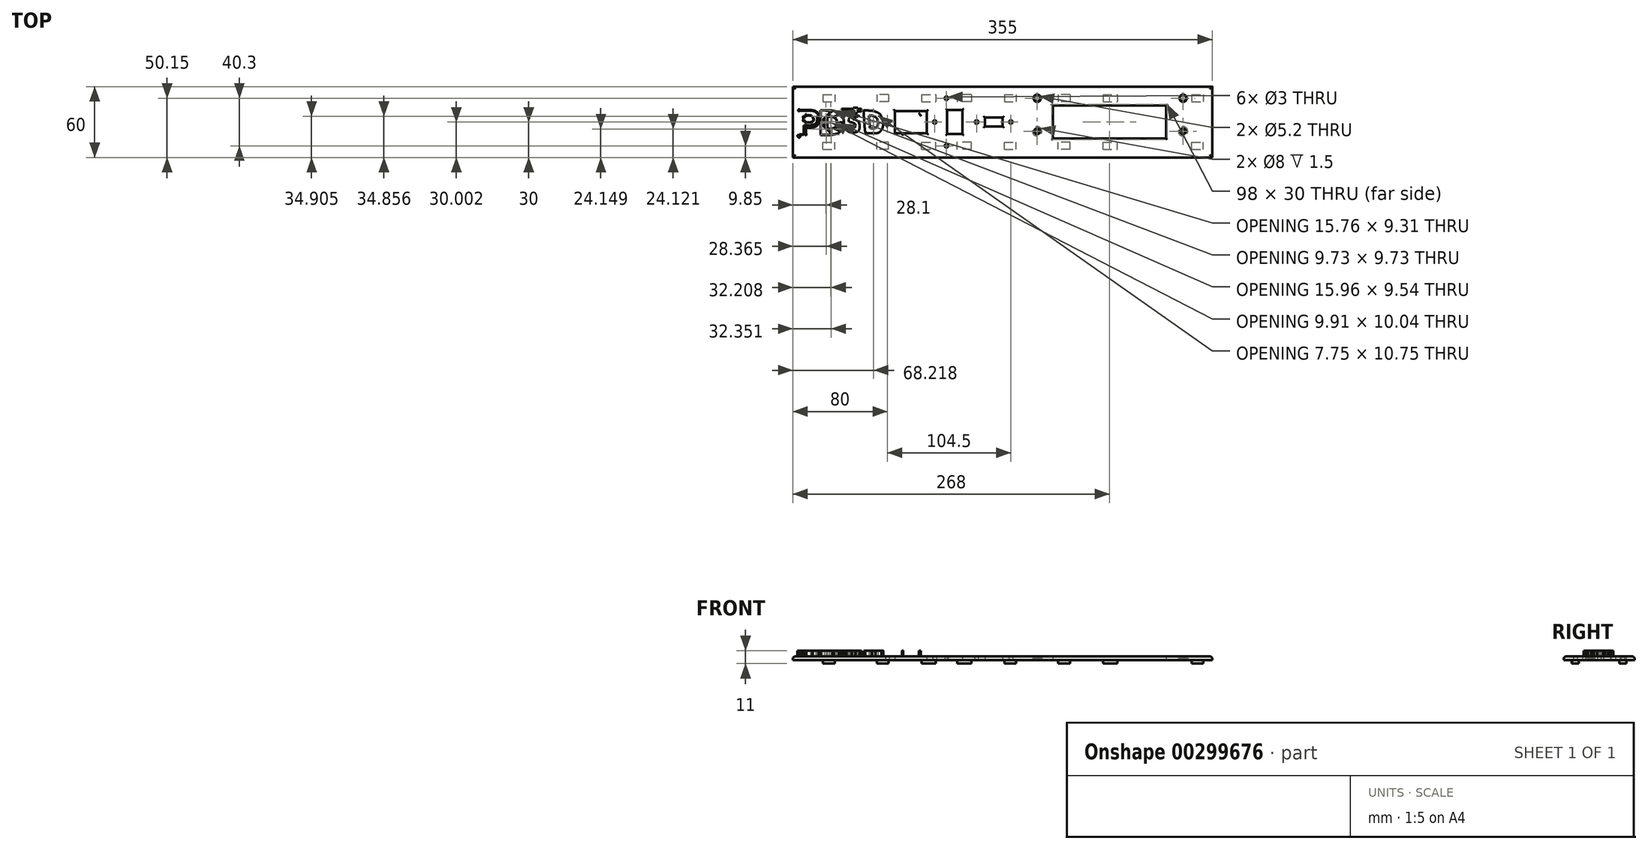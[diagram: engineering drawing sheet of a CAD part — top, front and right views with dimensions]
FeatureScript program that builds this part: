
annotation { "Feature Type Name" : "Feature", "Feature Type Description" : "" }
export const myFeature = defineFeature(function(context is Context, id is Id, definition is map)
    precondition{}
    {
        {
            var Q0;
            Q0=qCreatedBy(makeId("Top.planeOp"),FACE);
            var sketch = newSketch(context, id + "F0", { "sketchPlane" : qUnion([Q0])});
            skLineSegment(sketch, "E0.bottom", {"start": v(60, 30) * mm, "end": v(-60, 30) * mm});
            skLineSegment(sketch, "E0.top", {"start": v(60, -30) * mm, "end": v(-60, -30) * mm});
            skPoint(sketch, "E0.middle", {"position": v(0, 0) * mm});
            skLineSegment(sketch, "E1", {"start": v(0, 0) * mm, "end": v(0, 20.15) * mm, "construction": true});
            skLineSegment(sketch, "E2", {"start": v(-60, 20.15) * mm, "end": v(60, 20.15) * mm, "construction": true});
            skLineSegment(sketch, "E3", {"start": v(-60, 20.15) * mm, "end": v(-53.98, 20.15) * mm, "construction": true});
            skLineSegment(sketch, "E4.bottom", {"start": v(-48.98, 23.1) * mm, "end": v(-58.98, 23.1) * mm});
            skLineSegment(sketch, "E4.top", {"start": v(-48.98, 17.2) * mm, "end": v(-58.98, 17.2) * mm});
            skLineSegment(sketch, "E4.left", {"start": v(-48.98, 23.1) * mm, "end": v(-48.98, 17.2) * mm});
            skLineSegment(sketch, "E4.right", {"start": v(-58.98, 23.1) * mm, "end": v(-58.98, 17.2) * mm});
            skPoint(sketch, "E4.middle", {"position": v(-53.98, 20.15) * mm});
            skLineSegment(sketch, "E5", {"start": v(0, 20.15) * mm, "end": v(-15, 20.15) * mm, "construction": true});
            skLineSegment(sketch, "E6.bottom", {"start": v(-21.02, 23.15) * mm, "end": v(-8.98, 23.15) * mm});
            skLineSegment(sketch, "E6.top", {"start": v(-21.02, 17.15) * mm, "end": v(-8.98, 17.15) * mm});
            skLineSegment(sketch, "E6.left", {"start": v(-21.02, 23.15) * mm, "end": v(-21.02, 17.15) * mm});
            skLineSegment(sketch, "E6.right", {"start": v(-8.98, 23.15) * mm, "end": v(-8.98, 17.15) * mm});
            skPoint(sketch, "E6.middle", {"position": v(-15, 20.15) * mm});
            skLineSegment(sketch, "E7.MirrorCS", {"start": v(48.98, 23.1) * mm, "end": v(58.98, 23.1) * mm});
            skLineSegment(sketch, "E8.MirrorCS", {"start": v(48.98, 17.2) * mm, "end": v(58.98, 17.2) * mm});
            skLineSegment(sketch, "E9.MirrorCS", {"start": v(58.98, 23.1) * mm, "end": v(58.98, 17.2) * mm});
            skLineSegment(sketch, "E10.MirrorCS", {"start": v(48.98, 23.1) * mm, "end": v(48.98, 17.2) * mm});
            skLineSegment(sketch, "E11.MirrorCS", {"start": v(21.02, 17.15) * mm, "end": v(8.98, 17.15) * mm});
            skLineSegment(sketch, "E12.MirrorCS", {"start": v(21.02, 23.15) * mm, "end": v(8.98, 23.15) * mm});
            skLineSegment(sketch, "E13.MirrorCS", {"start": v(21.02, 23.15) * mm, "end": v(21.02, 17.15) * mm});
            skLineSegment(sketch, "E14.MirrorCS", {"start": v(8.98, 23.15) * mm, "end": v(8.98, 17.15) * mm});
            skLineSegment(sketch, "E15.MirrorCS", {"start": v(-58.98, -23.1) * mm, "end": v(-58.98, -17.2) * mm});
            skLineSegment(sketch, "E16.MirrorCS", {"start": v(-48.98, -23.1) * mm, "end": v(-48.98, -17.2) * mm});
            skLineSegment(sketch, "E17.MirrorCS", {"start": v(-21.02, -23.15) * mm, "end": v(-21.02, -17.15) * mm});
            skLineSegment(sketch, "E18.MirrorCS", {"start": v(-8.98, -23.15) * mm, "end": v(-8.98, -17.15) * mm});
            skLineSegment(sketch, "E19.MirrorCS", {"start": v(8.98, -23.15) * mm, "end": v(8.98, -17.15) * mm});
            skLineSegment(sketch, "E20.MirrorCS", {"start": v(21.02, -23.15) * mm, "end": v(21.02, -17.15) * mm});
            skLineSegment(sketch, "E21.MirrorCS", {"start": v(48.98, -23.1) * mm, "end": v(48.98, -17.2) * mm});
            skLineSegment(sketch, "E22.MirrorCS", {"start": v(58.98, -23.1) * mm, "end": v(58.98, -17.2) * mm});
            skLineSegment(sketch, "E23.MirrorCS", {"start": v(48.98, -23.1) * mm, "end": v(58.98, -23.1) * mm});
            skLineSegment(sketch, "E24.MirrorCS", {"start": v(21.02, -23.15) * mm, "end": v(8.98, -23.15) * mm});
            skLineSegment(sketch, "E25.MirrorCS", {"start": v(-21.02, -23.15) * mm, "end": v(-8.98, -23.15) * mm});
            skLineSegment(sketch, "E26.MirrorCS", {"start": v(-48.98, -23.1) * mm, "end": v(-58.98, -23.1) * mm});
            skLineSegment(sketch, "E27.MirrorCS", {"start": v(-48.98, -17.2) * mm, "end": v(-58.98, -17.2) * mm});
            skLineSegment(sketch, "E28.MirrorCS", {"start": v(-21.02, -17.15) * mm, "end": v(-8.98, -17.15) * mm});
            skLineSegment(sketch, "E29.MirrorCS", {"start": v(21.02, -17.15) * mm, "end": v(8.98, -17.15) * mm});
            skLineSegment(sketch, "E30.MirrorCS", {"start": v(48.98, -17.2) * mm, "end": v(58.98, -17.2) * mm});
            skLineSegment(sketch, "E31", {"start": v(0, 0) * mm, "end": v(-30, 0) * mm, "construction": true});
            skLineSegment(sketch, "E32.bottom", {"start": v(-43.5, -9.4) * mm, "end": v(-16.5, -9.4) * mm});
            skLineSegment(sketch, "E32.top", {"start": v(-43.5, 9.4) * mm, "end": v(-16.5, 9.4) * mm});
            skLineSegment(sketch, "E32.left", {"start": v(-43.5, -9.4) * mm, "end": v(-43.5, 9.4) * mm});
            skLineSegment(sketch, "E32.right", {"start": v(-16.5, -9.4) * mm, "end": v(-16.5, 9.4) * mm});
            skPoint(sketch, "E32.middle", {"position": v(-30, 0) * mm});
            skLineSegment(sketch, "E33", {"start": v(60, 0) * mm, "end": v(40, 0) * mm, "construction": true});
            skPoint(sketch, "E33.endSnap0", {"position": v(60, 0) * mm});
            skLineSegment(sketch, "E34.bottom", {"start": v(47.5, 3.75) * mm, "end": v(32.5, 3.75) * mm});
            skLineSegment(sketch, "E34.top", {"start": v(47.5, -3.75) * mm, "end": v(32.5, -3.75) * mm});
            skLineSegment(sketch, "E34.left", {"start": v(47.5, 3.75) * mm, "end": v(47.5, -3.75) * mm});
            skLineSegment(sketch, "E34.right", {"start": v(32.5, 3.75) * mm, "end": v(32.5, -3.75) * mm});
            skPoint(sketch, "E34.middle", {"position": v(40, 0) * mm});
            skLineSegment(sketch, "E35", {"start": v(-30, 0) * mm, "end": v(-50, 0) * mm, "construction": true});
            skLineSegment(sketch, "E36", {"start": v(-30, 0) * mm, "end": v(-10, 0) * mm, "construction": true});
            skCircle(sketch, "E37", {"center": v(-10, 0) * mm, "radius": 1.5 * mm});
            skLineSegment(sketch, "E38", {"start": v(-30, 0) * mm, "end": v(-30, 7) * mm, "construction": true});
            skCircle(sketch, "E39.MirrorC", {"center": v(-50, 0) * mm, "radius": 1.5 * mm});
            skLineSegment(sketch, "E40", {"start": v(40, 0) * mm, "end": v(25.5, 0) * mm, "construction": true});
            skLineSegment(sketch, "E41", {"start": v(40, 0) * mm, "end": v(40, 7) * mm, "construction": true});
            skPoint(sketch, "E41.endSnap0", {"position": v(40, 3.75) * mm});
            skCircle(sketch, "E42", {"center": v(25.5, 0) * mm, "radius": 1.5 * mm});
            skCircle(sketch, "E43.MirrorC", {"center": v(54.5, 0) * mm, "radius": 1.5 * mm});
            skCircle(sketch, "E44", {"center": v(0, 20.15) * mm, "radius": 1.5 * mm});
            skCircle(sketch, "E45.MirrorC", {"center": v(0, -20.15) * mm, "radius": 1.5 * mm});
            skLineSegment(sketch, "E46", {"start": v(0, 0) * mm, "end": v(7, 0) * mm, "construction": true});
            skLineSegment(sketch, "E47.bottom", {"start": v(13.47, 10.2) * mm, "end": v(0.52, 10.2) * mm});
            skLineSegment(sketch, "E47.top", {"start": v(13.48, -10.2) * mm, "end": v(0.53, -10.2) * mm});
            skLineSegment(sketch, "E47.left", {"start": v(13.47, 10.2) * mm, "end": v(13.48, -10.2) * mm});
            skLineSegment(sketch, "E47.right", {"start": v(0.52, 10.2) * mm, "end": v(0.53, -10.2) * mm});
            skPoint(sketch, "E47.middle", {"position": v(7, 0) * mm});
            skLineSegment(sketch, "E48", {"start": v(-60, 30) * mm, "end": v(-130, 30) * mm});
            skLineSegment(sketch, "E49", {"start": v(-130, 30) * mm, "end": v(-130, -30) * mm});
            skLineSegment(sketch, "E50", {"start": v(-130, -30) * mm, "end": v(-60, -30) * mm});
            skLineSegment(sketch, "E51", {"start": v(60, 30) * mm, "end": v(225, 30) * mm});
            skLineSegment(sketch, "E52", {"start": v(225, 30) * mm, "end": v(225, -30) * mm});
            skLineSegment(sketch, "E53", {"start": v(225, -30) * mm, "end": v(60, -30) * mm});
            skLineSegment(sketch, "E54", {"start": v(60, 30) * mm, "end": v(215, 30) * mm, "construction": true});
            skLineSegment(sketch, "E55", {"start": v(215, 30) * mm, "end": v(215, -13.9) * mm, "construction": true});
            skLineSegment(sketch, "E56", {"start": v(215, -13.9) * mm, "end": v(60, -13.9) * mm, "construction": true});
            skLineSegment(sketch, "E57", {"start": v(60, -13.9) * mm, "end": v(60, 30) * mm, "construction": true});
            skLineSegment(sketch, "E58", {"start": v(60, 20.15) * mm, "end": v(76.75, 20.15) * mm, "construction": true});
            skCircle(sketch, "E59", {"center": v(76.75, 20.15) * mm, "radius": 2.6 * mm});
            skLineSegment(sketch, "E60", {"start": v(76.75, 20.15) * mm, "end": v(76.75, -7.85) * mm, "construction": true});
            skCircle(sketch, "E61", {"center": v(76.75, -7.85) * mm, "radius": 1.98 * mm});
            skLineSegment(sketch, "E62", {"start": v(76.75, -7.85) * mm, "end": v(200.25, -7.85) * mm, "construction": true});
            skCircle(sketch, "E63", {"center": v(200.25, -7.85) * mm, "radius": 1.98 * mm});
            skLineSegment(sketch, "E64", {"start": v(200.25, -7.85) * mm, "end": v(200.25, 20.15) * mm, "construction": true});
            skCircle(sketch, "E65", {"center": v(200.25, 20.15) * mm, "radius": 2.6 * mm});
            skLineSegment(sketch, "E66", {"start": v(60, 30) * mm, "end": v(90, 30) * mm, "construction": true});
            skLineSegment(sketch, "E67", {"start": v(90, 30) * mm, "end": v(90, 14) * mm, "construction": true});
            skLineSegment(sketch, "E68.bottom", {"start": v(90, 14) * mm, "end": v(186, 14) * mm});
            skLineSegment(sketch, "E68.top", {"start": v(90, -14) * mm, "end": v(186, -14) * mm});
            skLineSegment(sketch, "E68.left", {"start": v(90, 14) * mm, "end": v(90, -14) * mm});
            skLineSegment(sketch, "E68.right", {"start": v(186, 14) * mm, "end": v(186, -14) * mm});
            skLineSegment(sketch, "E69.MirrorCS", {"start": v(104.52, 23.1) * mm, "end": v(94.52, 23.1) * mm});
            skLineSegment(sketch, "E70.MirrorCS", {"start": v(104.52, 23.1) * mm, "end": v(104.52, 17.2) * mm});
            skLineSegment(sketch, "E71.MirrorCS", {"start": v(94.52, 23.1) * mm, "end": v(94.52, 17.2) * mm});
            skLineSegment(sketch, "E72.MirrorCS", {"start": v(104.52, 17.2) * mm, "end": v(94.52, 17.2) * mm});
            skLineSegment(sketch, "E73.MirrorCS", {"start": v(132.48, 17.15) * mm, "end": v(144.52, 17.15) * mm});
            skLineSegment(sketch, "E74.MirrorCS", {"start": v(132.48, 23.15) * mm, "end": v(144.52, 23.15) * mm});
            skLineSegment(sketch, "E75.MirrorCS", {"start": v(144.52, 23.15) * mm, "end": v(144.52, 17.15) * mm});
            skLineSegment(sketch, "E76.MirrorCS", {"start": v(132.48, 23.15) * mm, "end": v(132.48, 17.15) * mm});
            skLineSegment(sketch, "E77.bottom", {"start": v(207.48, 23.1) * mm, "end": v(217.48, 23.1) * mm});
            skLineSegment(sketch, "E77.top", {"start": v(207.48, 17.2) * mm, "end": v(217.48, 17.2) * mm});
            skLineSegment(sketch, "E77.left", {"start": v(207.48, 23.1) * mm, "end": v(207.48, 17.2) * mm});
            skLineSegment(sketch, "E77.right", {"start": v(217.48, 23.1) * mm, "end": v(217.48, 17.2) * mm});
            skLineSegment(sketch, "E78.MirrorCS", {"start": v(-104.52, 23.1) * mm, "end": v(-104.52, 17.2) * mm});
            skLineSegment(sketch, "E79.MirrorCS", {"start": v(-94.52, 23.1) * mm, "end": v(-94.52, 17.2) * mm});
            skLineSegment(sketch, "E80.MirrorCS", {"start": v(-104.52, 23.1) * mm, "end": v(-94.52, 23.1) * mm});
            skLineSegment(sketch, "E81.MirrorCS", {"start": v(-104.52, 17.2) * mm, "end": v(-94.52, 17.2) * mm});
            skLineSegment(sketch, "E82.MirrorCS", {"start": v(-104.52, -23.1) * mm, "end": v(-94.52, -23.1) * mm});
            skLineSegment(sketch, "E83.MirrorCS", {"start": v(-104.52, -17.2) * mm, "end": v(-94.52, -17.2) * mm});
            skLineSegment(sketch, "E84.MirrorCS", {"start": v(-104.52, -23.1) * mm, "end": v(-104.52, -17.2) * mm});
            skLineSegment(sketch, "E85.MirrorCS", {"start": v(-94.52, -23.1) * mm, "end": v(-94.52, -17.2) * mm});
            skLineSegment(sketch, "E86.MirrorCS", {"start": v(104.52, -23.1) * mm, "end": v(94.52, -23.1) * mm});
            skLineSegment(sketch, "E87.MirrorCS", {"start": v(104.52, -17.2) * mm, "end": v(94.52, -17.2) * mm});
            skLineSegment(sketch, "E88.MirrorCS", {"start": v(94.52, -23.1) * mm, "end": v(94.52, -17.2) * mm});
            skLineSegment(sketch, "E89.MirrorCS", {"start": v(104.52, -23.1) * mm, "end": v(104.52, -17.2) * mm});
            skLineSegment(sketch, "E90.MirrorCS", {"start": v(132.48, -23.15) * mm, "end": v(144.52, -23.15) * mm});
            skLineSegment(sketch, "E91.MirrorCS", {"start": v(132.48, -17.15) * mm, "end": v(144.52, -17.15) * mm});
            skLineSegment(sketch, "E92.MirrorCS", {"start": v(132.48, -23.15) * mm, "end": v(132.48, -17.15) * mm});
            skLineSegment(sketch, "E93.MirrorCS", {"start": v(144.52, -23.15) * mm, "end": v(144.52, -17.15) * mm});
            skLineSegment(sketch, "E94.MirrorCS", {"start": v(207.48, -23.1) * mm, "end": v(207.48, -17.2) * mm});
            skLineSegment(sketch, "E95.MirrorCS", {"start": v(217.48, -23.1) * mm, "end": v(217.48, -17.2) * mm});
            skLineSegment(sketch, "E96.MirrorCS", {"start": v(207.48, -23.1) * mm, "end": v(217.48, -23.1) * mm});
            skLineSegment(sketch, "E97.MirrorCS", {"start": v(207.48, -17.2) * mm, "end": v(217.48, -17.2) * mm});
            skCircle(sketch, "E98", {"center": v(76.75, -7.85) * mm, "radius": 4 * mm});
            skCircle(sketch, "E99", {"center": v(200.25, -7.85) * mm, "radius": 4 * mm});
            skSolve(sketch);
        }
        {
            var Q0;
            Q0=qSketchRegion(id+"F0",true);
            var Q1;
            Q1=makeQuery(id+"F0.imprint","IMPRINT",FACE,{"disambiguationData":[TD([[makeQuery(id+"F0.imprint","IMPRINT",EDGE,{"derivedFrom":sQuery(id+"F0.wireOp",EDGE,"E6.bottom")}),-1.0]])]});
            var Q2;
            Q2=makeQuery(id+"F0.imprint","IMPRINT",FACE,{"disambiguationData":[TD([[makeQuery(id+"F0.imprint","IMPRINT",EDGE,{"derivedFrom":sQuery(id+"F0.wireOp",EDGE,"E11.MirrorCS")}),-1.0]])]});
            var Q3;
            Q3=makeQuery(id+"F0.imprint","IMPRINT",FACE,{"disambiguationData":[TD([[makeQuery(id+"F0.imprint","IMPRINT",EDGE,{"derivedFrom":sQuery(id+"F0.wireOp",EDGE,"E19.MirrorCS")}),-1.0]])]});
            var Q4;
            Q4=makeQuery(id+"F0.imprint","IMPRINT",FACE,{"disambiguationData":[TD([[makeQuery(id+"F0.imprint","IMPRINT",EDGE,{"derivedFrom":sQuery(id+"F0.wireOp",EDGE,"E17.MirrorCS")}),-1.0]])]});
            var Q5;
            Q5=makeQuery(id+"F0.imprint","IMPRINT",FACE,{"disambiguationData":[TD([[makeQuery(id+"F0.imprint","IMPRINT",EDGE,{"derivedFrom":sQuery(id+"F0.wireOp",EDGE,"E4.bottom")}),1.0]])]});
            var Q6;
            Q6=makeQuery(id+"F0.imprint","IMPRINT",FACE,{"disambiguationData":[TD([[makeQuery(id+"F0.imprint","IMPRINT",EDGE,{"derivedFrom":sQuery(id+"F0.wireOp",EDGE,"E15.MirrorCS")}),-1.0]])]});
            var Q7;
            Q7=makeQuery(id+"F0.imprint","IMPRINT",FACE,{"disambiguationData":[TD([[makeQuery(id+"F0.imprint","IMPRINT",EDGE,{"derivedFrom":sQuery(id+"F0.wireOp",EDGE,"E21.MirrorCS")}),-1.0]])]});
            var Q8;
            Q8=makeQuery(id+"F0.imprint","IMPRINT",FACE,{"disambiguationData":[TD([[makeQuery(id+"F0.imprint","IMPRINT",EDGE,{"derivedFrom":sQuery(id+"F0.wireOp",EDGE,"E7.MirrorCS")}),-1.0]])]});
            var Q9;
            Q9=makeQuery(id+"F0.imprint","IMPRINT",FACE,{"disambiguationData":[TD([[makeQuery(id+"F0.imprint","IMPRINT",EDGE,{"derivedFrom":sQuery(id+"F0.wireOp",EDGE,"E78.MirrorCS")}),1.0]])]});
            var Q10;
            Q10=makeQuery(id+"F0.imprint","IMPRINT",FACE,{"disambiguationData":[TD([[makeQuery(id+"F0.imprint","IMPRINT",EDGE,{"derivedFrom":sQuery(id+"F0.wireOp",EDGE,"E82.MirrorCS")}),1.0]])]});
            var Q11;
            Q11=makeQuery(id+"F0.imprint","IMPRINT",FACE,{"disambiguationData":[TD([[makeQuery(id+"F0.imprint","IMPRINT",EDGE,{"derivedFrom":sQuery(id+"F0.wireOp",EDGE,"E86.MirrorCS")}),-1.0]])]});
            var Q12;
            Q12=makeQuery(id+"F0.imprint","IMPRINT",FACE,{"disambiguationData":[TD([[makeQuery(id+"F0.imprint","IMPRINT",EDGE,{"derivedFrom":sQuery(id+"F0.wireOp",EDGE,"E69.MirrorCS")}),1.0]])]});
            var Q13;
            Q13=makeQuery(id+"F0.imprint","IMPRINT",FACE,{"disambiguationData":[TD([[makeQuery(id+"F0.imprint","IMPRINT",EDGE,{"derivedFrom":sQuery(id+"F0.wireOp",EDGE,"E73.MirrorCS")}),1.0]])]});
            var Q14;
            Q14=makeQuery(id+"F0.imprint","IMPRINT",FACE,{"disambiguationData":[TD([[makeQuery(id+"F0.imprint","IMPRINT",EDGE,{"derivedFrom":sQuery(id+"F0.wireOp",EDGE,"E90.MirrorCS")}),1.0]])]});
            var Q15;
            Q15=makeQuery(id+"F0.imprint","IMPRINT",FACE,{"disambiguationData":[TD([[makeQuery(id+"F0.imprint","IMPRINT",EDGE,{"derivedFrom":sQuery(id+"F0.wireOp",EDGE,"E94.MirrorCS")}),-1.0]])]});
            var Q16;
            Q16=makeQuery(id+"F0.imprint","IMPRINT",FACE,{"disambiguationData":[TD([[makeQuery(id+"F0.imprint","IMPRINT",EDGE,{"derivedFrom":sQuery(id+"F0.wireOp",EDGE,"E77.bottom")}),-1.0]])]});
            var Q17;
            Q17=makeQuery(id+"F0.imprint","IMPRINT",FACE,{"disambiguationData":[TD([[makeQuery(id+"F0.imprint","IMPRINT",EDGE,{"derivedFrom":sQuery(id+"F0.wireOp",EDGE,"E61")}),-1.0]])]});
            var Q18;
            Q18=makeQuery(id+"F0.imprint","IMPRINT",FACE,{"disambiguationData":[TD([[makeQuery(id+"F0.imprint","IMPRINT",EDGE,{"derivedFrom":sQuery(id+"F0.wireOp",EDGE,"E63")}),-1.0]])]});
            extrude(context, id + "F1", {"entities" : qUnion([Q0, Q1, Q2, Q3, Q4, Q5, Q6, Q7, Q8, Q9, Q10, Q11, Q12, Q13, Q14, Q15, Q16, Q17, Q18]), "depth" : 3 * mm});
        }
        {
            var Q0;
            Q0=makeQuery(id+"F1.opExtrude","CAP_EDGE",EDGE,{"disambiguationData":[OSD([sQuery(id+"F0.wireOp",EDGE,"E0.top")])],"isStart":false});
            var Q1;
            Q1=makeQuery(id+"F1.opExtrude","CAP_EDGE",EDGE,{"disambiguationData":[OSD([sQuery(id+"F0.wireOp",EDGE,"E0.bottom")])],"isStart":false});
            var Q2;
            Q2=makeQuery(id+"F1.opExtrude","CAP_EDGE",EDGE,{"disambiguationData":[OSD([sQuery(id+"F0.wireOp",EDGE,"E0.right")])],"isStart":false});
            var Q3;
            Q3=makeQuery(id+"F1.opExtrude","CAP_EDGE",EDGE,{"disambiguationData":[OSD([sQuery(id+"F0.wireOp",EDGE,"E0.left")])],"isStart":false});
            var Q4;
            Q4=makeQuery(id+"F1.opExtrude","CAP_EDGE",EDGE,{"disambiguationData":[OSD([sQuery(id+"F0.wireOp",EDGE,"E49")])],"isStart":false});
            var Q5;
            Q5=makeQuery(id+"F1.opExtrude","CAP_EDGE",EDGE,{"disambiguationData":[OSD([sQuery(id+"F0.wireOp",EDGE,"E52")])],"isStart":false});
            fillet(context, id + "F2", {"entities" : qUnion([Q0, Q1, Q2, Q3, Q4, Q5]), "radius" : 2 * mm, "tangentPropagation" : true, "allowEdgeOverflow" : false});
        }
        {
            var Q0;
            Q0=makeQuery(id+"F1.opExtrude","CAP_EDGE",EDGE,{"disambiguationData":[OSD([sQuery(id+"F0.wireOp",EDGE,"E34.left")])],"isStart":false});
            var Q1;
            Q1=makeQuery(id+"F1.opExtrude","CAP_EDGE",EDGE,{"disambiguationData":[OSD([sQuery(id+"F0.wireOp",EDGE,"E34.right")])],"isStart":false});
            var Q2;
            Q2=makeQuery(id+"F1.opExtrude","CAP_EDGE",EDGE,{"disambiguationData":[OSD([sQuery(id+"F0.wireOp",EDGE,"E34.bottom")])],"isStart":false});
            var Q3;
            Q3=makeQuery(id+"F1.opExtrude","CAP_EDGE",EDGE,{"disambiguationData":[OSD([sQuery(id+"F0.wireOp",EDGE,"E34.top")])],"isStart":false});
            var Q4;
            Q4=makeQuery(id+"F1.opExtrude","CAP_EDGE",EDGE,{"disambiguationData":[OSD([sQuery(id+"F0.wireOp",EDGE,"E32.top")])],"isStart":false});
            var Q5;
            Q5=makeQuery(id+"F1.opExtrude","CAP_EDGE",EDGE,{"disambiguationData":[OSD([sQuery(id+"F0.wireOp",EDGE,"E32.bottom")])],"isStart":false});
            var Q6;
            Q6=makeQuery(id+"F1.opExtrude","CAP_EDGE",EDGE,{"disambiguationData":[OSD([sQuery(id+"F0.wireOp",EDGE,"E32.left")])],"isStart":false});
            var Q7;
            Q7=makeQuery(id+"F1.opExtrude","CAP_EDGE",EDGE,{"disambiguationData":[OSD([sQuery(id+"F0.wireOp",EDGE,"E32.right")])],"isStart":false});
            var Q8;
            Q8=makeQuery(id+"F1.opExtrude","CAP_EDGE",EDGE,{"disambiguationData":[OSD([sQuery(id+"F0.wireOp",EDGE,"E47.left")])],"isStart":false});
            var Q9;
            Q9=makeQuery(id+"F1.opExtrude","CAP_EDGE",EDGE,{"disambiguationData":[OSD([sQuery(id+"F0.wireOp",EDGE,"E47.right")])],"isStart":false});
            var Q10;
            Q10=makeQuery(id+"F1.opExtrude","CAP_EDGE",EDGE,{"disambiguationData":[OSD([sQuery(id+"F0.wireOp",EDGE,"E47.bottom")])],"isStart":false});
            var Q11;
            Q11=makeQuery(id+"F1.opExtrude","CAP_EDGE",EDGE,{"disambiguationData":[OSD([sQuery(id+"F0.wireOp",EDGE,"E47.top")])],"isStart":false});
            var Q12;
            Q12=makeQuery(id+"F1.opExtrude","CAP_EDGE",EDGE,{"disambiguationData":[OSD([sQuery(id+"F0.wireOp",EDGE,"E68.bottom")])],"isStart":false});
            var Q13;
            Q13=makeQuery(id+"F1.opExtrude","CAP_EDGE",EDGE,{"disambiguationData":[OSD([sQuery(id+"F0.wireOp",EDGE,"E68.top")])],"isStart":false});
            var Q14;
            Q14=makeQuery(id+"F1.opExtrude","CAP_EDGE",EDGE,{"disambiguationData":[OSD([sQuery(id+"F0.wireOp",EDGE,"E68.left")])],"isStart":false});
            var Q15;
            Q15=makeQuery(id+"F1.opExtrude","CAP_EDGE",EDGE,{"disambiguationData":[OSD([sQuery(id+"F0.wireOp",EDGE,"E68.right")])],"isStart":false});
            var Q16;
            Q16=makeQuery(id+"F1.opExtrude","CAP_EDGE",EDGE,{"disambiguationData":[OSD([sQuery(id+"F0.wireOp",EDGE,"E68.top")])],"isStart":true});
            var Q17;
            Q17=makeQuery(id+"F1.opExtrude","CAP_EDGE",EDGE,{"disambiguationData":[OSD([sQuery(id+"F0.wireOp",EDGE,"E68.bottom")])],"isStart":true});
            var Q18;
            Q18=makeQuery(id+"F1.opExtrude","CAP_EDGE",EDGE,{"disambiguationData":[OSD([sQuery(id+"F0.wireOp",EDGE,"E68.right")])],"isStart":true});
            var Q19;
            Q19=makeQuery(id+"F1.opExtrude","CAP_EDGE",EDGE,{"disambiguationData":[OSD([sQuery(id+"F0.wireOp",EDGE,"E68.left")])],"isStart":true});
            fillet(context, id + "F3", {"entities" : qUnion([Q0, Q1, Q2, Q3, Q4, Q5, Q6, Q7, Q8, Q9, Q10, Q11, Q12, Q13, Q14, Q15, Q16, Q17, Q18, Q19]), "radius" : 1 * mm, "tangentPropagation" : true, "allowEdgeOverflow" : false});
        }
        {
            var Q0;
            Q0=makeQuery(id+"F1.opExtrude","CAP_EDGE",EDGE,{"disambiguationData":[OSD([sQuery(id+"F0.wireOp",EDGE,"E39.MirrorC")])],"isStart":false});
            var Q1;
            Q1=makeQuery(id+"F1.opExtrude","CAP_EDGE",EDGE,{"disambiguationData":[OSD([sQuery(id+"F0.wireOp",EDGE,"E37")])],"isStart":false});
            var Q2;
            Q2=makeQuery(id+"F1.opExtrude","CAP_EDGE",EDGE,{"disambiguationData":[OSD([sQuery(id+"F0.wireOp",EDGE,"E42")])],"isStart":false});
            var Q3;
            Q3=makeQuery(id+"F1.opExtrude","CAP_EDGE",EDGE,{"disambiguationData":[OSD([sQuery(id+"F0.wireOp",EDGE,"E43.MirrorC")])],"isStart":false});
            var Q4;
            Q4=makeQuery(id+"F1.opExtrude","CAP_EDGE",EDGE,{"disambiguationData":[OSD([sQuery(id+"F0.wireOp",EDGE,"E45.MirrorC")])],"isStart":false});
            var Q5;
            Q5=makeQuery(id+"F1.opExtrude","CAP_EDGE",EDGE,{"disambiguationData":[OSD([sQuery(id+"F0.wireOp",EDGE,"E44")])],"isStart":false});
            fillet(context, id + "F4", {"entities" : qUnion([Q0, Q1, Q2, Q3, Q4, Q5]), "radius" : 0.5 * mm, "tangentPropagation" : true, "allowEdgeOverflow" : false});
        }
        {
            var Q0;
            Q0=makeQuery(id+"F0.imprint","IMPRINT",FACE,{"disambiguationData":[TD([[makeQuery(id+"F0.imprint","IMPRINT",EDGE,{"derivedFrom":sQuery(id+"F0.wireOp",EDGE,"E7.MirrorCS")}),-1.0]])]});
            var Q1;
            Q1=makeQuery(id+"F0.imprint","IMPRINT",FACE,{"disambiguationData":[TD([[makeQuery(id+"F0.imprint","IMPRINT",EDGE,{"derivedFrom":sQuery(id+"F0.wireOp",EDGE,"E11.MirrorCS")}),-1.0]])]});
            var Q2;
            Q2=makeQuery(id+"F0.imprint","IMPRINT",FACE,{"disambiguationData":[TD([[makeQuery(id+"F0.imprint","IMPRINT",EDGE,{"derivedFrom":sQuery(id+"F0.wireOp",EDGE,"E6.bottom")}),-1.0]])]});
            var Q3;
            Q3=makeQuery(id+"F0.imprint","IMPRINT",FACE,{"disambiguationData":[TD([[makeQuery(id+"F0.imprint","IMPRINT",EDGE,{"derivedFrom":sQuery(id+"F0.wireOp",EDGE,"E4.bottom")}),1.0]])]});
            var Q4;
            Q4=makeQuery(id+"F0.imprint","IMPRINT",FACE,{"disambiguationData":[TD([[makeQuery(id+"F0.imprint","IMPRINT",EDGE,{"derivedFrom":sQuery(id+"F0.wireOp",EDGE,"E15.MirrorCS")}),-1.0]])]});
            var Q5;
            Q5=makeQuery(id+"F0.imprint","IMPRINT",FACE,{"disambiguationData":[TD([[makeQuery(id+"F0.imprint","IMPRINT",EDGE,{"derivedFrom":sQuery(id+"F0.wireOp",EDGE,"E17.MirrorCS")}),-1.0]])]});
            var Q6;
            Q6=makeQuery(id+"F0.imprint","IMPRINT",FACE,{"disambiguationData":[TD([[makeQuery(id+"F0.imprint","IMPRINT",EDGE,{"derivedFrom":sQuery(id+"F0.wireOp",EDGE,"E19.MirrorCS")}),-1.0]])]});
            var Q7;
            Q7=makeQuery(id+"F0.imprint","IMPRINT",FACE,{"disambiguationData":[TD([[makeQuery(id+"F0.imprint","IMPRINT",EDGE,{"derivedFrom":sQuery(id+"F0.wireOp",EDGE,"E21.MirrorCS")}),-1.0]])]});
            var Q8;
            Q8=makeQuery(id+"F0.imprint","IMPRINT",FACE,{"disambiguationData":[TD([[makeQuery(id+"F0.imprint","IMPRINT",EDGE,{"derivedFrom":sQuery(id+"F0.wireOp",EDGE,"E78.MirrorCS")}),1.0]])]});
            var Q9;
            Q9=makeQuery(id+"F0.imprint","IMPRINT",FACE,{"disambiguationData":[TD([[makeQuery(id+"F0.imprint","IMPRINT",EDGE,{"derivedFrom":sQuery(id+"F0.wireOp",EDGE,"E82.MirrorCS")}),1.0]])]});
            var Q10;
            Q10=makeQuery(id+"F0.imprint","IMPRINT",FACE,{"disambiguationData":[TD([[makeQuery(id+"F0.imprint","IMPRINT",EDGE,{"derivedFrom":sQuery(id+"F0.wireOp",EDGE,"E69.MirrorCS")}),1.0]])]});
            var Q11;
            Q11=makeQuery(id+"F0.imprint","IMPRINT",FACE,{"disambiguationData":[TD([[makeQuery(id+"F0.imprint","IMPRINT",EDGE,{"derivedFrom":sQuery(id+"F0.wireOp",EDGE,"E86.MirrorCS")}),-1.0]])]});
            var Q12;
            Q12=makeQuery(id+"F0.imprint","IMPRINT",FACE,{"disambiguationData":[TD([[makeQuery(id+"F0.imprint","IMPRINT",EDGE,{"derivedFrom":sQuery(id+"F0.wireOp",EDGE,"E73.MirrorCS")}),1.0]])]});
            var Q13;
            Q13=makeQuery(id+"F0.imprint","IMPRINT",FACE,{"disambiguationData":[TD([[makeQuery(id+"F0.imprint","IMPRINT",EDGE,{"derivedFrom":sQuery(id+"F0.wireOp",EDGE,"E90.MirrorCS")}),1.0]])]});
            var Q14;
            Q14=makeQuery(id+"F0.imprint","IMPRINT",FACE,{"disambiguationData":[TD([[makeQuery(id+"F0.imprint","IMPRINT",EDGE,{"derivedFrom":sQuery(id+"F0.wireOp",EDGE,"E77.bottom")}),-1.0]])]});
            var Q15;
            Q15=makeQuery(id+"F0.imprint","IMPRINT",FACE,{"disambiguationData":[TD([[makeQuery(id+"F0.imprint","IMPRINT",EDGE,{"derivedFrom":sQuery(id+"F0.wireOp",EDGE,"E94.MirrorCS")}),-1.0]])]});
            extrude(context, id + "F5", {"entities" : qUnion([Q0, Q1, Q2, Q3, Q4, Q5, Q6, Q7, Q8, Q9, Q10, Q11, Q12, Q13, Q14, Q15]), "operationType" : NewBodyOperationType.ADD, "oppositeDirection" : true, "depth" : 3 * mm});
        }
        {
            var Q0;
            Q0=makeQuery(id+"F1.opExtrude","CAP_EDGE",EDGE,{"disambiguationData":[OSD([sQuery(id+"F0.wireOp",EDGE,"E59")])],"isStart":false});
            var Q1;
            Q1=makeQuery(id+"F1.opExtrude","CAP_EDGE",EDGE,{"disambiguationData":[OSD([sQuery(id+"F0.wireOp",EDGE,"E65")])],"isStart":false});
            var Q2;
            Q2=makeQuery(id+"F1.opExtrude","CAP_FACE",FACE,{"disambiguationData":[OSD([sQuery(id+"F0.wireOp",EDGE,"E0.bottom"),sQuery(id+"F0.wireOp",EDGE,"E0.top"),sQuery(id+"F0.wireOp",EDGE,"E32.bottom"),sQuery(id+"F0.wireOp",EDGE,"E32.top"),sQuery(id+"F0.wireOp",EDGE,"E32.left"),sQuery(id+"F0.wireOp",EDGE,"E32.right"),sQuery(id+"F0.wireOp",EDGE,"E34.bottom"),sQuery(id+"F0.wireOp",EDGE,"E34.top"),sQuery(id+"F0.wireOp",EDGE,"E34.left"),sQuery(id+"F0.wireOp",EDGE,"E34.right"),sQuery(id+"F0.wireOp",EDGE,"E37"),sQuery(id+"F0.wireOp",EDGE,"E39.MirrorC"),sQuery(id+"F0.wireOp",EDGE,"E42"),sQuery(id+"F0.wireOp",EDGE,"E43.MirrorC"),sQuery(id+"F0.wireOp",EDGE,"E44"),sQuery(id+"F0.wireOp",EDGE,"E45.MirrorC"),sQuery(id+"F0.wireOp",EDGE,"E47.bottom"),sQuery(id+"F0.wireOp",EDGE,"E47.top"),sQuery(id+"F0.wireOp",EDGE,"E47.left"),sQuery(id+"F0.wireOp",EDGE,"E47.right"),sQuery(id+"F0.wireOp",EDGE,"E48"),sQuery(id+"F0.wireOp",EDGE,"E49"),sQuery(id+"F0.wireOp",EDGE,"E50"),sQuery(id+"F0.wireOp",EDGE,"E51"),sQuery(id+"F0.wireOp",EDGE,"E52"),sQuery(id+"F0.wireOp",EDGE,"E53"),sQuery(id+"F0.wireOp",EDGE,"E59"),sQuery(id+"F0.wireOp",EDGE,"E61"),sQuery(id+"F0.wireOp",EDGE,"E63"),sQuery(id+"F0.wireOp",EDGE,"E65"),sQuery(id+"F0.wireOp",EDGE,"E68.bottom"),sQuery(id+"F0.wireOp",EDGE,"E68.top"),sQuery(id+"F0.wireOp",EDGE,"E68.left"),sQuery(id+"F0.wireOp",EDGE,"E68.right")])],"isStart":false});
            chamfer(context, id + "F6", {"entities" : qUnion([Q0, Q1, Q2]), "width" : .5 * mm, "tangentPropagation" : true});
        }
        {
            var Q0;
            Q0=makeQuery(id+"F0.imprint","IMPRINT",FACE,{"disambiguationData":[TD([[makeQuery(id+"F0.imprint","IMPRINT",EDGE,{"derivedFrom":sQuery(id+"F0.wireOp",EDGE,"E61")}),-1.0]])]});
            var Q1;
            Q1=makeQuery(id+"F0.imprint","IMPRINT",FACE,{"disambiguationData":[TD([[makeQuery(id+"F0.imprint","IMPRINT",EDGE,{"derivedFrom":sQuery(id+"F0.wireOp",EDGE,"E63")}),-1.0]])]});
            extrude(context, id + "F7", {"entities" : qUnion([Q0, Q1]), "operationType" : NewBodyOperationType.REMOVE, "depth" : 1.5 * mm});
        }
        {
            var Q0;
            Q0=makeQuery(id+"F1.opExtrude","CAP_FACE",FACE,{"disambiguationData":[OSD([sQuery(id+"F0.wireOp",EDGE,"E0.bottom"),sQuery(id+"F0.wireOp",EDGE,"E0.top"),sQuery(id+"F0.wireOp",EDGE,"E32.bottom"),sQuery(id+"F0.wireOp",EDGE,"E32.top"),sQuery(id+"F0.wireOp",EDGE,"E32.left"),sQuery(id+"F0.wireOp",EDGE,"E32.right"),sQuery(id+"F0.wireOp",EDGE,"E34.bottom"),sQuery(id+"F0.wireOp",EDGE,"E34.top"),sQuery(id+"F0.wireOp",EDGE,"E34.left"),sQuery(id+"F0.wireOp",EDGE,"E34.right"),sQuery(id+"F0.wireOp",EDGE,"E37"),sQuery(id+"F0.wireOp",EDGE,"E39.MirrorC"),sQuery(id+"F0.wireOp",EDGE,"E42"),sQuery(id+"F0.wireOp",EDGE,"E43.MirrorC"),sQuery(id+"F0.wireOp",EDGE,"E44"),sQuery(id+"F0.wireOp",EDGE,"E45.MirrorC"),sQuery(id+"F0.wireOp",EDGE,"E47.bottom"),sQuery(id+"F0.wireOp",EDGE,"E47.top"),sQuery(id+"F0.wireOp",EDGE,"E47.left"),sQuery(id+"F0.wireOp",EDGE,"E47.right"),sQuery(id+"F0.wireOp",EDGE,"E48"),sQuery(id+"F0.wireOp",EDGE,"E49"),sQuery(id+"F0.wireOp",EDGE,"E50"),sQuery(id+"F0.wireOp",EDGE,"E51"),sQuery(id+"F0.wireOp",EDGE,"E52"),sQuery(id+"F0.wireOp",EDGE,"E53"),sQuery(id+"F0.wireOp",EDGE,"E59"),sQuery(id+"F0.wireOp",EDGE,"E61"),sQuery(id+"F0.wireOp",EDGE,"E63"),sQuery(id+"F0.wireOp",EDGE,"E65"),sQuery(id+"F0.wireOp",EDGE,"E68.bottom"),sQuery(id+"F0.wireOp",EDGE,"E68.top"),sQuery(id+"F0.wireOp",EDGE,"E68.left"),sQuery(id+"F0.wireOp",EDGE,"E68.right")])],"isStart":false});
            var sketch = newSketch(context, id + "F8", { "sketchPlane" : qUnion([Q0])});
            skFitSpline(sketch, "E100", {"points": [v(-37.7, -11.02) * mm, v(-37.14, -11.02) * mm, v(-36.95, -10.98) * mm, v(-37.17, -10.9) * mm]});
            skFitSpline(sketch, "E101", {"points": [v(-37.17, -10.9) * mm, v(-37.3, -10.85) * mm, v(-37.46, -10.53) * mm, v(-37.46, -10.31) * mm]});
            skFitSpline(sketch, "E102", {"points": [v(-37.46, -10.31) * mm, v(-37.46, -9.87) * mm, v(-37.22, -9.63) * mm, v(-36.75, -9.63) * mm]});
            skFitSpline(sketch, "E103", {"points": [v(-36.75, -9.63) * mm, v(-36.49, -9.63) * mm, v(-36.42, -9.65) * mm, v(-36.26, -9.8) * mm]});
            skLineSegment(sketch, "E104", {"start": v(-37.09, -12.95) * mm, "end": v(-37.09, -12.74) * mm});
            skLineSegment(sketch, "E105", {"start": v(-37.09, -12.74) * mm, "end": v(-37.4, -12.74) * mm});
            skLineSegment(sketch, "E106", {"start": v(-37.4, -12.74) * mm, "end": v(-37.73, -12.74) * mm});
            skLineSegment(sketch, "E107", {"start": v(-37.73, -12.74) * mm, "end": v(-37.73, -12.42) * mm});
            skLineSegment(sketch, "E108", {"start": v(-37.73, -12.42) * mm, "end": v(-37.73, -12.1) * mm});
            skLineSegment(sketch, "E109", {"start": v(-37.73, -12.1) * mm, "end": v(-37.4, -12.1) * mm});
            skLineSegment(sketch, "E110", {"start": v(-37.4, -12.1) * mm, "end": v(-37.09, -12.1) * mm});
            skLineSegment(sketch, "E111", {"start": v(-37.09, -12.1) * mm, "end": v(-37.09, -11.88) * mm});
            skLineSegment(sketch, "E112", {"start": v(-37.09, -11.88) * mm, "end": v(-37.09, -11.67) * mm});
            skLineSegment(sketch, "E113", {"start": v(-37.09, -11.67) * mm, "end": v(-37.7, -11.67) * mm});
            skLineSegment(sketch, "E114", {"start": v(-37.7, -11.67) * mm, "end": v(-38.32, -11.67) * mm});
            skLineSegment(sketch, "E115", {"start": v(-38.32, -11.67) * mm, "end": v(-38.32, -11.35) * mm});
            skLineSegment(sketch, "E116", {"start": v(-38.32, -11.35) * mm, "end": v(-38.32, -11.02) * mm});
            skLineSegment(sketch, "E117", {"start": v(-38.32, -11.02) * mm, "end": v(-37.7, -11.02) * mm});
            skFitSpline(sketch, "E118", {"points": [v(-30.69, -2.23) * mm, v(-29.26, -2.23) * mm, v(-27.84, -2.2) * mm, v(-27.54, -2.18) * mm]});
            skFitSpline(sketch, "E119", {"points": [v(-27.54, -2.18) * mm, v(-25.4, -1.96) * mm, v(-23.68, -1.14) * mm, v(-22.8, 0.1) * mm]});
            skFitSpline(sketch, "E120", {"points": [v(-22.8, 0.1) * mm, v(-22.5, 0.54) * mm, v(-22.32, 0.89) * mm, v(-22.15, 1.45) * mm]});
            skFitSpline(sketch, "E121", {"points": [v(-22.15, 1.45) * mm, v(-22.03, 1.85) * mm, v(-22.01, 2.02) * mm, v(-22, 2.67) * mm]});
            skFitSpline(sketch, "E122", {"points": [v(-22, 2.67) * mm, v(-22, 3.8) * mm, v(-22.2, 4.5) * mm, v(-22.75, 5.35) * mm]});
            skFitSpline(sketch, "E123", {"points": [v(-22.75, 5.35) * mm, v(-23.4, 6.32) * mm, v(-24.37, 7) * mm, v(-25.77, 7.47) * mm]});
            skFitSpline(sketch, "E124", {"points": [v(-25.77, 7.47) * mm, v(-26.99, 7.87) * mm, v(-26.87, 7.86) * mm, v(-31.93, 7.88) * mm]});
            skLineSegment(sketch, "E125", {"start": v(-36.26, -9.8) * mm, "end": v(-36.08, -9.95) * mm});
            skLineSegment(sketch, "E126", {"start": v(-36.08, -9.95) * mm, "end": v(-34.68, -9.95) * mm});
            skLineSegment(sketch, "E127", {"start": v(-34.68, -9.95) * mm, "end": v(-33.28, -9.95) * mm});
            skLineSegment(sketch, "E128", {"start": v(-33.28, -9.95) * mm, "end": v(-33.28, -6.1) * mm});
            skLineSegment(sketch, "E129", {"start": v(-33.28, -6.1) * mm, "end": v(-33.28, -2.23) * mm});
            skLineSegment(sketch, "E130", {"start": v(-33.28, -2.23) * mm, "end": v(-30.69, -2.23) * mm});
            skFitSpline(sketch, "E131", {"points": [v(-36.44, 0.72) * mm, v(-36.44, -6.4) * mm, v(-36.44, -6.47) * mm, v(-36.34, -6.52) * mm]});
            skFitSpline(sketch, "E132", {"points": [v(-36.34, -6.52) * mm, v(-36.09, -6.66) * mm, v(-35.99, -7.17) * mm, v(-36.15, -7.49) * mm]});
            skFitSpline(sketch, "E133", {"points": [v(-36.15, -7.49) * mm, v(-36.38, -7.93) * mm, v(-37.2, -7.91) * mm, v(-37.39, -7.46) * mm]});
            skFitSpline(sketch, "E134", {"points": [v(-37.39, -7.46) * mm, v(-37.53, -7.12) * mm, v(-37.44, -6.71) * mm, v(-37.2, -6.54) * mm]});
            skFitSpline(sketch, "E135", {"points": [v(-37.2, -6.54) * mm, v(-37.09, -6.46) * mm, v(-37.09, -6.36) * mm, v(-37.09, 1.04) * mm]});
            skLineSegment(sketch, "E136", {"start": v(-31.93, 7.88) * mm, "end": v(-36.44, 7.9) * mm});
            skLineSegment(sketch, "E137", {"start": v(-36.44, 7.9) * mm, "end": v(-36.44, 0.72) * mm});
            skFitSpline(sketch, "E138", {"points": [v(-32.42, 8.54) * mm, v(-29.52, 8.54) * mm, v(-27.56, 8.52) * mm, v(-27.24, 8.48) * mm]});
            skFitSpline(sketch, "E139", {"points": [v(-27.24, 8.48) * mm, v(-25.12, 8.25) * mm, v(-23.23, 7.28) * mm, v(-22.26, 5.93) * mm]});
            skFitSpline(sketch, "E140", {"points": [v(-22.26, 5.93) * mm, v(-21.94, 5.48) * mm, v(-21.62, 4.79) * mm, v(-21.48, 4.22) * mm]});
            skFitSpline(sketch, "E141", {"points": [v(-21.48, 4.22) * mm, v(-21.37, 3.8) * mm, v(-21.36, 3.6) * mm, v(-21.36, 2.72) * mm]});
            skFitSpline(sketch, "E142", {"points": [v(-21.36, 2.72) * mm, v(-21.36, 1.85) * mm, v(-21.38, 1.64) * mm, v(-21.48, 1.28) * mm]});
            skFitSpline(sketch, "E143", {"points": [v(-21.48, 1.28) * mm, v(-22, -0.62) * mm, v(-23.55, -1.98) * mm, v(-25.87, -2.58) * mm]});
            skFitSpline(sketch, "E144", {"points": [v(-25.87, -2.58) * mm, v(-26.85, -2.84) * mm, v(-27.4, -2.88) * mm, v(-30.12, -2.88) * mm]});
            skLineSegment(sketch, "E145", {"start": v(-37.09, 1.04) * mm, "end": v(-37.09, 8.54) * mm});
            skLineSegment(sketch, "E146", {"start": v(-37.09, 8.54) * mm, "end": v(-32.42, 8.54) * mm});
            skFitSpline(sketch, "E147", {"points": [v(-36.25, -10.8) * mm, v(-36.32, -10.88) * mm, v(-36.39, -10.97) * mm, v(-36.39, -10.99) * mm]});
            skFitSpline(sketch, "E148", {"points": [v(-36.39, -10.99) * mm, v(-36.39, -11) * mm, v(-36.11, -11.02) * mm, v(-35.77, -11.02) * mm]});
            skLineSegment(sketch, "E149", {"start": v(-30.12, -2.88) * mm, "end": v(-32.64, -2.88) * mm});
            skLineSegment(sketch, "E150", {"start": v(-32.64, -2.88) * mm, "end": v(-32.64, -6.76) * mm});
            skLineSegment(sketch, "E151", {"start": v(-32.64, -6.76) * mm, "end": v(-32.64, -10.65) * mm});
            skLineSegment(sketch, "E152", {"start": v(-32.64, -10.65) * mm, "end": v(-34.37, -10.65) * mm});
            skLineSegment(sketch, "E153", {"start": v(-34.37, -10.65) * mm, "end": v(-36.1, -10.65) * mm});
            skLineSegment(sketch, "E154", {"start": v(-36.1, -10.65) * mm, "end": v(-36.25, -10.8) * mm});
            skLineSegment(sketch, "E155", {"start": v(-35.77, -11.02) * mm, "end": v(-35.16, -11.02) * mm});
            skLineSegment(sketch, "E156", {"start": v(-35.16, -11.02) * mm, "end": v(-35.16, -11.35) * mm});
            skLineSegment(sketch, "E157", {"start": v(-35.16, -11.35) * mm, "end": v(-35.16, -11.67) * mm});
            skLineSegment(sketch, "E158", {"start": v(-35.16, -11.67) * mm, "end": v(-35.77, -11.67) * mm});
            skLineSegment(sketch, "E159", {"start": v(-35.77, -11.67) * mm, "end": v(-36.39, -11.67) * mm});
            skLineSegment(sketch, "E160", {"start": v(-36.39, -11.67) * mm, "end": v(-36.39, -11.88) * mm});
            skLineSegment(sketch, "E161", {"start": v(-36.39, -11.88) * mm, "end": v(-36.39, -12.1) * mm});
            skLineSegment(sketch, "E162", {"start": v(-36.39, -12.1) * mm, "end": v(-36.07, -12.1) * mm});
            skLineSegment(sketch, "E163", {"start": v(-36.07, -12.1) * mm, "end": v(-35.75, -12.1) * mm});
            skLineSegment(sketch, "E164", {"start": v(-35.75, -12.1) * mm, "end": v(-35.75, -12.42) * mm});
            skLineSegment(sketch, "E165", {"start": v(-35.75, -12.42) * mm, "end": v(-35.75, -12.74) * mm});
            skLineSegment(sketch, "E166", {"start": v(-35.75, -12.74) * mm, "end": v(-36.07, -12.74) * mm});
            skLineSegment(sketch, "E167", {"start": v(-36.07, -12.74) * mm, "end": v(-36.39, -12.74) * mm});
            skLineSegment(sketch, "E168", {"start": v(-36.39, -12.74) * mm, "end": v(-36.39, -12.95) * mm});
            skLineSegment(sketch, "E169", {"start": v(-36.39, -12.95) * mm, "end": v(-36.39, -13.17) * mm});
            skLineSegment(sketch, "E170", {"start": v(-36.39, -13.17) * mm, "end": v(-36.74, -13.17) * mm});
            skLineSegment(sketch, "E171", {"start": v(-36.74, -13.17) * mm, "end": v(-37.09, -13.17) * mm});
            skLineSegment(sketch, "E172", {"start": v(-37.09, -13.17) * mm, "end": v(-37.09, -12.95) * mm});
            skFitSpline(sketch, "E173", {"points": [v(-36.5, -10.99) * mm, v(-36.5, -10.9) * mm, v(-36.44, -10.78) * mm, v(-36.35, -10.7) * mm]});
            skLineSegment(sketch, "E174", {"start": v(-36.5, -12.85) * mm, "end": v(-36.5, -12.63) * mm});
            skLineSegment(sketch, "E175", {"start": v(-36.5, -12.63) * mm, "end": v(-36.18, -12.63) * mm});
            skLineSegment(sketch, "E176", {"start": v(-36.18, -12.63) * mm, "end": v(-35.85, -12.63) * mm});
            skLineSegment(sketch, "E177", {"start": v(-35.85, -12.63) * mm, "end": v(-35.85, -12.42) * mm});
            skLineSegment(sketch, "E178", {"start": v(-35.85, -12.42) * mm, "end": v(-35.85, -12.2) * mm});
            skLineSegment(sketch, "E179", {"start": v(-35.85, -12.2) * mm, "end": v(-36.18, -12.2) * mm});
            skLineSegment(sketch, "E180", {"start": v(-36.18, -12.2) * mm, "end": v(-36.5, -12.2) * mm});
            skLineSegment(sketch, "E181", {"start": v(-36.5, -12.2) * mm, "end": v(-36.5, -11.88) * mm});
            skLineSegment(sketch, "E182", {"start": v(-36.5, -11.88) * mm, "end": v(-36.5, -11.56) * mm});
            skLineSegment(sketch, "E183", {"start": v(-36.5, -11.56) * mm, "end": v(-35.88, -11.56) * mm});
            skLineSegment(sketch, "E184", {"start": v(-35.88, -11.56) * mm, "end": v(-35.26, -11.56) * mm});
            skLineSegment(sketch, "E185", {"start": v(-35.26, -11.56) * mm, "end": v(-35.26, -11.35) * mm});
            skLineSegment(sketch, "E186", {"start": v(-35.26, -11.35) * mm, "end": v(-35.26, -11.13) * mm});
            skLineSegment(sketch, "E187", {"start": v(-35.26, -11.13) * mm, "end": v(-35.88, -11.13) * mm});
            skLineSegment(sketch, "E188", {"start": v(-35.88, -11.13) * mm, "end": v(-36.5, -11.13) * mm});
            skLineSegment(sketch, "E189", {"start": v(-36.5, -11.13) * mm, "end": v(-36.5, -10.99) * mm});
            skFitSpline(sketch, "E190", {"points": [v(-30.23, -2.77) * mm, v(-27.5, -2.77) * mm, v(-26.96, -2.73) * mm, v(-25.98, -2.48) * mm]});
            skFitSpline(sketch, "E191", {"points": [v(-25.98, -2.48) * mm, v(-23.65, -1.87) * mm, v(-22.1, -0.51) * mm, v(-21.59, 1.38) * mm]});
            skFitSpline(sketch, "E192", {"points": [v(-21.59, 1.38) * mm, v(-21.42, 2.02) * mm, v(-21.41, 3.43) * mm, v(-21.59, 4.1) * mm]});
            skFitSpline(sketch, "E193", {"points": [v(-21.59, 4.1) * mm, v(-22.1, 6.18) * mm, v(-23.77, 7.61) * mm, v(-26.37, 8.21) * mm]});
            skFitSpline(sketch, "E194", {"points": [v(-26.37, 8.21) * mm, v(-27.23, 8.41) * mm, v(-27.74, 8.43) * mm, v(-32.42, 8.43) * mm]});
            skLineSegment(sketch, "E195", {"start": v(-36.35, -10.7) * mm, "end": v(-36.2, -10.54) * mm});
            skLineSegment(sketch, "E196", {"start": v(-36.2, -10.54) * mm, "end": v(-34.48, -10.54) * mm});
            skLineSegment(sketch, "E197", {"start": v(-34.48, -10.54) * mm, "end": v(-32.75, -10.54) * mm});
            skLineSegment(sketch, "E198", {"start": v(-32.75, -10.54) * mm, "end": v(-32.75, -6.66) * mm});
            skLineSegment(sketch, "E199", {"start": v(-32.75, -6.66) * mm, "end": v(-32.75, -2.77) * mm});
            skLineSegment(sketch, "E200", {"start": v(-32.75, -2.77) * mm, "end": v(-30.23, -2.77) * mm});
            skFitSpline(sketch, "E201", {"points": [v(-37.14, -6.7) * mm, v(-37.34, -6.89) * mm, v(-37.38, -7.1) * mm, v(-37.28, -7.34) * mm]});
            skFitSpline(sketch, "E202", {"points": [v(-37.28, -7.34) * mm, v(-37.2, -7.54) * mm, v(-36.97, -7.7) * mm, v(-36.76, -7.7) * mm]});
            skFitSpline(sketch, "E203", {"points": [v(-36.76, -7.7) * mm, v(-36.48, -7.7) * mm, v(-36.18, -7.4) * mm, v(-36.18, -7.11) * mm]});
            skFitSpline(sketch, "E204", {"points": [v(-36.18, -7.11) * mm, v(-36.18, -6.95) * mm, v(-36.32, -6.7) * mm, v(-36.44, -6.63) * mm]});
            skFitSpline(sketch, "E205", {"points": [v(-36.44, -6.63) * mm, v(-36.55, -6.57) * mm, v(-36.55, -6.5) * mm, v(-36.55, 0.72) * mm]});
            skLineSegment(sketch, "E206", {"start": v(-32.42, 8.43) * mm, "end": v(-36.98, 8.43) * mm});
            skLineSegment(sketch, "E207", {"start": v(-36.98, 8.43) * mm, "end": v(-36.98, 0.94) * mm});
            skLineSegment(sketch, "E208", {"start": v(-36.98, 0.94) * mm, "end": v(-36.98, -6.55) * mm});
            skLineSegment(sketch, "E209", {"start": v(-36.98, -6.55) * mm, "end": v(-37.14, -6.7) * mm});
            skFitSpline(sketch, "E210", {"points": [v(-31.93, 7.99) * mm, v(-26.75, 7.97) * mm, v(-26.89, 7.98) * mm, v(-25.66, 7.57) * mm]});
            skFitSpline(sketch, "E211", {"points": [v(-25.66, 7.57) * mm, v(-24.26, 7.1) * mm, v(-23.29, 6.43) * mm, v(-22.65, 5.46) * mm]});
            skFitSpline(sketch, "E212", {"points": [v(-22.65, 5.46) * mm, v(-22.07, 4.6) * mm, v(-21.9, 3.92) * mm, v(-21.9, 2.67) * mm]});
            skFitSpline(sketch, "E213", {"points": [v(-21.9, 2.67) * mm, v(-21.9, 1.9) * mm, v(-21.92, 1.76) * mm, v(-22.05, 1.34) * mm]});
            skFitSpline(sketch, "E214", {"points": [v(-22.05, 1.34) * mm, v(-22.21, 0.78) * mm, v(-22.38, 0.43) * mm, v(-22.7, -0.01) * mm]});
            skFitSpline(sketch, "E215", {"points": [v(-22.7, -0.01) * mm, v(-23.57, -1.25) * mm, v(-25.29, -2.07) * mm, v(-27.43, -2.29) * mm]});
            skFitSpline(sketch, "E216", {"points": [v(-27.43, -2.29) * mm, v(-27.74, -2.32) * mm, v(-29.15, -2.34) * mm, v(-30.58, -2.34) * mm]});
            skLineSegment(sketch, "E217", {"start": v(-36.55, 0.72) * mm, "end": v(-36.55, 8) * mm});
            skLineSegment(sketch, "E218", {"start": v(-36.55, 8) * mm, "end": v(-31.93, 7.99) * mm});
            skFitSpline(sketch, "E219", {"points": [v(-36.37, -9.9) * mm, v(-36.7, -9.61) * mm, v(-37.14, -9.72) * mm, v(-37.3, -10.1) * mm]});
            skFitSpline(sketch, "E220", {"points": [v(-37.3, -10.1) * mm, v(-37.39, -10.32) * mm, v(-37.33, -10.52) * mm, v(-37.14, -10.71) * mm]});
            skFitSpline(sketch, "E221", {"points": [v(-37.14, -10.71) * mm, v(-37.05, -10.8) * mm, v(-36.98, -10.93) * mm, v(-36.98, -11) * mm]});
            skLineSegment(sketch, "E222", {"start": v(-30.58, -2.34) * mm, "end": v(-33.17, -2.34) * mm});
            skLineSegment(sketch, "E223", {"start": v(-33.17, -2.34) * mm, "end": v(-33.17, -6.2) * mm});
            skLineSegment(sketch, "E224", {"start": v(-33.17, -6.2) * mm, "end": v(-33.17, -10.06) * mm});
            skLineSegment(sketch, "E225", {"start": v(-33.17, -10.06) * mm, "end": v(-34.68, -10.06) * mm});
            skLineSegment(sketch, "E226", {"start": v(-34.68, -10.06) * mm, "end": v(-36.19, -10.06) * mm});
            skLineSegment(sketch, "E227", {"start": v(-36.19, -10.06) * mm, "end": v(-36.37, -9.9) * mm});
            skFitSpline(sketch, "E228", {"points": [v(-31.73, -10.82) * mm, v(-32.02, -10.53) * mm, v(-31.99, -9.96) * mm, v(-31.67, -9.73) * mm]});
            skLineSegment(sketch, "E229", {"start": v(-36.98, -11) * mm, "end": v(-36.98, -11.13) * mm});
            skLineSegment(sketch, "E230", {"start": v(-36.98, -11.13) * mm, "end": v(-37.6, -11.13) * mm});
            skLineSegment(sketch, "E231", {"start": v(-37.6, -11.13) * mm, "end": v(-38.21, -11.13) * mm});
            skLineSegment(sketch, "E232", {"start": v(-38.21, -11.13) * mm, "end": v(-38.21, -11.35) * mm});
            skLineSegment(sketch, "E233", {"start": v(-38.21, -11.35) * mm, "end": v(-38.21, -11.56) * mm});
            skLineSegment(sketch, "E234", {"start": v(-38.21, -11.56) * mm, "end": v(-37.6, -11.56) * mm});
            skLineSegment(sketch, "E235", {"start": v(-37.6, -11.56) * mm, "end": v(-36.98, -11.56) * mm});
            skLineSegment(sketch, "E236", {"start": v(-36.98, -11.56) * mm, "end": v(-36.98, -11.88) * mm});
            skLineSegment(sketch, "E237", {"start": v(-36.98, -11.88) * mm, "end": v(-36.98, -12.2) * mm});
            skLineSegment(sketch, "E238", {"start": v(-36.98, -12.2) * mm, "end": v(-37.3, -12.2) * mm});
            skLineSegment(sketch, "E239", {"start": v(-37.3, -12.2) * mm, "end": v(-37.62, -12.2) * mm});
            skLineSegment(sketch, "E240", {"start": v(-37.62, -12.2) * mm, "end": v(-37.62, -12.42) * mm});
            skLineSegment(sketch, "E241", {"start": v(-37.62, -12.42) * mm, "end": v(-37.62, -12.63) * mm});
            skLineSegment(sketch, "E242", {"start": v(-37.62, -12.63) * mm, "end": v(-37.3, -12.63) * mm});
            skLineSegment(sketch, "E243", {"start": v(-37.3, -12.63) * mm, "end": v(-36.98, -12.63) * mm});
            skLineSegment(sketch, "E244", {"start": v(-36.98, -12.63) * mm, "end": v(-36.98, -12.85) * mm});
            skLineSegment(sketch, "E245", {"start": v(-36.98, -12.85) * mm, "end": v(-36.98, -13.06) * mm});
            skLineSegment(sketch, "E246", {"start": v(-36.98, -13.06) * mm, "end": v(-36.74, -13.06) * mm});
            skLineSegment(sketch, "E247", {"start": v(-36.74, -13.06) * mm, "end": v(-36.5, -13.06) * mm});
            skLineSegment(sketch, "E248", {"start": v(-36.5, -13.06) * mm, "end": v(-36.5, -12.85) * mm});
            skFitSpline(sketch, "E249", {"points": [v(-29.4, -4.27) * mm, v(-27.9, -4.27) * mm, v(-27.14, -4.25) * mm, v(-26.74, -4.2) * mm]});
            skFitSpline(sketch, "E250", {"points": [v(-26.74, -4.2) * mm, v(-23.6, -3.77) * mm, v(-21.26, -2.06) * mm, v(-20.45, 0.4) * mm]});
            skFitSpline(sketch, "E251", {"points": [v(-20.45, 0.4) * mm, v(-20.2, 1.2) * mm, v(-20.13, 1.68) * mm, v(-20.13, 2.72) * mm]});
            skFitSpline(sketch, "E252", {"points": [v(-20.13, 2.72) * mm, v(-20.13, 3.78) * mm, v(-20.23, 4.4) * mm, v(-20.5, 5.17) * mm]});
            skFitSpline(sketch, "E253", {"points": [v(-20.5, 5.17) * mm, v(-21.38, 7.61) * mm, v(-23.6, 9.14) * mm, v(-26.85, 9.53) * mm]});
            skFitSpline(sketch, "E254", {"points": [v(-26.85, 9.53) * mm, v(-27.33, 9.59) * mm, v(-28.42, 9.6) * mm, v(-31.8, 9.6) * mm]});
            skFitSpline(sketch, "E255", {"points": [v(-31.8, 9.6) * mm, v(-36.06, 9.6) * mm, v(-36.12, 9.6) * mm, v(-36.18, 9.5) * mm]});
            skFitSpline(sketch, "E256", {"points": [v(-36.18, 9.5) * mm, v(-36.3, 9.26) * mm, v(-36.83, 9.15) * mm, v(-37.14, 9.31) * mm]});
            skFitSpline(sketch, "E257", {"points": [v(-37.14, 9.31) * mm, v(-37.55, 9.53) * mm, v(-37.56, 10.3) * mm, v(-37.14, 10.54) * mm]});
            skFitSpline(sketch, "E258", {"points": [v(-37.14, 10.54) * mm, v(-36.85, 10.71) * mm, v(-36.31, 10.61) * mm, v(-36.18, 10.36) * mm]});
            skFitSpline(sketch, "E259", {"points": [v(-36.18, 10.36) * mm, v(-36.12, 10.25) * mm, v(-36.06, 10.25) * mm, v(-31.62, 10.25) * mm]});
            skFitSpline(sketch, "E260", {"points": [v(-31.62, 10.25) * mm, v(-26.74, 10.25) * mm, v(-26.47, 10.24) * mm, v(-25.3, 9.95) * mm]});
            skFitSpline(sketch, "E261", {"points": [v(-25.3, 9.95) * mm, v(-22.94, 9.37) * mm, v(-21.1, 8.02) * mm, v(-20.19, 6.2) * mm]});
            skFitSpline(sketch, "E262", {"points": [v(-20.19, 6.2) * mm, v(-19.73, 5.29) * mm, v(-19.5, 4.29) * mm, v(-19.47, 2.96) * mm]});
            skFitSpline(sketch, "E263", {"points": [v(-19.47, 2.96) * mm, v(-19.42, 1.4) * mm, v(-19.62, 0.39) * mm, v(-20.18, -0.76) * mm]});
            skFitSpline(sketch, "E264", {"points": [v(-20.18, -0.76) * mm, v(-21.1, -2.66) * mm, v(-22.85, -3.98) * mm, v(-25.33, -4.62) * mm]});
            skFitSpline(sketch, "E265", {"points": [v(-25.33, -4.62) * mm, v(-26.28, -4.87) * mm, v(-26.87, -4.91) * mm, v(-28.94, -4.91) * mm]});
            skLineSegment(sketch, "E266", {"start": v(-31.67, -9.73) * mm, "end": v(-31.51, -9.61) * mm});
            skLineSegment(sketch, "E267", {"start": v(-31.51, -9.61) * mm, "end": v(-31.51, -6.94) * mm});
            skLineSegment(sketch, "E268", {"start": v(-31.51, -6.94) * mm, "end": v(-31.51, -4.27) * mm});
            skLineSegment(sketch, "E269", {"start": v(-31.51, -4.27) * mm, "end": v(-29.4, -4.27) * mm});
            skFitSpline(sketch, "E270", {"points": [v(-30.87, -7.3) * mm, v(-30.87, -9.4) * mm, v(-30.86, -9.7) * mm, v(-30.79, -9.72) * mm]});
            skFitSpline(sketch, "E271", {"points": [v(-30.79, -9.72) * mm, v(-30.66, -9.77) * mm, v(-30.55, -10.03) * mm, v(-30.55, -10.3) * mm]});
            skFitSpline(sketch, "E272", {"points": [v(-30.55, -10.3) * mm, v(-30.55, -10.78) * mm, v(-30.75, -10.97) * mm, v(-31.27, -10.97) * mm]});
            skFitSpline(sketch, "E273", {"points": [v(-31.27, -10.97) * mm, v(-31.53, -10.97) * mm, v(-31.6, -10.95) * mm, v(-31.73, -10.82) * mm]});
            skLineSegment(sketch, "E274", {"start": v(-28.94, -4.91) * mm, "end": v(-30.87, -4.91) * mm});
            skLineSegment(sketch, "E275", {"start": v(-30.87, -4.91) * mm, "end": v(-30.87, -7.3) * mm});
            skFitSpline(sketch, "E276", {"points": [v(-30.93, -10.79) * mm, v(-30.77, -10.7) * mm, v(-30.66, -10.5) * mm, v(-30.66, -10.3) * mm]});
            skFitSpline(sketch, "E277", {"points": [v(-30.66, -10.3) * mm, v(-30.66, -10.13) * mm, v(-30.79, -9.87) * mm, v(-30.9, -9.83) * mm]});
            skFitSpline(sketch, "E278", {"points": [v(-30.9, -9.83) * mm, v(-30.97, -9.8) * mm, v(-30.98, -9.5) * mm, v(-30.98, -7.3) * mm]});
            skFitSpline(sketch, "E279", {"points": [v(-29.05, -4.8) * mm, v(-26.97, -4.8) * mm, v(-26.38, -4.76) * mm, v(-25.44, -4.51) * mm]});
            skFitSpline(sketch, "E280", {"points": [v(-25.44, -4.51) * mm, v(-23.88, -4.1) * mm, v(-22.64, -3.46) * mm, v(-21.67, -2.54) * mm]});
            skFitSpline(sketch, "E281", {"points": [v(-21.67, -2.54) * mm, v(-21.07, -1.97) * mm, v(-20.64, -1.4) * mm, v(-20.28, -0.66) * mm]});
            skFitSpline(sketch, "E282", {"points": [v(-20.28, -0.66) * mm, v(-19.73, 0.47) * mm, v(-19.53, 1.52) * mm, v(-19.58, 2.96) * mm]});
            skFitSpline(sketch, "E283", {"points": [v(-19.58, 2.96) * mm, v(-19.65, 5) * mm, v(-20.26, 6.5) * mm, v(-21.52, 7.76) * mm]});
            skFitSpline(sketch, "E284", {"points": [v(-21.52, 7.76) * mm, v(-22.75, 9) * mm, v(-24.53, 9.8) * mm, v(-26.6, 10.06) * mm]});
            skFitSpline(sketch, "E285", {"points": [v(-26.6, 10.06) * mm, v(-27.12, 10.13) * mm, v(-28.02, 10.15) * mm, v(-31.7, 10.15) * mm]});
            skLineSegment(sketch, "E286", {"start": v(-30.98, -7.3) * mm, "end": v(-30.98, -4.8) * mm});
            skLineSegment(sketch, "E287", {"start": v(-30.98, -4.8) * mm, "end": v(-29.05, -4.8) * mm});
            skFitSpline(sketch, "E288", {"points": [v(-36.33, 10.3) * mm, v(-36.5, 10.48) * mm, v(-36.7, 10.55) * mm, v(-36.9, 10.5) * mm]});
            skFitSpline(sketch, "E289", {"points": [v(-36.9, 10.5) * mm, v(-37.07, 10.46) * mm, v(-37.29, 10.22) * mm, v(-37.33, 10.04) * mm]});
            skFitSpline(sketch, "E290", {"points": [v(-37.33, 10.04) * mm, v(-37.4, 9.72) * mm, v(-37.09, 9.34) * mm, v(-36.76, 9.34) * mm]});
            skFitSpline(sketch, "E291", {"points": [v(-36.76, 9.34) * mm, v(-36.6, 9.34) * mm, v(-36.35, 9.48) * mm, v(-36.28, 9.61) * mm]});
            skFitSpline(sketch, "E292", {"points": [v(-36.28, 9.61) * mm, v(-36.23, 9.72) * mm, v(-36.16, 9.72) * mm, v(-31.8, 9.72) * mm]});
            skFitSpline(sketch, "E293", {"points": [v(-31.8, 9.72) * mm, v(-27.2, 9.71) * mm, v(-26.75, 9.7) * mm, v(-25.72, 9.48) * mm]});
            skFitSpline(sketch, "E294", {"points": [v(-25.72, 9.48) * mm, v(-24.57, 9.23) * mm, v(-23.3, 8.7) * mm, v(-22.52, 8.12) * mm]});
            skFitSpline(sketch, "E295", {"points": [v(-22.52, 8.12) * mm, v(-21.24, 7.17) * mm, v(-20.5, 5.98) * mm, v(-20.14, 4.34) * mm]});
            skFitSpline(sketch, "E296", {"points": [v(-20.14, 4.34) * mm, v(-19.98, 3.6) * mm, v(-19.97, 1.9) * mm, v(-20.11, 1.19) * mm]});
            skFitSpline(sketch, "E297", {"points": [v(-20.11, 1.19) * mm, v(-20.6, -1.24) * mm, v(-22.16, -2.95) * mm, v(-24.68, -3.84) * mm]});
            skFitSpline(sketch, "E298", {"points": [v(-24.68, -3.84) * mm, v(-25.97, -4.3) * mm, v(-26.66, -4.38) * mm, v(-29.3, -4.38) * mm]});
            skLineSegment(sketch, "E299", {"start": v(-31.7, 10.15) * mm, "end": v(-36.19, 10.15) * mm});
            skLineSegment(sketch, "E300", {"start": v(-36.19, 10.15) * mm, "end": v(-36.33, 10.3) * mm});
            skLineSegment(sketch, "E301", {"start": v(-36.33, 10.3) * mm, "end": v(-31.7, 10.15) * mm});
            skFitSpline(sketch, "E302", {"points": [v(-31.54, -9.82) * mm, v(-31.75, -9.95) * mm, v(-31.85, -10.24) * mm, v(-31.78, -10.46) * mm]});
            skFitSpline(sketch, "E303", {"points": [v(-31.78, -10.46) * mm, v(-31.66, -10.82) * mm, v(-31.28, -10.97) * mm, v(-30.93, -10.79) * mm]});
            skLineSegment(sketch, "E304", {"start": v(-29.3, -4.38) * mm, "end": v(-31.4, -4.38) * mm});
            skLineSegment(sketch, "E305", {"start": v(-31.4, -4.38) * mm, "end": v(-31.4, -7.05) * mm});
            skLineSegment(sketch, "E306", {"start": v(-31.4, -7.05) * mm, "end": v(-31.4, -9.73) * mm});
            skLineSegment(sketch, "E307", {"start": v(-31.4, -9.73) * mm, "end": v(-31.54, -9.82) * mm});
            skFitSpline(sketch, "E308", {"points": [v(-18.5, -10.59) * mm, v(-18.53, -10.37) * mm, v(-18.57, -8.26) * mm, v(-18.6, -5.9) * mm]});
            skFitSpline(sketch, "E309", {"points": [v(-18.6, -5.9) * mm, v(-18.63, -3.55) * mm, v(-18.66, -1.4) * mm, v(-18.68, -1.12) * mm]});
            skFitSpline(sketch, "E310", {"points": [v(-18.68, -1.12) * mm, v(-18.7, -0.73) * mm, v(-18.7, -0.63) * mm, v(-18.64, -0.63) * mm]});
            skFitSpline(sketch, "E311", {"points": [v(-18.64, -0.63) * mm, v(-18.55, -0.63) * mm, v(-8.47, -10.7) * mm, v(-8.47, -10.8) * mm]});
            skFitSpline(sketch, "E312", {"points": [v(-8.47, -10.8) * mm, v(-8.47, -10.83) * mm, v(-8.6, -10.87) * mm, v(-8.78, -10.89) * mm]});
            skFitSpline(sketch, "E313", {"points": [v(-8.78, -10.89) * mm, v(-8.95, -10.9) * mm, v(-11.2, -10.93) * mm, v(-13.78, -10.95) * mm]});
            skLineSegment(sketch, "E314", {"start": v(-13.78, -10.95) * mm, "end": v(-18.48, -10.98) * mm});
            skLineSegment(sketch, "E315", {"start": v(-18.48, -10.98) * mm, "end": v(-18.5, -10.59) * mm});
            skLineSegment(sketch, "E316", {"start": v(-18.5, -10.59) * mm, "end": v(-13.78, -10.95) * mm});
            skFitSpline(sketch, "E317", {"points": [v(-13.64, -5.78) * mm, v(-18.41, -1) * mm, v(-18.59, -0.83) * mm, v(-18.57, -1.03) * mm]});
            skFitSpline(sketch, "E318", {"points": [v(-18.57, -1.03) * mm, v(-18.56, -1.15) * mm, v(-18.52, -3.23) * mm, v(-18.49, -5.66) * mm]});
            skFitSpline(sketch, "E319", {"points": [v(-18.49, -5.66) * mm, v(-18.46, -8.1) * mm, v(-18.42, -10.26) * mm, v(-18.4, -10.48) * mm]});
            skLineSegment(sketch, "E320", {"start": v(-8.94, -10.77) * mm, "end": v(-8.68, -10.73) * mm});
            skLineSegment(sketch, "E321", {"start": v(-8.68, -10.73) * mm, "end": v(-13.64, -5.78) * mm});
            skLineSegment(sketch, "E322", {"start": v(-13.64, -5.78) * mm, "end": v(-8.94, -10.77) * mm});
            skFitSpline(sketch, "E323", {"points": [v(-13.78, -10.84) * mm, v(-11.26, -10.83) * mm, v(-9.08, -10.8) * mm, v(-8.94, -10.77) * mm]});
            skLineSegment(sketch, "E324", {"start": v(-18.4, -10.48) * mm, "end": v(-18.37, -10.87) * mm});
            skLineSegment(sketch, "E325", {"start": v(-18.37, -10.87) * mm, "end": v(-13.78, -10.84) * mm});
            skLineSegment(sketch, "E326", {"start": v(-13.78, -10.84) * mm, "end": v(-18.4, -10.48) * mm});
            skFitSpline(sketch, "E327", {"points": [v(-13.12, -5.87) * mm, v(-15.8, -3.18) * mm, v(-18, -0.94) * mm, v(-18, -0.9) * mm]});
            skFitSpline(sketch, "E328", {"points": [v(-18, -0.9) * mm, v(-18, -0.87) * mm, v(-17.98, -0.84) * mm, v(-17.94, -0.84) * mm]});
            skFitSpline(sketch, "E329", {"points": [v(-17.94, -0.84) * mm, v(-17.9, -0.84) * mm, v(-16.72, -1.32) * mm, v(-15.3, -1.9) * mm]});
            skFitSpline(sketch, "E330", {"points": [v(-12.7, -4.25) * mm, v(-12.68, -4.96) * mm, v(-12.66, -5.58) * mm, v(-12.66, -5.63) * mm]});
            skFitSpline(sketch, "E331", {"points": [v(-12.66, -5.63) * mm, v(-12.65, -5.73) * mm, v(-12.6, -5.73) * mm, v(-11.08, -5.7) * mm]});
            skFitSpline(sketch, "E332", {"points": [v(-11.08, -5.7) * mm, v(-9.35, -5.67) * mm, v(-8.9, -5.62) * mm, v(-8.02, -5.33) * mm]});
            skFitSpline(sketch, "E333", {"points": [v(-8.02, -5.33) * mm, v(-7.56, -5.18) * mm, v(-7.47, -5.17) * mm, v(-7.32, -5.22) * mm]});
            skFitSpline(sketch, "E334", {"points": [v(-7.32, -5.22) * mm, v(-7.23, -5.26) * mm, v(-5.88, -5.81) * mm, v(-4.33, -6.45) * mm]});
            skFitSpline(sketch, "E335", {"points": [v(-4.33, -6.45) * mm, v(-1.88, -7.47) * mm, v(-1.5, -7.63) * mm, v(-1.51, -7.73) * mm]});
            skFitSpline(sketch, "E336", {"points": [v(-1.51, -7.73) * mm, v(-1.53, -7.86) * mm, v(-2.21, -8.45) * mm, v(-2.8, -8.84) * mm]});
            skFitSpline(sketch, "E337", {"points": [v(-2.8, -8.84) * mm, v(-4.06, -9.68) * mm, v(-5.54, -10.27) * mm, v(-7.23, -10.63) * mm]});
            skFitSpline(sketch, "E338", {"points": [v(-7.23, -10.63) * mm, v(-7.57, -10.7) * mm, v(-7.94, -10.76) * mm, v(-8.04, -10.76) * mm]});
            skFitSpline(sketch, "E339", {"points": [v(-8.04, -10.76) * mm, v(-8.22, -10.76) * mm, v(-8.49, -10.5) * mm, v(-13.12, -5.87) * mm]});
            skLineSegment(sketch, "E340", {"start": v(-15.3, -1.9) * mm, "end": v(-12.73, -2.98) * mm});
            skLineSegment(sketch, "E341", {"start": v(-12.73, -2.98) * mm, "end": v(-12.7, -4.25) * mm});
            skFitSpline(sketch, "E342", {"points": [v(-7.34, -10.52) * mm, v(-5.23, -10.08) * mm, v(-3.4, -9.24) * mm, v(-2.06, -8.1) * mm]});
            skFitSpline(sketch, "E343", {"points": [v(-2.06, -8.1) * mm, v(-1.75, -7.83) * mm, v(-1.67, -7.73) * mm, v(-1.73, -7.7) * mm]});
            skFitSpline(sketch, "E344", {"points": [v(-1.73, -7.7) * mm, v(-1.77, -7.67) * mm, v(-3.08, -7.12) * mm, v(-4.65, -6.48) * mm]});
            skFitSpline(sketch, "E345", {"points": [v(-7.94, -5.45) * mm, v(-8.75, -5.72) * mm, v(-9.25, -5.78) * mm, v(-11.08, -5.81) * mm]});
            skFitSpline(sketch, "E346", {"points": [v(-11.08, -5.81) * mm, v(-12.7, -5.84) * mm, v(-12.76, -5.84) * mm, v(-12.76, -5.74) * mm]});
            skFitSpline(sketch, "E347", {"points": [v(-12.76, -5.74) * mm, v(-12.77, -5.68) * mm, v(-12.78, -5.06) * mm, v(-12.8, -4.36) * mm]});
            skLineSegment(sketch, "E348", {"start": v(-4.65, -6.48) * mm, "end": v(-7.49, -5.3) * mm});
            skLineSegment(sketch, "E349", {"start": v(-7.49, -5.3) * mm, "end": v(-7.94, -5.45) * mm});
            skFitSpline(sketch, "E350", {"points": [v(-15.22, -2.1) * mm, v(-16.53, -1.55) * mm, v(-17.61, -1.1) * mm, v(-17.63, -1.1) * mm]});
            skFitSpline(sketch, "E351", {"points": [v(-17.63, -1.1) * mm, v(-17.65, -1.1) * mm, v(-15.51, -3.26) * mm, v(-12.89, -5.88) * mm]});
            skFitSpline(sketch, "E352", {"points": [v(-12.89, -5.88) * mm, v(-10.27, -8.5) * mm, v(-8.08, -10.65) * mm, v(-8.04, -10.65) * mm]});
            skFitSpline(sketch, "E353", {"points": [v(-8.04, -10.65) * mm, v(-8, -10.65) * mm, v(-7.68, -10.59) * mm, v(-7.34, -10.52) * mm]});
            skLineSegment(sketch, "E354", {"start": v(-12.8, -4.36) * mm, "end": v(-12.84, -3.08) * mm});
            skLineSegment(sketch, "E355", {"start": v(-12.84, -3.08) * mm, "end": v(-15.22, -2.1) * mm});
            skFitSpline(sketch, "E356", {"points": [v(25.64, -10.18) * mm, v(25.5, -10.17) * mm, v(23.9, -10.07) * mm, v(22.1, -9.95) * mm]});
            skFitSpline(sketch, "E357", {"points": [v(22.1, -9.95) * mm, v(20.31, -9.83) * mm, v(18.84, -9.73) * mm, v(18.83, -9.72) * mm]});
            skFitSpline(sketch, "E358", {"points": [v(18.83, -9.72) * mm, v(18.82, -9.71) * mm, v(18.74, -8.67) * mm, v(18.64, -7.4) * mm]});
            skFitSpline(sketch, "E359", {"points": [v(18.26, -5.39) * mm, v(17.81, -6.04) * mm, v(17.15, -6.6) * mm, v(16.43, -6.97) * mm]});
            skFitSpline(sketch, "E360", {"points": [v(16.43, -6.97) * mm, v(16.22, -7.07) * mm, v(15.28, -7.47) * mm, v(14.34, -7.86) * mm]});
            skFitSpline(sketch, "E361", {"points": [v(14.34, -7.86) * mm, v(13.4, -8.25) * mm, v(12.37, -8.68) * mm, v(12.07, -8.81) * mm]});
            skFitSpline(sketch, "E362", {"points": [v(12.07, -8.81) * mm, v(11.76, -8.94) * mm, v(11.23, -9.13) * mm, v(10.89, -9.22) * mm]});
            skFitSpline(sketch, "E363", {"points": [v(10.89, -9.22) * mm, v(10.28, -9.38) * mm, v(10.23, -9.38) * mm, v(9.06, -9.39) * mm]});
            skFitSpline(sketch, "E364", {"points": [v(9.06, -9.39) * mm, v(7.99, -9.39) * mm, v(7.79, -9.38) * mm, v(7.26, -9.26) * mm]});
            skFitSpline(sketch, "E365", {"points": [v(7.26, -9.26) * mm, v(5.88, -8.97) * mm, v(4.32, -8.3) * mm, v(3.27, -7.55) * mm]});
            skFitSpline(sketch, "E366", {"points": [v(3.27, -7.55) * mm, v(2.41, -6.94) * mm, v(1.2, -5.7) * mm, v(1.24, -5.48) * mm]});
            skFitSpline(sketch, "E367", {"points": [v(1.24, -5.48) * mm, v(1.25, -5.43) * mm, v(1.87, -4.67) * mm, v(2.61, -3.77) * mm]});
            skLineSegment(sketch, "E368", {"start": v(18.64, -7.4) * mm, "end": v(18.47, -5.08) * mm});
            skLineSegment(sketch, "E369", {"start": v(18.47, -5.08) * mm, "end": v(18.26, -5.39) * mm});
            skFitSpline(sketch, "E370", {"points": [v(6.02, -1.6) * mm, v(7.14, -1.29) * mm, v(8.1, -1.02) * mm, v(8.14, -1) * mm]});
            skLineSegment(sketch, "E371", {"start": v(2.61, -3.77) * mm, "end": v(3.96, -2.15) * mm});
            skLineSegment(sketch, "E372", {"start": v(3.96, -2.15) * mm, "end": v(6.02, -1.6) * mm});
            skFitSpline(sketch, "E373", {"points": [v(5.05, 0.2) * mm, v(4.9, 0.61) * mm, v(4.68, 1.26) * mm, v(4.56, 1.64) * mm]});
            skFitSpline(sketch, "E374", {"points": [v(4.56, 1.64) * mm, v(4.33, 2.31) * mm, v(4.33, 2.33) * mm, v(4.43, 2.44) * mm]});
            skFitSpline(sketch, "E375", {"points": [v(4.43, 2.44) * mm, v(4.48, 2.5) * mm, v(4.96, 3.03) * mm, v(5.5, 3.6) * mm]});
            skFitSpline(sketch, "E376", {"points": [v(8.55, 5.28) * mm, v(11, 6.01) * mm, v(10.54, 5.97) * mm, v(13.48, 5.8) * mm]});
            skFitSpline(sketch, "E377", {"points": [v(13.48, 5.8) * mm, v(14.54, 5.75) * mm, v(15.43, 5.7) * mm, v(15.45, 5.7) * mm]});
            skFitSpline(sketch, "E378", {"points": [v(15.45, 5.7) * mm, v(15.6, 5.7) * mm, v(15.4, 5.44) * mm, v(14.82, 4.83) * mm]});
            skFitSpline(sketch, "E379", {"points": [v(14.82, 4.83) * mm, v(14.45, 4.45) * mm, v(14.15, 4.12) * mm, v(14.15, 4.1) * mm]});
            skFitSpline(sketch, "E380", {"points": [v(14.15, 4.1) * mm, v(14.15, 4.08) * mm, v(14.28, 4.02) * mm, v(14.43, 3.96) * mm]});
            skFitSpline(sketch, "E381", {"points": [v(14.43, 3.96) * mm, v(14.96, 3.78) * mm, v(15.92, 3.3) * mm, v(16.46, 2.94) * mm]});
            skFitSpline(sketch, "E382", {"points": [v(16.46, 2.94) * mm, v(16.75, 2.75) * mm, v(17.2, 2.38) * mm, v(17.47, 2.13) * mm]});
            skFitSpline(sketch, "E383", {"points": [v(17.47, 2.13) * mm, v(17.74, 1.87) * mm, v(17.95, 1.68) * mm, v(17.95, 1.71) * mm]});
            skFitSpline(sketch, "E384", {"points": [v(17.95, 1.71) * mm, v(17.95, 1.74) * mm, v(17.8, 3.66) * mm, v(17.63, 5.98) * mm]});
            skFitSpline(sketch, "E385", {"points": [v(17.63, 5.98) * mm, v(17.46, 8.3) * mm, v(17.31, 10.25) * mm, v(17.31, 10.31) * mm]});
            skFitSpline(sketch, "E386", {"points": [v(17.31, 10.31) * mm, v(17.31, 10.37) * mm, v(17.35, 10.41) * mm, v(17.4, 10.41) * mm]});
            skFitSpline(sketch, "E387", {"points": [v(17.4, 10.41) * mm, v(17.46, 10.41) * mm, v(18.32, 10.72) * mm, v(19.31, 11.08) * mm]});
            skLineSegment(sketch, "E388", {"start": v(5.5, 3.6) * mm, "end": v(6.46, 4.65) * mm});
            skLineSegment(sketch, "E389", {"start": v(6.46, 4.65) * mm, "end": v(8.55, 5.28) * mm});
            skFitSpline(sketch, "E390", {"points": [v(24.08, 11.62) * mm, v(29.25, 11.38) * mm, v(29.19, 11.4) * mm, v(30.34, 11) * mm]});
            skFitSpline(sketch, "E391", {"points": [v(30.34, 11) * mm, v(32.37, 10.33) * mm, v(34.29, 9.1) * mm, v(35.6, 7.63) * mm]});
            skFitSpline(sketch, "E392", {"points": [v(35.6, 7.63) * mm, v(37.43, 5.6) * mm, v(38.33, 3.16) * mm, v(38.33, 0.15) * mm]});
            skFitSpline(sketch, "E393", {"points": [v(38.33, 0.15) * mm, v(38.33, -0.97) * mm, v(38.25, -1.58) * mm, v(37.96, -2.45) * mm]});
            skFitSpline(sketch, "E394", {"points": [v(37.96, -2.45) * mm, v(37.21, -4.74) * mm, v(35.35, -6.71) * mm, v(32.5, -8.21) * mm]});
            skFitSpline(sketch, "E395", {"points": [v(32.5, -8.21) * mm, v(32.18, -8.38) * mm, v(31.72, -8.64) * mm, v(31.49, -8.79) * mm]});
            skFitSpline(sketch, "E396", {"points": [v(31.49, -8.79) * mm, v(29.9, -9.79) * mm, v(27.68, -10.32) * mm, v(25.64, -10.18) * mm]});
            skLineSegment(sketch, "E397", {"start": v(19.31, 11.08) * mm, "end": v(21.12, 11.75) * mm});
            skLineSegment(sketch, "E398", {"start": v(21.12, 11.75) * mm, "end": v(24.08, 11.62) * mm});
            skFitSpline(sketch, "E399", {"points": [v(6.19, -0.5) * mm, v(7.95, -0.65) * mm, v(9.15, -1.04) * mm, v(9.76, -1.65) * mm]});
            skFitSpline(sketch, "E400", {"points": [v(9.76, -1.65) * mm, v(10.13, -2.02) * mm, v(10.38, -2.6) * mm, v(10.16, -2.6) * mm]});
            skFitSpline(sketch, "E401", {"points": [v(10.16, -2.6) * mm, v(10, -2.6) * mm, v(9.28, -2.07) * mm, v(8.65, -1.47) * mm]});
            skLineSegment(sketch, "E402", {"start": v(5.42, -0.44) * mm, "end": v(6.19, -0.5) * mm});
            skLineSegment(sketch, "E403", {"start": v(8.65, -1.47) * mm, "end": v(8.27, -1.11) * mm});
            skFitSpline(sketch, "E404", {"points": [v(24.92, -9.6) * mm, v(21.75, -9.39) * mm, v(19.4, -9.21) * mm, v(19.36, -9.18) * mm]});
            skFitSpline(sketch, "E405", {"points": [v(19.36, -9.18) * mm, v(19.32, -9.14) * mm, v(17.88, 9.77) * mm, v(17.92, 9.8) * mm]});
            skFitSpline(sketch, "E406", {"points": [v(17.92, 9.8) * mm, v(17.97, 9.86) * mm, v(24.45, 9.55) * mm, v(25, 9.48) * mm]});
            skFitSpline(sketch, "E407", {"points": [v(25, 9.48) * mm, v(26.18, 9.31) * mm, v(27.35, 8.98) * mm, v(28.41, 8.51) * mm]});
            skFitSpline(sketch, "E408", {"points": [v(28.41, 8.51) * mm, v(30.72, 7.49) * mm, v(32.53, 5.67) * mm, v(33.46, 3.43) * mm]});
            skFitSpline(sketch, "E409", {"points": [v(33.46, 3.43) * mm, v(34.11, 1.88) * mm, v(34.37, 0.46) * mm, v(34.37, -1.54) * mm]});
            skFitSpline(sketch, "E410", {"points": [v(34.37, -1.54) * mm, v(34.37, -2.9) * mm, v(34.3, -3.5) * mm, v(34, -4.51) * mm]});
            skFitSpline(sketch, "E411", {"points": [v(34, -4.51) * mm, v(33.82, -5.16) * mm, v(33.3, -6.2) * mm, v(32.9, -6.72) * mm]});
            skFitSpline(sketch, "E412", {"points": [v(32.9, -6.72) * mm, v(31.77, -8.23) * mm, v(29.92, -9.23) * mm, v(27.7, -9.55) * mm]});
            skFitSpline(sketch, "E413", {"points": [v(27.7, -9.55) * mm, v(27.19, -9.62) * mm, v(25.74, -9.64) * mm, v(24.92, -9.6) * mm]});
            skFitSpline(sketch, "E414", {"points": [v(24.43, -5.24) * mm, v(23.79, -5.2) * mm, v(23.25, -5.14) * mm, v(23.24, -5.13) * mm]});
            skFitSpline(sketch, "E415", {"points": [v(23.24, -5.13) * mm, v(23.21, -5.1) * mm, v(22.35, 4.86) * mm, v(22.35, 5.15) * mm]});
            skFitSpline(sketch, "E416", {"points": [v(22.9, 5.37) * mm, v(24.15, 5.37) * mm, v(25.26, 5.28) * mm, v(25.72, 5.17) * mm]});
            skFitSpline(sketch, "E417", {"points": [v(25.72, 5.17) * mm, v(26.76, 4.9) * mm, v(27.59, 4.45) * mm, v(28.28, 3.8) * mm]});
            skFitSpline(sketch, "E418", {"points": [v(28.28, 3.8) * mm, v(29.2, 2.94) * mm, v(29.7, 1.97) * mm, v(29.93, 0.63) * mm]});
            skFitSpline(sketch, "E419", {"points": [v(29.93, 0.63) * mm, v(30.06, -0.1) * mm, v(30.06, -1.5) * mm, v(29.94, -2.15) * mm]});
            skFitSpline(sketch, "E420", {"points": [v(29.94, -2.15) * mm, v(29.62, -3.79) * mm, v(28.78, -4.79) * mm, v(27.39, -5.18) * mm]});
            skFitSpline(sketch, "E421", {"points": [v(27.39, -5.18) * mm, v(26.83, -5.34) * mm, v(25.87, -5.36) * mm, v(24.43, -5.24) * mm]});
            skLineSegment(sketch, "E422", {"start": v(22.35, 5.15) * mm, "end": v(22.35, 5.38) * mm});
            skLineSegment(sketch, "E423", {"start": v(22.35, 5.38) * mm, "end": v(22.9, 5.37) * mm});
            skLineSegment(sketch, "E424", {"start": v(24.43, -5.24) * mm, "end": v(24.43, -5.24) * mm});
            skFitSpline(sketch, "E425", {"points": [v(27.42, 0.2) * mm, v(27.28, 2.2) * mm, v(27.17, 3.84) * mm, v(27.19, 3.86) * mm]});
            skFitSpline(sketch, "E426", {"points": [v(27.19, 3.86) * mm, v(27.32, 4) * mm, v(28.37, 3) * mm, v(28.72, 2.4) * mm]});
            skFitSpline(sketch, "E427", {"points": [v(28.72, 2.4) * mm, v(29.02, 1.88) * mm, v(29.28, 1.13) * mm, v(29.4, 0.45) * mm]});
            skFitSpline(sketch, "E428", {"points": [v(29.4, 0.45) * mm, v(29.54, -0.4) * mm, v(29.49, -1.82) * mm, v(29.3, -2.47) * mm]});
            skFitSpline(sketch, "E429", {"points": [v(29.3, -2.47) * mm, v(29.22, -2.73) * mm, v(29.1, -3.06) * mm, v(29.02, -3.2) * mm]});
            skLineSegment(sketch, "E430", {"start": v(27.97, -3.43) * mm, "end": v(27.68, -3.4) * mm});
            skLineSegment(sketch, "E431", {"start": v(27.68, -3.4) * mm, "end": v(27.42, 0.2) * mm});
            skFitSpline(sketch, "E432", {"points": [v(28.58, -3.46) * mm, v(28.4, -3.45) * mm, v(28.14, -3.44) * mm, v(27.97, -3.43) * mm]});
            skLineSegment(sketch, "E433", {"start": v(29.02, -3.2) * mm, "end": v(28.88, -3.47) * mm});
            skLineSegment(sketch, "E434", {"start": v(28.88, -3.47) * mm, "end": v(28.58, -3.46) * mm});
            skFitSpline(sketch, "E435", {"points": [v(7.82, -8.8) * mm, v(6.19, -8.54) * mm, v(4.58, -7.85) * mm, v(3.3, -6.86) * mm]});
            skFitSpline(sketch, "E436", {"points": [v(3.3, -6.86) * mm, v(2.71, -6.4) * mm, v(1.98, -5.66) * mm, v(1.98, -5.52) * mm]});
            skFitSpline(sketch, "E437", {"points": [v(1.98, -5.52) * mm, v(1.98, -5.4) * mm, v(3.94, -3.02) * mm, v(4.06, -3) * mm]});
            skFitSpline(sketch, "E438", {"points": [v(4.06, -3) * mm, v(4.1, -2.98) * mm, v(4.33, -3.17) * mm, v(4.57, -3.4) * mm]});
            skFitSpline(sketch, "E439", {"points": [v(4.57, -3.4) * mm, v(5.9, -4.66) * mm, v(7.68, -5.32) * mm, v(9.09, -5.08) * mm]});
            skFitSpline(sketch, "E440", {"points": [v(9.09, -5.08) * mm, v(10.07, -4.9) * mm, v(10.59, -4.4) * mm, v(10.72, -3.47) * mm]});
            skFitSpline(sketch, "E441", {"points": [v(10.72, -3.47) * mm, v(10.89, -2.29) * mm, v(10.36, -1.36) * mm, v(9.2, -0.78) * mm]});
            skFitSpline(sketch, "E442", {"points": [v(9.2, -0.78) * mm, v(8.44, -0.4) * mm, v(7.76, -0.25) * mm, v(6.06, -0.05) * mm]});
            skFitSpline(sketch, "E443", {"points": [v(6.99, 4.09) * mm, v(7.33, 4.09) * mm, v(10.02, 3.93) * mm, v(10.33, 3.9) * mm]});
            skFitSpline(sketch, "E444", {"points": [v(10.33, 3.9) * mm, v(10.46, 3.88) * mm, v(10.56, 3.84) * mm, v(10.56, 3.8) * mm]});
            skFitSpline(sketch, "E445", {"points": [v(10.56, 3.8) * mm, v(10.56, 3.77) * mm, v(10.25, 3.44) * mm, v(9.88, 3.07) * mm]});
            skLineSegment(sketch, "E446", {"start": v(6.06, -0.05) * mm, "end": v(5.7, -0.01) * mm});
            skLineSegment(sketch, "E447", {"start": v(5.7, -0.01) * mm, "end": v(5.33, 1.1) * mm});
            skLineSegment(sketch, "E448", {"start": v(5.33, 1.1) * mm, "end": v(4.96, 2.2) * mm});
            skLineSegment(sketch, "E449", {"start": v(4.96, 2.2) * mm, "end": v(5.83, 3.14) * mm});
            skLineSegment(sketch, "E450", {"start": v(5.83, 3.14) * mm, "end": v(6.7, 4.09) * mm});
            skLineSegment(sketch, "E451", {"start": v(6.7, 4.09) * mm, "end": v(6.99, 4.09) * mm});
            skFitSpline(sketch, "E452", {"points": [v(9.59, 2.33) * mm, v(10.13, 2.24) * mm, v(10.78, 2.02) * mm, v(11.33, 1.75) * mm]});
            skFitSpline(sketch, "E453", {"points": [v(11.33, 1.75) * mm, v(12.72, 1.07) * mm, v(13.68, 0) * mm, v(14.18, -1.4) * mm]});
            skFitSpline(sketch, "E454", {"points": [v(14.18, -1.4) * mm, v(14.47, -2.22) * mm, v(14.55, -2.72) * mm, v(14.54, -3.82) * mm]});
            skFitSpline(sketch, "E455", {"points": [v(14.54, -3.82) * mm, v(14.54, -4.68) * mm, v(14.53, -4.84) * mm, v(14.4, -5.3) * mm]});
            skFitSpline(sketch, "E456", {"points": [v(14.4, -5.3) * mm, v(13.97, -6.94) * mm, v(12.8, -8.08) * mm, v(11.04, -8.6) * mm]});
            skFitSpline(sketch, "E457", {"points": [v(11.04, -8.6) * mm, v(10.06, -8.88) * mm, v(8.83, -8.96) * mm, v(7.82, -8.8) * mm]});
            skLineSegment(sketch, "E458", {"start": v(9.88, 3.07) * mm, "end": v(9.2, 2.4) * mm});
            skLineSegment(sketch, "E459", {"start": v(9.2, 2.4) * mm, "end": v(9.59, 2.33) * mm});
            skLineSegment(sketch, "E460", {"start": v(7.82, -8.8) * mm, "end": v(7.82, -8.8) * mm});
            skFitSpline(sketch, "E461", {"points": [v(11.21, 4.29) * mm, v(11.13, 4.3) * mm, v(11.1, 4.34) * mm, v(11.1, 4.4) * mm]});
            skFitSpline(sketch, "E462", {"points": [v(11.1, 4.4) * mm, v(11.13, 4.52) * mm, v(11.63, 4.57) * mm, v(11.63, 4.45) * mm]});
            skFitSpline(sketch, "E463", {"points": [v(11.63, 4.45) * mm, v(11.63, 4.28) * mm, v(11.5, 4.23) * mm, v(11.21, 4.29) * mm]});
            skFitSpline(sketch, "E464", {"points": [v(10.5, 4.35) * mm, v(10.5, 4.51) * mm, v(10.58, 4.57) * mm, v(10.78, 4.57) * mm]});
            skFitSpline(sketch, "E465", {"points": [v(10.78, 4.57) * mm, v(11, 4.57) * mm, v(11.05, 4.5) * mm, v(10.92, 4.37) * mm]});
            skFitSpline(sketch, "E466", {"points": [v(10.92, 4.37) * mm, v(10.85, 4.3) * mm, v(10.5, 4.28) * mm, v(10.5, 4.35) * mm]});
            skFitSpline(sketch, "E467", {"points": [v(9.97, 4.42) * mm, v(9.97, 4.54) * mm, v(10.09, 4.63) * mm, v(10.25, 4.63) * mm]});
            skFitSpline(sketch, "E468", {"points": [v(10.25, 4.63) * mm, v(10.38, 4.63) * mm, v(10.4, 4.6) * mm, v(10.39, 4.5) * mm]});
            skFitSpline(sketch, "E469", {"points": [v(10.39, 4.5) * mm, v(10.37, 4.4) * mm, v(10.33, 4.38) * mm, v(10.17, 4.37) * mm]});
            skFitSpline(sketch, "E470", {"points": [v(10.17, 4.37) * mm, v(10.03, 4.36) * mm, v(9.97, 4.37) * mm, v(9.97, 4.42) * mm]});
            skFitSpline(sketch, "E471", {"points": [v(11.8, 4.44) * mm, v(11.8, 4.48) * mm, v(11.84, 4.52) * mm, v(11.9, 4.52) * mm]});
            skFitSpline(sketch, "E472", {"points": [v(11.9, 4.52) * mm, v(11.96, 4.52) * mm, v(12, 4.48) * mm, v(12, 4.44) * mm]});
            skFitSpline(sketch, "E473", {"points": [v(12, 4.44) * mm, v(12, 4.4) * mm, v(11.96, 4.36) * mm, v(11.9, 4.36) * mm]});
            skFitSpline(sketch, "E474", {"points": [v(11.9, 4.36) * mm, v(11.84, 4.36) * mm, v(11.8, 4.4) * mm, v(11.8, 4.44) * mm]});
            skFitSpline(sketch, "E475", {"points": [v(8.9, 4.6) * mm, v(8.9, 4.67) * mm, v(9.1, 4.79) * mm, v(9.22, 4.79) * mm]});
            skFitSpline(sketch, "E476", {"points": [v(9.22, 4.79) * mm, v(9.33, 4.79) * mm, v(9.26, 4.62) * mm, v(9.13, 4.57) * mm]});
            skFitSpline(sketch, "E477", {"points": [v(9.13, 4.57) * mm, v(8.95, 4.5) * mm, v(8.9, 4.5) * mm, v(8.9, 4.6) * mm]});
            skFitSpline(sketch, "E478", {"points": [v(12.1, 4.6) * mm, v(11.99, 4.64) * mm, v(11.98, 4.74) * mm, v(12.07, 4.83) * mm]});
            skFitSpline(sketch, "E479", {"points": [v(12.07, 4.83) * mm, v(12.15, 4.9) * mm, v(12.54, 4.91) * mm, v(12.54, 4.84) * mm]});
            skFitSpline(sketch, "E480", {"points": [v(12.54, 4.84) * mm, v(12.54, 4.62) * mm, v(12.37, 4.54) * mm, v(12.1, 4.6) * mm]});
            skFitSpline(sketch, "E481", {"points": [v(11.36, 4.7) * mm, v(11.36, 4.83) * mm, v(11.55, 4.95) * mm, v(11.75, 4.95) * mm]});
            skFitSpline(sketch, "E482", {"points": [v(11.75, 4.95) * mm, v(11.96, 4.95) * mm, v(12, 4.88) * mm, v(11.88, 4.72) * mm]});
            skFitSpline(sketch, "E483", {"points": [v(11.88, 4.72) * mm, v(11.79, 4.6) * mm, v(11.36, 4.58) * mm, v(11.36, 4.7) * mm]});
            skFitSpline(sketch, "E484", {"points": [v(10.34, 4.73) * mm, v(10.22, 4.81) * mm, v(10.35, 4.97) * mm, v(10.55, 5) * mm]});
            skFitSpline(sketch, "E485", {"points": [v(10.55, 5) * mm, v(10.73, 5) * mm, v(10.76, 4.96) * mm, v(10.66, 4.78) * mm]});
            skFitSpline(sketch, "E486", {"points": [v(10.66, 4.78) * mm, v(10.6, 4.67) * mm, v(10.47, 4.65) * mm, v(10.34, 4.73) * mm]});
            skFitSpline(sketch, "E487", {"points": [v(10.83, 4.78) * mm, v(10.83, 4.93) * mm, v(10.94, 5) * mm, v(11.16, 5) * mm]});
            skFitSpline(sketch, "E488", {"points": [v(11.16, 5) * mm, v(11.39, 5) * mm, v(11.42, 4.91) * mm, v(11.26, 4.77) * mm]});
            skFitSpline(sketch, "E489", {"points": [v(11.26, 4.77) * mm, v(11.13, 4.64) * mm, v(10.83, 4.65) * mm, v(10.83, 4.78) * mm]});
            skFitSpline(sketch, "E490", {"points": [v(12.71, 4.77) * mm, v(12.73, 4.9) * mm, v(13.08, 4.94) * mm, v(13.08, 4.82) * mm]});
            skFitSpline(sketch, "E491", {"points": [v(13.08, 4.82) * mm, v(13.08, 4.78) * mm, v(13.02, 4.73) * mm, v(12.96, 4.71) * mm]});
            skFitSpline(sketch, "E492", {"points": [v(12.96, 4.71) * mm, v(12.76, 4.66) * mm, v(12.7, 4.67) * mm, v(12.71, 4.77) * mm]});
            skFitSpline(sketch, "E493", {"points": [v(13.06, 4.98) * mm, v(13, 5) * mm, v(12.97, 5.05) * mm, v(12.98, 5.13) * mm]});
            skFitSpline(sketch, "E494", {"points": [v(12.98, 5.13) * mm, v(13, 5.22) * mm, v(13.04, 5.24) * mm, v(13.25, 5.26) * mm]});
            skFitSpline(sketch, "E495", {"points": [v(13.25, 5.26) * mm, v(13.52, 5.28) * mm, v(13.57, 5.22) * mm, v(13.43, 5.04) * mm]});
            skFitSpline(sketch, "E496", {"points": [v(13.43, 5.04) * mm, v(13.36, 4.95) * mm, v(13.26, 4.93) * mm, v(13.06, 4.98) * mm]});
            skFitSpline(sketch, "E497", {"points": [v(12.33, 5.07) * mm, v(12.33, 5.21) * mm, v(12.47, 5.32) * mm, v(12.67, 5.32) * mm]});
            skFitSpline(sketch, "E498", {"points": [v(12.67, 5.32) * mm, v(12.82, 5.32) * mm, v(12.86, 5.3) * mm, v(12.86, 5.23) * mm]});
            skFitSpline(sketch, "E499", {"points": [v(12.86, 5.23) * mm, v(12.86, 5.17) * mm, v(12.83, 5.1) * mm, v(12.8, 5.06) * mm]});
            skFitSpline(sketch, "E500", {"points": [v(12.8, 5.06) * mm, v(12.71, 4.98) * mm, v(12.33, 4.98) * mm, v(12.33, 5.07) * mm]});
            skFitSpline(sketch, "E501", {"points": [v(13.62, 5.1) * mm, v(13.65, 5.22) * mm, v(13.99, 5.26) * mm, v(13.99, 5.14) * mm]});
            skFitSpline(sketch, "E502", {"points": [v(13.99, 5.14) * mm, v(13.99, 5.1) * mm, v(13.93, 5.05) * mm, v(13.87, 5.03) * mm]});
            skFitSpline(sketch, "E503", {"points": [v(13.87, 5.03) * mm, v(13.67, 4.98) * mm, v(13.6, 5) * mm, v(13.62, 5.1) * mm]});
            skFitSpline(sketch, "E504", {"points": [v(11.27, 5.1) * mm, v(11.02, 5.14) * mm, v(11.17, 5.38) * mm, v(11.45, 5.38) * mm]});
            skFitSpline(sketch, "E505", {"points": [v(11.45, 5.38) * mm, v(11.59, 5.38) * mm, v(11.63, 5.35) * mm, v(11.63, 5.28) * mm]});
            skFitSpline(sketch, "E506", {"points": [v(11.63, 5.28) * mm, v(11.63, 5.17) * mm, v(11.53, 5.05) * mm, v(11.44, 5.06) * mm]});
            skFitSpline(sketch, "E507", {"points": [v(11.44, 5.06) * mm, v(11.41, 5.07) * mm, v(11.33, 5.08) * mm, v(11.27, 5.1) * mm]});
            skFitSpline(sketch, "E508", {"points": [v(11.74, 5.1) * mm, v(11.74, 5.25) * mm, v(11.85, 5.38) * mm, v(12, 5.37) * mm]});
            skFitSpline(sketch, "E509", {"points": [v(12, 5.37) * mm, v(12.38, 5.37) * mm, v(12.35, 5.1) * mm, v(11.96, 5.06) * mm]});
            skFitSpline(sketch, "E510", {"points": [v(11.96, 5.06) * mm, v(11.82, 5.05) * mm, v(11.74, 5.07) * mm, v(11.74, 5.1) * mm]});
            skFitSpline(sketch, "E511", {"points": [v(10.61, 5.18) * mm, v(10.61, 5.3) * mm, v(10.8, 5.43) * mm, v(10.95, 5.43) * mm]});
            skFitSpline(sketch, "E512", {"points": [v(10.95, 5.43) * mm, v(11.12, 5.43) * mm, v(11.14, 5.33) * mm, v(11, 5.2) * mm]});
            skFitSpline(sketch, "E513", {"points": [v(11, 5.2) * mm, v(10.88, 5.09) * mm, v(10.61, 5.08) * mm, v(10.61, 5.18) * mm]});
            skFitSpline(sketch, "E514", {"points": [v(-4.27, -6.32) * mm, v(-5.87, -5.65) * mm, v(-7.18, -5.08) * mm, v(-7.18, -5.05) * mm]});
            skFitSpline(sketch, "E515", {"points": [v(-7.18, -5.05) * mm, v(-7.18, -5.01) * mm, v(-7.04, -4.9) * mm, v(-6.87, -4.78) * mm]});
            skFitSpline(sketch, "E516", {"points": [v(-6.87, -4.78) * mm, v(-5.74, -4.03) * mm, v(-5.07, -2.72) * mm, v(-4.9, -0.93) * mm]});
            skFitSpline(sketch, "E517", {"points": [v(1.2, -1.23) * mm, v(1.09, -3.38) * mm, v(0.6, -4.98) * mm, v(-0.37, -6.43) * mm]});
            skFitSpline(sketch, "E518", {"points": [v(-0.37, -6.43) * mm, v(-0.78, -7.04) * mm, v(-1.2, -7.54) * mm, v(-1.3, -7.54) * mm]});
            skFitSpline(sketch, "E519", {"points": [v(-1.3, -7.54) * mm, v(-1.34, -7.53) * mm, v(-2.68, -6.99) * mm, v(-4.27, -6.32) * mm]});
            skLineSegment(sketch, "E520", {"start": v(-4.9, -0.93) * mm, "end": v(-4.87, -0.57) * mm});
            skLineSegment(sketch, "E521", {"start": v(-4.87, -0.57) * mm, "end": v(-1.81, -0.57) * mm});
            skLineSegment(sketch, "E522", {"start": v(-1.81, -0.57) * mm, "end": v(1.25, -0.57) * mm});
            skLineSegment(sketch, "E523", {"start": v(1.25, -0.57) * mm, "end": v(1.2, -1.23) * mm});
            skFitSpline(sketch, "E524", {"points": [v(-1.01, -7.04) * mm, v(0.27, -5.51) * mm, v(0.94, -3.66) * mm, v(1.1, -1.2) * mm]});
            skFitSpline(sketch, "E525", {"points": [v(-4.8, -1.04) * mm, v(-4.95, -2.76) * mm, v(-5.54, -3.98) * mm, v(-6.6, -4.76) * mm]});
            skFitSpline(sketch, "E526", {"points": [v(-6.6, -4.76) * mm, v(-6.8, -4.92) * mm, v(-6.96, -5.05) * mm, v(-6.93, -5.06) * mm]});
            skFitSpline(sketch, "E527", {"points": [v(-6.93, -5.06) * mm, v(-6.9, -5.07) * mm, v(-5.64, -5.6) * mm, v(-4.13, -6.23) * mm]});
            skFitSpline(sketch, "E528", {"points": [v(-4.13, -6.23) * mm, v(-2.6, -6.86) * mm, v(-1.35, -7.38) * mm, v(-1.33, -7.38) * mm]});
            skFitSpline(sketch, "E529", {"points": [v(-1.33, -7.38) * mm, v(-1.3, -7.38) * mm, v(-1.16, -7.23) * mm, v(-1.01, -7.04) * mm]});
            skLineSegment(sketch, "E530", {"start": v(1.1, -1.2) * mm, "end": v(1.14, -0.68) * mm});
            skLineSegment(sketch, "E531", {"start": v(1.14, -0.68) * mm, "end": v(-1.81, -0.68) * mm});
            skLineSegment(sketch, "E532", {"start": v(-1.81, -0.68) * mm, "end": v(-4.76, -0.68) * mm});
            skLineSegment(sketch, "E533", {"start": v(-4.76, -0.68) * mm, "end": v(-4.8, -1.04) * mm});
            skFitSpline(sketch, "E534", {"points": [v(-15.34, -1.74) * mm, v(-16.8, -1.13) * mm, v(-17.8, -0.68) * mm, v(-17.8, -0.64) * mm]});
            skFitSpline(sketch, "E535", {"points": [v(-17.8, -0.64) * mm, v(-17.8, -0.59) * mm, v(-17.31, -0.57) * mm, v(-15.27, -0.57) * mm]});
            skFitSpline(sketch, "E536", {"points": [v(-12.76, -1.67) * mm, v(-12.76, -2.52) * mm, v(-12.77, -2.77) * mm, v(-12.82, -2.76) * mm]});
            skFitSpline(sketch, "E537", {"points": [v(-12.82, -2.76) * mm, v(-12.86, -2.76) * mm, v(-14, -2.3) * mm, v(-15.34, -1.74) * mm]});
            skLineSegment(sketch, "E538", {"start": v(-15.27, -0.57) * mm, "end": v(-12.76, -0.57) * mm});
            skLineSegment(sketch, "E539", {"start": v(-12.76, -0.57) * mm, "end": v(-12.76, -1.67) * mm});
            skFitSpline(sketch, "E540", {"points": [v(-12.88, -0.7) * mm, v(-12.9, -0.69) * mm, v(-13.92, -0.69) * mm, v(-15.17, -0.7) * mm]});
            skFitSpline(sketch, "E541", {"points": [v(-12.87, -1.66) * mm, v(-12.87, -1.14) * mm, v(-12.87, -0.7) * mm, v(-12.88, -0.7) * mm]});
            skLineSegment(sketch, "E542", {"start": v(-15.17, -0.7) * mm, "end": v(-17.44, -0.7) * mm});
            skLineSegment(sketch, "E543", {"start": v(-17.44, -0.7) * mm, "end": v(-15.17, -1.65) * mm});
            skLineSegment(sketch, "E544", {"start": v(-15.17, -1.65) * mm, "end": v(-12.89, -2.6) * mm});
            skLineSegment(sketch, "E545", {"start": v(-12.89, -2.6) * mm, "end": v(-12.87, -1.66) * mm});
            skLineSegment(sketch, "E546", {"start": v(-12.88, -0.7) * mm, "end": v(-12.88, -0.7) * mm});
            skFitSpline(sketch, "E547", {"points": [v(-31.68, 1.03) * mm, v(-32.03, 1.03) * mm, v(-32.09, 1.02) * mm, v(-32.22, 0.9) * mm]});
            skFitSpline(sketch, "E548", {"points": [v(-32.22, 0.9) * mm, v(-32.41, 0.7) * mm, v(-32.86, 0.66) * mm, v(-33.12, 0.8) * mm]});
            skFitSpline(sketch, "E549", {"points": [v(-33.12, 0.8) * mm, v(-33.48, 0.98) * mm, v(-33.55, 1.59) * mm, v(-33.23, 1.91) * mm]});
            skLineSegment(sketch, "E550", {"start": v(-31.3, -0.1) * mm, "end": v(-31.3, 1.03) * mm});
            skLineSegment(sketch, "E551", {"start": v(-31.3, 1.03) * mm, "end": v(-31.68, 1.03) * mm});
            skFitSpline(sketch, "E552", {"points": [v(-33.07, 2.71) * mm, v(-33.07, 3.29) * mm, v(-33.08, 3.34) * mm, v(-33.18, 3.4) * mm]});
            skFitSpline(sketch, "E553", {"points": [v(-33.18, 3.4) * mm, v(-33.32, 3.47) * mm, v(-33.44, 3.76) * mm, v(-33.44, 4) * mm]});
            skFitSpline(sketch, "E554", {"points": [v(-33.44, 4) * mm, v(-33.44, 4.6) * mm, v(-32.64, 4.9) * mm, v(-32.22, 4.46) * mm]});
            skFitSpline(sketch, "E555", {"points": [v(-32.22, 4.46) * mm, v(-32.07, 4.32) * mm, v(-32.03, 4.3) * mm, v(-31.68, 4.3) * mm]});
            skLineSegment(sketch, "E556", {"start": v(-33.23, 1.91) * mm, "end": v(-33.07, 2.08) * mm});
            skLineSegment(sketch, "E557", {"start": v(-33.07, 2.08) * mm, "end": v(-33.07, 2.71) * mm});
            skFitSpline(sketch, "E558", {"points": [v(-28.9, 5.7) * mm, v(-26.94, 5.7) * mm, v(-26.82, 5.68) * mm, v(-26.25, 5.32) * mm]});
            skFitSpline(sketch, "E559", {"points": [v(-26.25, 5.32) * mm, v(-25.88, 5.08) * mm, v(-25.35, 4.48) * mm, v(-25.15, 4.08) * mm]});
            skFitSpline(sketch, "E560", {"points": [v(-25.15, 4.08) * mm, v(-24.3, 2.38) * mm, v(-25.16, 0.22) * mm, v(-26.88, -0.22) * mm]});
            skFitSpline(sketch, "E561", {"points": [v(-26.88, -0.22) * mm, v(-27.13, -0.29) * mm, v(-27.54, -0.3) * mm, v(-28.92, -0.3) * mm]});
            skLineSegment(sketch, "E562", {"start": v(-31.68, 4.3) * mm, "end": v(-31.3, 4.3) * mm});
            skLineSegment(sketch, "E563", {"start": v(-31.3, 4.3) * mm, "end": v(-31.3, 5.43) * mm});
            skLineSegment(sketch, "E564", {"start": v(-31.3, 5.43) * mm, "end": v(-31.3, 6.55) * mm});
            skLineSegment(sketch, "E565", {"start": v(-31.3, 6.55) * mm, "end": v(-30.98, 6.55) * mm});
            skLineSegment(sketch, "E566", {"start": v(-30.98, 6.55) * mm, "end": v(-30.66, 6.55) * mm});
            skLineSegment(sketch, "E567", {"start": v(-30.66, 6.55) * mm, "end": v(-30.66, 6.13) * mm});
            skLineSegment(sketch, "E568", {"start": v(-30.66, 6.13) * mm, "end": v(-30.66, 5.7) * mm});
            skLineSegment(sketch, "E569", {"start": v(-30.66, 5.7) * mm, "end": v(-28.9, 5.7) * mm});
            skLineSegment(sketch, "E570", {"start": v(-28.92, -0.3) * mm, "end": v(-30.66, -0.3) * mm});
            skLineSegment(sketch, "E571", {"start": v(-30.66, -0.3) * mm, "end": v(-30.66, -0.76) * mm});
            skLineSegment(sketch, "E572", {"start": v(-30.66, -0.76) * mm, "end": v(-30.66, -1.22) * mm});
            skLineSegment(sketch, "E573", {"start": v(-30.66, -1.22) * mm, "end": v(-30.98, -1.22) * mm});
            skLineSegment(sketch, "E574", {"start": v(-30.98, -1.22) * mm, "end": v(-31.3, -1.22) * mm});
            skLineSegment(sketch, "E575", {"start": v(-31.3, -1.22) * mm, "end": v(-31.3, -0.1) * mm});
            skFitSpline(sketch, "E576", {"points": [v(-29.03, -0.2) * mm, v(-27.65, -0.2) * mm, v(-27.24, -0.18) * mm, v(-26.99, -0.12) * mm]});
            skFitSpline(sketch, "E577", {"points": [v(-26.99, -0.12) * mm, v(-25.58, 0.25) * mm, v(-24.64, 1.89) * mm, v(-25, 3.31) * mm]});
            skFitSpline(sketch, "E578", {"points": [v(-25, 3.31) * mm, v(-25.18, 4.02) * mm, v(-25.75, 4.82) * mm, v(-26.36, 5.2) * mm]});
            skFitSpline(sketch, "E579", {"points": [v(-26.36, 5.2) * mm, v(-26.92, 5.57) * mm, v(-27.05, 5.6) * mm, v(-29, 5.6) * mm]});
            skLineSegment(sketch, "E580", {"start": v(-30.76, -0.65) * mm, "end": v(-30.76, -0.2) * mm});
            skLineSegment(sketch, "E581", {"start": v(-30.76, -0.2) * mm, "end": v(-29.03, -0.2) * mm});
            skFitSpline(sketch, "E582", {"points": [v(-31.68, 4.2) * mm, v(-32.14, 4.2) * mm, v(-32.17, 4.2) * mm, v(-32.32, 4.35) * mm]});
            skFitSpline(sketch, "E583", {"points": [v(-32.32, 4.35) * mm, v(-32.4, 4.44) * mm, v(-32.54, 4.52) * mm, v(-32.61, 4.54) * mm]});
            skFitSpline(sketch, "E584", {"points": [v(-32.61, 4.54) * mm, v(-32.8, 4.59) * mm, v(-33.12, 4.43) * mm, v(-33.25, 4.2) * mm]});
            skFitSpline(sketch, "E585", {"points": [v(-33.25, 4.2) * mm, v(-33.34, 4.05) * mm, v(-33.34, 4) * mm, v(-33.29, 3.82) * mm]});
            skFitSpline(sketch, "E586", {"points": [v(-33.29, 3.82) * mm, v(-33.25, 3.7) * mm, v(-33.16, 3.57) * mm, v(-33.1, 3.52) * mm]});
            skFitSpline(sketch, "E587", {"points": [v(-33.1, 3.52) * mm, v(-32.96, 3.44) * mm, v(-32.96, 3.42) * mm, v(-32.96, 2.7) * mm]});
            skLineSegment(sketch, "E588", {"start": v(-29, 5.6) * mm, "end": v(-30.76, 5.6) * mm});
            skLineSegment(sketch, "E589", {"start": v(-30.76, 5.6) * mm, "end": v(-30.76, 6.02) * mm});
            skLineSegment(sketch, "E590", {"start": v(-30.76, 6.02) * mm, "end": v(-30.76, 6.45) * mm});
            skLineSegment(sketch, "E591", {"start": v(-30.76, 6.45) * mm, "end": v(-30.98, 6.45) * mm});
            skLineSegment(sketch, "E592", {"start": v(-30.98, 6.45) * mm, "end": v(-31.2, 6.45) * mm});
            skLineSegment(sketch, "E593", {"start": v(-31.2, 6.45) * mm, "end": v(-31.2, 5.32) * mm});
            skLineSegment(sketch, "E594", {"start": v(-31.2, 5.32) * mm, "end": v(-31.2, 4.2) * mm});
            skLineSegment(sketch, "E595", {"start": v(-31.2, 4.2) * mm, "end": v(-31.68, 4.2) * mm});
            skFitSpline(sketch, "E596", {"points": [v(-33.12, 1.81) * mm, v(-33.32, 1.62) * mm, v(-33.36, 1.42) * mm, v(-33.26, 1.17) * mm]});
            skFitSpline(sketch, "E597", {"points": [v(-33.26, 1.17) * mm, v(-33.1, 0.8) * mm, v(-32.6, 0.71) * mm, v(-32.32, 1) * mm]});
            skFitSpline(sketch, "E598", {"points": [v(-32.32, 1) * mm, v(-32.2, 1.13) * mm, v(-32.15, 1.14) * mm, v(-31.7, 1.14) * mm]});
            skLineSegment(sketch, "E599", {"start": v(-32.96, 2.7) * mm, "end": v(-32.96, 1.97) * mm});
            skLineSegment(sketch, "E600", {"start": v(-32.96, 1.97) * mm, "end": v(-33.12, 1.81) * mm});
            skLineSegment(sketch, "E601", {"start": v(-31.7, 1.14) * mm, "end": v(-31.2, 1.14) * mm});
            skLineSegment(sketch, "E602", {"start": v(-31.2, 1.14) * mm, "end": v(-31.2, 0.02) * mm});
            skLineSegment(sketch, "E603", {"start": v(-31.2, 0.02) * mm, "end": v(-31.2, -1.1) * mm});
            skLineSegment(sketch, "E604", {"start": v(-31.2, -1.1) * mm, "end": v(-30.98, -1.1) * mm});
            skLineSegment(sketch, "E605", {"start": v(-30.98, -1.1) * mm, "end": v(-30.76, -1.1) * mm});
            skLineSegment(sketch, "E606", {"start": v(-30.76, -1.1) * mm, "end": v(-30.76, -0.65) * mm});
            skFitSpline(sketch, "E607", {"points": [v(-26.83, 4.99) * mm, v(-26.22, 4.7) * mm, v(-25.65, 4) * mm, v(-25.44, 3.29) * mm]});
            skFitSpline(sketch, "E608", {"points": [v(-25.44, 3.29) * mm, v(-25.12, 2.21) * mm, v(-25.7, 0.91) * mm, v(-26.73, 0.43) * mm]});
            skLineSegment(sketch, "E609", {"start": v(-30.76, 0.68) * mm, "end": v(-30.76, 1.14) * mm});
            skLineSegment(sketch, "E610", {"start": v(-30.76, 1.14) * mm, "end": v(-30.12, 1.14) * mm});
            skLineSegment(sketch, "E611", {"start": v(-30.12, 1.14) * mm, "end": v(-29.48, 1.14) * mm});
            skLineSegment(sketch, "E612", {"start": v(-29.48, 1.14) * mm, "end": v(-29.48, 1.38) * mm});
            skLineSegment(sketch, "E613", {"start": v(-29.48, 1.38) * mm, "end": v(-29.48, 1.62) * mm});
            skLineSegment(sketch, "E614", {"start": v(-29.48, 1.62) * mm, "end": v(-30.12, 1.62) * mm});
            skLineSegment(sketch, "E615", {"start": v(-30.12, 1.62) * mm, "end": v(-30.76, 1.62) * mm});
            skLineSegment(sketch, "E616", {"start": v(-30.76, 1.62) * mm, "end": v(-30.76, 2.7) * mm});
            skLineSegment(sketch, "E617", {"start": v(-30.76, 2.7) * mm, "end": v(-30.76, 3.77) * mm});
            skLineSegment(sketch, "E618", {"start": v(-30.76, 3.77) * mm, "end": v(-30.12, 3.77) * mm});
            skLineSegment(sketch, "E619", {"start": v(-30.12, 3.77) * mm, "end": v(-29.48, 3.77) * mm});
            skLineSegment(sketch, "E620", {"start": v(-29.48, 3.77) * mm, "end": v(-29.48, 3.98) * mm});
            skLineSegment(sketch, "E621", {"start": v(-29.48, 3.98) * mm, "end": v(-29.48, 4.2) * mm});
            skLineSegment(sketch, "E622", {"start": v(-29.48, 4.2) * mm, "end": v(-30.12, 4.2) * mm});
            skLineSegment(sketch, "E623", {"start": v(-30.12, 4.2) * mm, "end": v(-30.76, 4.2) * mm});
            skLineSegment(sketch, "E624", {"start": v(-30.76, 4.2) * mm, "end": v(-30.76, 4.68) * mm});
            skLineSegment(sketch, "E625", {"start": v(-30.76, 4.68) * mm, "end": v(-30.76, 5.17) * mm});
            skLineSegment(sketch, "E626", {"start": v(-30.76, 5.17) * mm, "end": v(-28.95, 5.15) * mm});
            skLineSegment(sketch, "E627", {"start": v(-28.95, 5.15) * mm, "end": v(-27.14, 5.13) * mm});
            skLineSegment(sketch, "E628", {"start": v(-27.14, 5.13) * mm, "end": v(-26.83, 4.99) * mm});
            skFitSpline(sketch, "E629", {"points": [v(-26.83, 0.54) * mm, v(-25.92, 0.97) * mm, v(-25.3, 2.13) * mm, v(-25.5, 3.04) * mm]});
            skFitSpline(sketch, "E630", {"points": [v(-25.5, 3.04) * mm, v(-25.67, 3.8) * mm, v(-26.28, 4.57) * mm, v(-26.94, 4.88) * mm]});
            skLineSegment(sketch, "E631", {"start": v(-26.73, 0.43) * mm, "end": v(-27.1, 0.26) * mm});
            skLineSegment(sketch, "E632", {"start": v(-27.1, 0.26) * mm, "end": v(-28.93, 0.24) * mm});
            skLineSegment(sketch, "E633", {"start": v(-28.93, 0.24) * mm, "end": v(-30.76, 0.23) * mm});
            skLineSegment(sketch, "E634", {"start": v(-30.76, 0.23) * mm, "end": v(-30.76, 0.68) * mm});
            skLineSegment(sketch, "E635", {"start": v(-26.94, 4.88) * mm, "end": v(-27.25, 5.03) * mm});
            skLineSegment(sketch, "E636", {"start": v(-27.25, 5.03) * mm, "end": v(-28.95, 5.04) * mm});
            skLineSegment(sketch, "E637", {"start": v(-28.95, 5.04) * mm, "end": v(-30.66, 5.06) * mm});
            skLineSegment(sketch, "E638", {"start": v(-30.66, 5.06) * mm, "end": v(-30.66, 4.68) * mm});
            skLineSegment(sketch, "E639", {"start": v(-30.66, 4.68) * mm, "end": v(-30.66, 4.3) * mm});
            skLineSegment(sketch, "E640", {"start": v(-30.66, 4.3) * mm, "end": v(-30.01, 4.3) * mm});
            skLineSegment(sketch, "E641", {"start": v(-30.01, 4.3) * mm, "end": v(-29.37, 4.3) * mm});
            skLineSegment(sketch, "E642", {"start": v(-29.37, 4.3) * mm, "end": v(-29.37, 3.98) * mm});
            skLineSegment(sketch, "E643", {"start": v(-29.37, 3.98) * mm, "end": v(-29.37, 3.66) * mm});
            skLineSegment(sketch, "E644", {"start": v(-29.37, 3.66) * mm, "end": v(-30.01, 3.66) * mm});
            skLineSegment(sketch, "E645", {"start": v(-30.01, 3.66) * mm, "end": v(-30.66, 3.66) * mm});
            skLineSegment(sketch, "E646", {"start": v(-30.66, 3.66) * mm, "end": v(-30.66, 2.7) * mm});
            skLineSegment(sketch, "E647", {"start": v(-30.66, 2.7) * mm, "end": v(-30.66, 1.73) * mm});
            skLineSegment(sketch, "E648", {"start": v(-30.66, 1.73) * mm, "end": v(-30.01, 1.73) * mm});
            skLineSegment(sketch, "E649", {"start": v(-30.01, 1.73) * mm, "end": v(-29.37, 1.73) * mm});
            skLineSegment(sketch, "E650", {"start": v(-29.37, 1.73) * mm, "end": v(-29.37, 1.38) * mm});
            skLineSegment(sketch, "E651", {"start": v(-29.37, 1.38) * mm, "end": v(-29.37, 1.03) * mm});
            skLineSegment(sketch, "E652", {"start": v(-29.37, 1.03) * mm, "end": v(-30.01, 1.03) * mm});
            skLineSegment(sketch, "E653", {"start": v(-30.01, 1.03) * mm, "end": v(-30.66, 1.03) * mm});
            skLineSegment(sketch, "E654", {"start": v(-30.66, 1.03) * mm, "end": v(-30.66, 0.68) * mm});
            skLineSegment(sketch, "E655", {"start": v(-30.66, 0.68) * mm, "end": v(-30.66, 0.33) * mm});
            skLineSegment(sketch, "E656", {"start": v(-30.66, 0.33) * mm, "end": v(-28.93, 0.35) * mm});
            skLineSegment(sketch, "E657", {"start": v(-28.93, 0.35) * mm, "end": v(-27.2, 0.36) * mm});
            skLineSegment(sketch, "E658", {"start": v(-27.2, 0.36) * mm, "end": v(-26.83, 0.54) * mm});
            skFitSpline(sketch, "E659", {"points": [v(-32.34, 3.57) * mm, v(-32.15, 3.77) * mm, v(-32.14, 3.77) * mm, v(-31.67, 3.77) * mm]});
            skLineSegment(sketch, "E660", {"start": v(-32.36, 1.81) * mm, "end": v(-32.53, 2) * mm});
            skLineSegment(sketch, "E661", {"start": v(-32.53, 2) * mm, "end": v(-32.53, 2.69) * mm});
            skLineSegment(sketch, "E662", {"start": v(-32.53, 2.69) * mm, "end": v(-32.53, 3.38) * mm});
            skLineSegment(sketch, "E663", {"start": v(-32.53, 3.38) * mm, "end": v(-32.34, 3.57) * mm});
            skFitSpline(sketch, "E664", {"points": [v(-31.69, 1.63) * mm, v(-32.18, 1.63) * mm, v(-32.18, 1.63) * mm, v(-32.36, 1.81) * mm]});
            skLineSegment(sketch, "E665", {"start": v(-31.67, 3.77) * mm, "end": v(-31.2, 3.77) * mm});
            skLineSegment(sketch, "E666", {"start": v(-31.2, 3.77) * mm, "end": v(-31.2, 2.7) * mm});
            skLineSegment(sketch, "E667", {"start": v(-31.2, 2.7) * mm, "end": v(-31.2, 1.62) * mm});
            skLineSegment(sketch, "E668", {"start": v(-31.2, 1.62) * mm, "end": v(-31.69, 1.63) * mm});
            skLineSegment(sketch, "E669", {"start": v(-32.36, 1.81) * mm, "end": v(-32.36, 1.81) * mm});
            skFitSpline(sketch, "E670", {"points": [v(-31.67, 3.66) * mm, v(-32.02, 3.66) * mm, v(-32.05, 3.65) * mm, v(-32.23, 3.47) * mm]});
            skLineSegment(sketch, "E671", {"start": v(-31.3, 2.7) * mm, "end": v(-31.3, 3.66) * mm});
            skLineSegment(sketch, "E672", {"start": v(-31.3, 3.66) * mm, "end": v(-31.67, 3.66) * mm});
            skFitSpline(sketch, "E673", {"points": [v(-32.25, 1.92) * mm, v(-32.08, 1.75) * mm, v(-32.06, 1.74) * mm, v(-31.69, 1.73) * mm]});
            skLineSegment(sketch, "E674", {"start": v(-32.23, 3.47) * mm, "end": v(-32.42, 3.27) * mm});
            skLineSegment(sketch, "E675", {"start": v(-32.42, 3.27) * mm, "end": v(-32.42, 2.69) * mm});
            skLineSegment(sketch, "E676", {"start": v(-32.42, 2.69) * mm, "end": v(-32.42, 2.1) * mm});
            skLineSegment(sketch, "E677", {"start": v(-32.42, 2.1) * mm, "end": v(-32.25, 1.92) * mm});
            skFitSpline(sketch, "E678", {"points": [v(-17.74, -0.18) * mm, v(-17.74, -0.11) * mm, v(-12.89, 1.93) * mm, v(-12.84, 1.89) * mm]});
            skFitSpline(sketch, "E679", {"points": [v(-12.84, 1.89) * mm, v(-12.83, 1.87) * mm, v(-12.8, 1.39) * mm, v(-12.8, 0.8) * mm]});
            skLineSegment(sketch, "E680", {"start": v(-31.69, 1.73) * mm, "end": v(-31.3, 1.73) * mm});
            skLineSegment(sketch, "E681", {"start": v(-31.3, 1.73) * mm, "end": v(-31.3, 2.7) * mm});
            skFitSpline(sketch, "E682", {"points": [v(-15.26, -0.25) * mm, v(-17.27, -0.25) * mm, v(-17.74, -0.24) * mm, v(-17.74, -0.18) * mm]});
            skLineSegment(sketch, "E683", {"start": v(-12.8, 0.8) * mm, "end": v(-12.78, -0.25) * mm});
            skLineSegment(sketch, "E684", {"start": v(-12.78, -0.25) * mm, "end": v(-15.26, -0.25) * mm});
            skFitSpline(sketch, "E685", {"points": [v(-13.17, 1.63) * mm, v(-13.87, 1.35) * mm, v(-17.33, -0.1) * mm, v(-17.36, -0.12) * mm]});
            skFitSpline(sketch, "E686", {"points": [v(-17.36, -0.12) * mm, v(-17.37, -0.13) * mm, v(-16.38, -0.14) * mm, v(-15.15, -0.14) * mm]});
            skLineSegment(sketch, "E687", {"start": v(-12.92, 0.8) * mm, "end": v(-12.92, 1.73) * mm});
            skLineSegment(sketch, "E688", {"start": v(-12.92, 1.73) * mm, "end": v(-13.17, 1.63) * mm});
            skFitSpline(sketch, "E689", {"points": [v(-4.9, 0.06) * mm, v(-5.04, 1.31) * mm, v(-5.45, 2.24) * mm, v(-6.23, 3) * mm]});
            skFitSpline(sketch, "E690", {"points": [v(-6.23, 3) * mm, v(-6.55, 3.34) * mm, v(-7.1, 3.74) * mm, v(-7.4, 3.88) * mm]});
            skFitSpline(sketch, "E691", {"points": [v(-7.4, 3.88) * mm, v(-7.5, 3.92) * mm, v(-7.56, 3.98) * mm, v(-7.56, 4.03) * mm]});
            skFitSpline(sketch, "E692", {"points": [v(-7.56, 4.03) * mm, v(-7.55, 4.1) * mm, v(-6.74, 4.45) * mm, v(-4.6, 5.34) * mm]});
            skFitSpline(sketch, "E693", {"points": [v(-4.6, 5.34) * mm, v(-2.97, 6) * mm, v(-1.6, 6.56) * mm, v(-1.55, 6.56) * mm]});
            skFitSpline(sketch, "E694", {"points": [v(-1.55, 6.56) * mm, v(-1.44, 6.55) * mm, v(-0.97, 6.06) * mm, v(-0.58, 5.54) * mm]});
            skFitSpline(sketch, "E695", {"points": [v(-0.58, 5.54) * mm, v(0.47, 4.13) * mm, v(1.05, 2.38) * mm, v(1.2, 0.22) * mm]});
            skLineSegment(sketch, "E696", {"start": v(-15.15, -0.14) * mm, "end": v(-12.92, -0.14) * mm});
            skLineSegment(sketch, "E697", {"start": v(-12.92, -0.14) * mm, "end": v(-12.92, 0.8) * mm});
            skFitSpline(sketch, "E698", {"points": [v(1.09, 0.22) * mm, v(0.98, 1.8) * mm, v(0.55, 3.4) * mm, v(-0.11, 4.55) * mm]});
            skFitSpline(sketch, "E699", {"points": [v(-0.11, 4.55) * mm, v(-0.43, 5.1) * mm, v(-1.02, 5.9) * mm, v(-1.35, 6.21) * mm]});
            skLineSegment(sketch, "E700", {"start": v(1.2, 0.22) * mm, "end": v(1.24, -0.25) * mm});
            skLineSegment(sketch, "E701", {"start": v(1.24, -0.25) * mm, "end": v(-1.82, -0.25) * mm});
            skLineSegment(sketch, "E702", {"start": v(-1.82, -0.25) * mm, "end": v(-4.87, -0.25) * mm});
            skLineSegment(sketch, "E703", {"start": v(-4.87, -0.25) * mm, "end": v(-4.9, 0.06) * mm});
            skFitSpline(sketch, "E704", {"points": [v(-4.34, 5.3) * mm, v(-5.86, 4.66) * mm, v(-7.16, 4.12) * mm, v(-7.23, 4.09) * mm]});
            skFitSpline(sketch, "E705", {"points": [v(-7.23, 4.09) * mm, v(-7.36, 4.03) * mm, v(-7.35, 4.02) * mm, v(-7.02, 3.82) * mm]});
            skFitSpline(sketch, "E706", {"points": [v(-7.02, 3.82) * mm, v(-5.7, 3.03) * mm, v(-4.98, 1.83) * mm, v(-4.8, 0.16) * mm]});
            skLineSegment(sketch, "E707", {"start": v(-1.35, 6.21) * mm, "end": v(-1.58, 6.44) * mm});
            skLineSegment(sketch, "E708", {"start": v(-1.58, 6.44) * mm, "end": v(-4.34, 5.3) * mm});
            skFitSpline(sketch, "E709", {"points": [v(-18.7, 0.46) * mm, v(-18.7, 0.82) * mm, v(-18.74, 3) * mm, v(-18.78, 5.32) * mm]});
            skFitSpline(sketch, "E710", {"points": [v(-18.78, 5.32) * mm, v(-18.83, 7.64) * mm, v(-18.86, 9.6) * mm, v(-18.86, 9.68) * mm]});
            skLineSegment(sketch, "E711", {"start": v(-4.8, 0.16) * mm, "end": v(-4.76, -0.14) * mm});
            skLineSegment(sketch, "E712", {"start": v(-4.76, -0.14) * mm, "end": v(-1.82, -0.14) * mm});
            skLineSegment(sketch, "E713", {"start": v(-1.82, -0.14) * mm, "end": v(1.11, -0.14) * mm});
            skLineSegment(sketch, "E714", {"start": v(1.11, -0.14) * mm, "end": v(1.09, 0.22) * mm});
            skFitSpline(sketch, "E715", {"points": [v(-13.97, 9.8) * mm, v(-11.28, 9.8) * mm, v(-9.02, 9.77) * mm, v(-8.94, 9.75) * mm]});
            skFitSpline(sketch, "E716", {"points": [v(-8.94, 9.75) * mm, v(-8.86, 9.72) * mm, v(-8.79, 9.68) * mm, v(-8.79, 9.64) * mm]});
            skFitSpline(sketch, "E717", {"points": [v(-8.79, 9.64) * mm, v(-8.79, 9.56) * mm, v(-18.55, -0.2) * mm, v(-18.64, -0.2) * mm]});
            skFitSpline(sketch, "E718", {"points": [v(-18.64, -0.2) * mm, v(-18.69, -0.2) * mm, v(-18.7, -0.03) * mm, v(-18.7, 0.46) * mm]});
            skLineSegment(sketch, "E719", {"start": v(-18.86, 9.68) * mm, "end": v(-18.86, 9.83) * mm});
            skLineSegment(sketch, "E720", {"start": v(-18.86, 9.83) * mm, "end": v(-13.97, 9.8) * mm});
            skLineSegment(sketch, "E721", {"start": v(-13.97, 9.8) * mm, "end": v(-18.86, 9.68) * mm});
            skFitSpline(sketch, "E722", {"points": [v(-9.1, 9.63) * mm, v(-9.16, 9.67) * mm, v(-10.83, 9.7) * mm, v(-13.98, 9.7) * mm]});
            skFitSpline(sketch, "E723", {"points": [v(-18.73, 8.37) * mm, v(-18.69, 6.56) * mm, v(-18.6, 1.22) * mm, v(-18.6, 0.53) * mm]});
            skLineSegment(sketch, "E724", {"start": v(-13.98, 9.7) * mm, "end": v(-18.76, 9.72) * mm});
            skLineSegment(sketch, "E725", {"start": v(-18.76, 9.72) * mm, "end": v(-18.73, 8.37) * mm});
            skFitSpline(sketch, "E726", {"points": [v(-13.8, 4.78) * mm, v(-9.72, 8.86) * mm, v(-9.02, 9.59) * mm, v(-9.1, 9.63) * mm]});
            skLineSegment(sketch, "E727", {"start": v(-18.6, 0.53) * mm, "end": v(-18.6, -0.01) * mm});
            skLineSegment(sketch, "E728", {"start": v(-18.6, -0.01) * mm, "end": v(-13.8, 4.78) * mm});
            skFitSpline(sketch, "E729", {"points": [v(-18.06, 0.02) * mm, v(-18.06, 0.06) * mm, v(-15.9, 2.25) * mm, v(-13.28, 4.88) * mm]});
            skFitSpline(sketch, "E730", {"points": [v(-13.28, 4.88) * mm, v(-9.62, 8.53) * mm, v(-8.46, 9.66) * mm, v(-8.37, 9.66) * mm]});
            skFitSpline(sketch, "E731", {"points": [v(-8.37, 9.66) * mm, v(-8.16, 9.66) * mm, v(-6.93, 9.4) * mm, v(-6.3, 9.23) * mm]});
            skFitSpline(sketch, "E732", {"points": [v(-6.3, 9.23) * mm, v(-5.14, 8.9) * mm, v(-3.82, 8.32) * mm, v(-2.93, 7.74) * mm]});
            skFitSpline(sketch, "E733", {"points": [v(-2.93, 7.74) * mm, v(-2.4, 7.39) * mm, v(-1.71, 6.84) * mm, v(-1.72, 6.76) * mm]});
            skFitSpline(sketch, "E734", {"points": [v(-1.72, 6.76) * mm, v(-1.72, 6.72) * mm, v(-3.08, 6.12) * mm, v(-4.8, 5.41) * mm]});
            skFitSpline(sketch, "E735", {"points": [v(-8.36, 4.27) * mm, v(-9.4, 4.58) * mm, v(-9.41, 4.59) * mm, v(-11.2, 4.61) * mm]});
            skLineSegment(sketch, "E736", {"start": v(-4.8, 5.41) * mm, "end": v(-7.9, 4.13) * mm});
            skLineSegment(sketch, "E737", {"start": v(-7.9, 4.13) * mm, "end": v(-8.36, 4.27) * mm});
            skFitSpline(sketch, "E738", {"points": [v(-15.33, 1.05) * mm, v(-16.7, 0.48) * mm, v(-17.87, 0) * mm, v(-17.94, -0.02) * mm]});
            skFitSpline(sketch, "E739", {"points": [v(-17.94, -0.02) * mm, v(-18.02, -0.04) * mm, v(-18.06, -0.03) * mm, v(-18.06, 0.02) * mm]});
            skLineSegment(sketch, "E740", {"start": v(-11.2, 4.61) * mm, "end": v(-12.87, 4.63) * mm});
            skLineSegment(sketch, "E741", {"start": v(-12.87, 4.63) * mm, "end": v(-12.86, 3.36) * mm});
            skLineSegment(sketch, "E742", {"start": v(-12.86, 3.36) * mm, "end": v(-12.84, 2.09) * mm});
            skLineSegment(sketch, "E743", {"start": v(-12.84, 2.09) * mm, "end": v(-15.33, 1.05) * mm});
            skFitSpline(sketch, "E744", {"points": [v(-8.76, 4.52) * mm, v(-8.4, 4.43) * mm, v(-8.06, 4.34) * mm, v(-7.99, 4.32) * mm]});
            skFitSpline(sketch, "E745", {"points": [v(-7.99, 4.32) * mm, v(-7.9, 4.3) * mm, v(-6.92, 4.68) * mm, v(-4.93, 5.5) * mm]});
            skFitSpline(sketch, "E746", {"points": [v(-4.93, 5.5) * mm, v(-3.32, 6.18) * mm, v(-1.99, 6.74) * mm, v(-1.97, 6.77) * mm]});
            skFitSpline(sketch, "E747", {"points": [v(-1.97, 6.77) * mm, v(-1.91, 6.82) * mm, v(-2.85, 7.53) * mm, v(-3.36, 7.83) * mm]});
            skFitSpline(sketch, "E748", {"points": [v(-3.36, 7.83) * mm, v(-4.67, 8.6) * mm, v(-6.02, 9.09) * mm, v(-7.69, 9.42) * mm]});
            skLineSegment(sketch, "E749", {"start": v(-15.12, 1.3) * mm, "end": v(-12.95, 2.19) * mm});
            skLineSegment(sketch, "E750", {"start": v(-12.95, 2.19) * mm, "end": v(-12.96, 3.47) * mm});
            skLineSegment(sketch, "E751", {"start": v(-12.96, 3.47) * mm, "end": v(-12.98, 4.74) * mm});
            skLineSegment(sketch, "E752", {"start": v(-12.98, 4.74) * mm, "end": v(-11.2, 4.72) * mm});
            skLineSegment(sketch, "E753", {"start": v(-11.2, 4.72) * mm, "end": v(-9.4, 4.7) * mm});
            skLineSegment(sketch, "E754", {"start": v(-9.4, 4.7) * mm, "end": v(-8.76, 4.52) * mm});
            skFitSpline(sketch, "E755", {"points": [v(-13.05, 4.9) * mm, v(-16.79, 1.15) * mm, v(-17.67, 0.24) * mm, v(-17.5, 0.3) * mm]});
            skFitSpline(sketch, "E756", {"points": [v(-17.5, 0.3) * mm, v(-17.38, 0.36) * mm, v(-16.3, 0.8) * mm, v(-15.12, 1.3) * mm]});
            skLineSegment(sketch, "E757", {"start": v(-7.69, 9.42) * mm, "end": v(-8.38, 9.56) * mm});
            skLineSegment(sketch, "E758", {"start": v(-8.38, 9.56) * mm, "end": v(-13.05, 4.9) * mm});
            skLineSegment(sketch, "E759", {"start": v(10.88, 6.77) * mm, "end": v(10.88, 7.1) * mm});
            skLineSegment(sketch, "E760", {"start": v(10.88, 7.1) * mm, "end": v(11.17, 7.1) * mm});
            skLineSegment(sketch, "E761", {"start": v(11.17, 7.1) * mm, "end": v(11.47, 7.1) * mm});
            skLineSegment(sketch, "E762", {"start": v(11.47, 7.1) * mm, "end": v(11.47, 6.77) * mm});
            skLineSegment(sketch, "E763", {"start": v(11.47, 6.77) * mm, "end": v(11.47, 6.45) * mm});
            skLineSegment(sketch, "E764", {"start": v(11.47, 6.45) * mm, "end": v(11.17, 6.45) * mm});
            skLineSegment(sketch, "E765", {"start": v(11.17, 6.45) * mm, "end": v(10.88, 6.45) * mm});
            skLineSegment(sketch, "E766", {"start": v(10.88, 6.45) * mm, "end": v(10.88, 6.77) * mm});
            skFitSpline(sketch, "E767", {"points": [v(12.29, 8.04) * mm, v(12.7, 8.45) * mm, v(13.02, 8.82) * mm, v(13.02, 8.87) * mm]});
            skFitSpline(sketch, "E768", {"points": [v(13.02, 8.87) * mm, v(13.02, 8.96) * mm, v(13.13, 8.97) * mm, v(14.63, 8.97) * mm]});
            skFitSpline(sketch, "E769", {"points": [v(4.23, 8.97) * mm, v(8.98, 8.97) * mm, v(9.27, 8.96) * mm, v(9.27, 8.87) * mm]});
            skFitSpline(sketch, "E770", {"points": [v(9.27, 8.87) * mm, v(9.27, 8.82) * mm, v(9.6, 8.45) * mm, v(10, 8.04) * mm]});
            skLineSegment(sketch, "E771", {"start": v(14.63, 8.97) * mm, "end": v(16.24, 8.97) * mm});
            skLineSegment(sketch, "E772", {"start": v(16.24, 8.97) * mm, "end": v(16.24, 9.29) * mm});
            skLineSegment(sketch, "E773", {"start": v(16.24, 9.29) * mm, "end": v(16.24, 9.6) * mm});
            skLineSegment(sketch, "E774", {"start": v(16.24, 9.6) * mm, "end": v(14.63, 9.6) * mm});
            skLineSegment(sketch, "E775", {"start": v(14.63, 9.6) * mm, "end": v(13.02, 9.6) * mm});
            skLineSegment(sketch, "E776", {"start": v(13.02, 9.6) * mm, "end": v(13.02, 10.07) * mm});
            skLineSegment(sketch, "E777", {"start": v(13.02, 10.07) * mm, "end": v(13.02, 10.52) * mm});
            skLineSegment(sketch, "E778", {"start": v(13.02, 10.52) * mm, "end": v(14.63, 10.52) * mm});
            skLineSegment(sketch, "E779", {"start": v(14.63, 10.52) * mm, "end": v(16.24, 10.52) * mm});
            skLineSegment(sketch, "E780", {"start": v(16.24, 10.52) * mm, "end": v(16.24, 10.84) * mm});
            skLineSegment(sketch, "E781", {"start": v(16.24, 10.84) * mm, "end": v(16.24, 11.16) * mm});
            skLineSegment(sketch, "E782", {"start": v(16.24, 11.16) * mm, "end": v(14.63, 11.16) * mm});
            skLineSegment(sketch, "E783", {"start": v(14.63, 11.16) * mm, "end": v(13.02, 11.16) * mm});
            skLineSegment(sketch, "E784", {"start": v(13.02, 11.16) * mm, "end": v(13.02, 11.57) * mm});
            skLineSegment(sketch, "E785", {"start": v(13.02, 11.57) * mm, "end": v(13.02, 11.97) * mm});
            skLineSegment(sketch, "E786", {"start": v(13.02, 11.97) * mm, "end": v(11.15, 11.97) * mm});
            skLineSegment(sketch, "E787", {"start": v(11.15, 11.97) * mm, "end": v(9.27, 11.97) * mm});
            skLineSegment(sketch, "E788", {"start": v(9.27, 11.97) * mm, "end": v(9.27, 11.57) * mm});
            skLineSegment(sketch, "E789", {"start": v(9.27, 11.57) * mm, "end": v(9.27, 11.16) * mm});
            skLineSegment(sketch, "E790", {"start": v(9.27, 11.16) * mm, "end": v(4.23, 11.16) * mm});
            skLineSegment(sketch, "E791", {"start": v(4.23, 11.16) * mm, "end": v(-0.8, 11.16) * mm});
            skLineSegment(sketch, "E792", {"start": v(-0.8, 11.16) * mm, "end": v(-0.8, 10.84) * mm});
            skLineSegment(sketch, "E793", {"start": v(-0.8, 10.84) * mm, "end": v(-0.8, 10.52) * mm});
            skLineSegment(sketch, "E794", {"start": v(-0.8, 10.52) * mm, "end": v(4.23, 10.52) * mm});
            skLineSegment(sketch, "E795", {"start": v(4.23, 10.52) * mm, "end": v(9.27, 10.52) * mm});
            skLineSegment(sketch, "E796", {"start": v(9.27, 10.52) * mm, "end": v(9.27, 10.07) * mm});
            skLineSegment(sketch, "E797", {"start": v(9.27, 10.07) * mm, "end": v(9.27, 9.6) * mm});
            skLineSegment(sketch, "E798", {"start": v(9.27, 9.6) * mm, "end": v(4.23, 9.6) * mm});
            skLineSegment(sketch, "E799", {"start": v(4.23, 9.6) * mm, "end": v(-0.8, 9.6) * mm});
            skLineSegment(sketch, "E800", {"start": v(-0.8, 9.6) * mm, "end": v(-0.8, 9.29) * mm});
            skLineSegment(sketch, "E801", {"start": v(-0.8, 9.29) * mm, "end": v(-0.8, 8.97) * mm});
            skLineSegment(sketch, "E802", {"start": v(-0.8, 8.97) * mm, "end": v(4.23, 8.97) * mm});
            skLineSegment(sketch, "E803", {"start": v(10, 8.04) * mm, "end": v(10.74, 7.3) * mm});
            skLineSegment(sketch, "E804", {"start": v(10.74, 7.3) * mm, "end": v(11.15, 7.3) * mm});
            skLineSegment(sketch, "E805", {"start": v(11.15, 7.3) * mm, "end": v(11.55, 7.3) * mm});
            skLineSegment(sketch, "E806", {"start": v(11.55, 7.3) * mm, "end": v(12.29, 8.04) * mm});
            skLineSegment(sketch, "E807", {"start": v(8.14, -1) * mm, "end": v(8.27, -1.11) * mm});
            skLineSegment(sketch, "E808", {"start": v(5.05, 0.18) * mm, "end": v(5.42, -0.44) * mm});
            skSolve(sketch);
        }
        {
            var Q0;
            Q0 = qSketchRegion(id + "F8", true);
            extrude(context, id + "F9", {"entities" : qUnion([Q0]), "depth" : 5 * mm});
        }
        {
            var Q0;
            Q0=makeQuery(id+"F9.opExtrude","SWEPT_BODY",BODY,{"disambiguationData":[OSD([sQuery(id+"F8.wireOp",EDGE,"E100"),sQuery(id+"F8.wireOp",EDGE,"E101"),sQuery(id+"F8.wireOp",EDGE,"E102"),sQuery(id+"F8.wireOp",EDGE,"E103"),sQuery(id+"F8.wireOp",EDGE,"E104"),sQuery(id+"F8.wireOp",EDGE,"E105"),sQuery(id+"F8.wireOp",EDGE,"E106"),sQuery(id+"F8.wireOp",EDGE,"E107"),sQuery(id+"F8.wireOp",EDGE,"E108"),sQuery(id+"F8.wireOp",EDGE,"E109"),sQuery(id+"F8.wireOp",EDGE,"E110"),sQuery(id+"F8.wireOp",EDGE,"E111"),sQuery(id+"F8.wireOp",EDGE,"E112"),sQuery(id+"F8.wireOp",EDGE,"E113"),sQuery(id+"F8.wireOp",EDGE,"E114"),sQuery(id+"F8.wireOp",EDGE,"E115"),sQuery(id+"F8.wireOp",EDGE,"E116"),sQuery(id+"F8.wireOp",EDGE,"E117"),sQuery(id+"F8.wireOp",EDGE,"E118"),sQuery(id+"F8.wireOp",EDGE,"E119"),sQuery(id+"F8.wireOp",EDGE,"E120"),sQuery(id+"F8.wireOp",EDGE,"E121"),sQuery(id+"F8.wireOp",EDGE,"E122"),sQuery(id+"F8.wireOp",EDGE,"E123"),sQuery(id+"F8.wireOp",EDGE,"E124"),sQuery(id+"F8.wireOp",EDGE,"E125"),sQuery(id+"F8.wireOp",EDGE,"E126"),sQuery(id+"F8.wireOp",EDGE,"E127"),sQuery(id+"F8.wireOp",EDGE,"E128"),sQuery(id+"F8.wireOp",EDGE,"E129"),sQuery(id+"F8.wireOp",EDGE,"E130"),sQuery(id+"F8.wireOp",EDGE,"E131"),sQuery(id+"F8.wireOp",EDGE,"E132"),sQuery(id+"F8.wireOp",EDGE,"E133"),sQuery(id+"F8.wireOp",EDGE,"E134"),sQuery(id+"F8.wireOp",EDGE,"E135"),sQuery(id+"F8.wireOp",EDGE,"E136"),sQuery(id+"F8.wireOp",EDGE,"E137"),sQuery(id+"F8.wireOp",EDGE,"E138"),sQuery(id+"F8.wireOp",EDGE,"E139"),sQuery(id+"F8.wireOp",EDGE,"E140"),sQuery(id+"F8.wireOp",EDGE,"E141"),sQuery(id+"F8.wireOp",EDGE,"E142"),sQuery(id+"F8.wireOp",EDGE,"E143"),sQuery(id+"F8.wireOp",EDGE,"E144"),sQuery(id+"F8.wireOp",EDGE,"E145"),sQuery(id+"F8.wireOp",EDGE,"E146"),sQuery(id+"F8.wireOp",EDGE,"E147"),sQuery(id+"F8.wireOp",EDGE,"E148"),sQuery(id+"F8.wireOp",EDGE,"E149"),sQuery(id+"F8.wireOp",EDGE,"E150"),sQuery(id+"F8.wireOp",EDGE,"E151"),sQuery(id+"F8.wireOp",EDGE,"E152"),sQuery(id+"F8.wireOp",EDGE,"E153"),sQuery(id+"F8.wireOp",EDGE,"E154"),sQuery(id+"F8.wireOp",EDGE,"E155"),sQuery(id+"F8.wireOp",EDGE,"E156"),sQuery(id+"F8.wireOp",EDGE,"E157"),sQuery(id+"F8.wireOp",EDGE,"E158"),sQuery(id+"F8.wireOp",EDGE,"E159"),sQuery(id+"F8.wireOp",EDGE,"E160"),sQuery(id+"F8.wireOp",EDGE,"E161"),sQuery(id+"F8.wireOp",EDGE,"E162"),sQuery(id+"F8.wireOp",EDGE,"E163"),sQuery(id+"F8.wireOp",EDGE,"E164"),sQuery(id+"F8.wireOp",EDGE,"E165"),sQuery(id+"F8.wireOp",EDGE,"E166"),sQuery(id+"F8.wireOp",EDGE,"E167"),sQuery(id+"F8.wireOp",EDGE,"E168"),sQuery(id+"F8.wireOp",EDGE,"E169"),sQuery(id+"F8.wireOp",EDGE,"E170"),sQuery(id+"F8.wireOp",EDGE,"E171"),sQuery(id+"F8.wireOp",EDGE,"E172"),sQuery(id+"F8.wireOp",EDGE,"E173"),sQuery(id+"F8.wireOp",EDGE,"E174"),sQuery(id+"F8.wireOp",EDGE,"E175"),sQuery(id+"F8.wireOp",EDGE,"E176"),sQuery(id+"F8.wireOp",EDGE,"E177"),sQuery(id+"F8.wireOp",EDGE,"E178"),sQuery(id+"F8.wireOp",EDGE,"E179"),sQuery(id+"F8.wireOp",EDGE,"E180"),sQuery(id+"F8.wireOp",EDGE,"E181"),sQuery(id+"F8.wireOp",EDGE,"E182"),sQuery(id+"F8.wireOp",EDGE,"E183"),sQuery(id+"F8.wireOp",EDGE,"E184"),sQuery(id+"F8.wireOp",EDGE,"E185"),sQuery(id+"F8.wireOp",EDGE,"E186"),sQuery(id+"F8.wireOp",EDGE,"E187"),sQuery(id+"F8.wireOp",EDGE,"E188"),sQuery(id+"F8.wireOp",EDGE,"E189"),sQuery(id+"F8.wireOp",EDGE,"E190"),sQuery(id+"F8.wireOp",EDGE,"E191"),sQuery(id+"F8.wireOp",EDGE,"E192"),sQuery(id+"F8.wireOp",EDGE,"E193"),sQuery(id+"F8.wireOp",EDGE,"E194"),sQuery(id+"F8.wireOp",EDGE,"E195"),sQuery(id+"F8.wireOp",EDGE,"E196"),sQuery(id+"F8.wireOp",EDGE,"E197"),sQuery(id+"F8.wireOp",EDGE,"E198"),sQuery(id+"F8.wireOp",EDGE,"E199"),sQuery(id+"F8.wireOp",EDGE,"E200"),sQuery(id+"F8.wireOp",EDGE,"E201"),sQuery(id+"F8.wireOp",EDGE,"E202"),sQuery(id+"F8.wireOp",EDGE,"E203"),sQuery(id+"F8.wireOp",EDGE,"E204"),sQuery(id+"F8.wireOp",EDGE,"E205"),sQuery(id+"F8.wireOp",EDGE,"E206"),sQuery(id+"F8.wireOp",EDGE,"E207"),sQuery(id+"F8.wireOp",EDGE,"E208"),sQuery(id+"F8.wireOp",EDGE,"E209"),sQuery(id+"F8.wireOp",EDGE,"E210"),sQuery(id+"F8.wireOp",EDGE,"E211"),sQuery(id+"F8.wireOp",EDGE,"E212"),sQuery(id+"F8.wireOp",EDGE,"E213"),sQuery(id+"F8.wireOp",EDGE,"E214"),sQuery(id+"F8.wireOp",EDGE,"E215"),sQuery(id+"F8.wireOp",EDGE,"E216"),sQuery(id+"F8.wireOp",EDGE,"E217"),sQuery(id+"F8.wireOp",EDGE,"E218"),sQuery(id+"F8.wireOp",EDGE,"E219"),sQuery(id+"F8.wireOp",EDGE,"E220"),sQuery(id+"F8.wireOp",EDGE,"E221"),sQuery(id+"F8.wireOp",EDGE,"E222"),sQuery(id+"F8.wireOp",EDGE,"E223"),sQuery(id+"F8.wireOp",EDGE,"E224"),sQuery(id+"F8.wireOp",EDGE,"E225"),sQuery(id+"F8.wireOp",EDGE,"E226"),sQuery(id+"F8.wireOp",EDGE,"E227"),sQuery(id+"F8.wireOp",EDGE,"E229"),sQuery(id+"F8.wireOp",EDGE,"E230"),sQuery(id+"F8.wireOp",EDGE,"E231"),sQuery(id+"F8.wireOp",EDGE,"E232"),sQuery(id+"F8.wireOp",EDGE,"E233"),sQuery(id+"F8.wireOp",EDGE,"E234"),sQuery(id+"F8.wireOp",EDGE,"E235"),sQuery(id+"F8.wireOp",EDGE,"E236"),sQuery(id+"F8.wireOp",EDGE,"E237"),sQuery(id+"F8.wireOp",EDGE,"E238"),sQuery(id+"F8.wireOp",EDGE,"E239"),sQuery(id+"F8.wireOp",EDGE,"E240"),sQuery(id+"F8.wireOp",EDGE,"E241"),sQuery(id+"F8.wireOp",EDGE,"E242"),sQuery(id+"F8.wireOp",EDGE,"E243"),sQuery(id+"F8.wireOp",EDGE,"E244"),sQuery(id+"F8.wireOp",EDGE,"E245"),sQuery(id+"F8.wireOp",EDGE,"E246"),sQuery(id+"F8.wireOp",EDGE,"E247"),sQuery(id+"F8.wireOp",EDGE,"E248")])]});
            var Q1;
            Q1=makeQuery(id+"F9.opExtrude","SWEPT_BODY",BODY,{"disambiguationData":[OSD([sQuery(id+"F8.wireOp",EDGE,"E228"),sQuery(id+"F8.wireOp",EDGE,"E249"),sQuery(id+"F8.wireOp",EDGE,"E250"),sQuery(id+"F8.wireOp",EDGE,"E251"),sQuery(id+"F8.wireOp",EDGE,"E252"),sQuery(id+"F8.wireOp",EDGE,"E253"),sQuery(id+"F8.wireOp",EDGE,"E254"),sQuery(id+"F8.wireOp",EDGE,"E255"),sQuery(id+"F8.wireOp",EDGE,"E256"),sQuery(id+"F8.wireOp",EDGE,"E257"),sQuery(id+"F8.wireOp",EDGE,"E258"),sQuery(id+"F8.wireOp",EDGE,"E259"),sQuery(id+"F8.wireOp",EDGE,"E260"),sQuery(id+"F8.wireOp",EDGE,"E261"),sQuery(id+"F8.wireOp",EDGE,"E262"),sQuery(id+"F8.wireOp",EDGE,"E263"),sQuery(id+"F8.wireOp",EDGE,"E264"),sQuery(id+"F8.wireOp",EDGE,"E265"),sQuery(id+"F8.wireOp",EDGE,"E266"),sQuery(id+"F8.wireOp",EDGE,"E267"),sQuery(id+"F8.wireOp",EDGE,"E268"),sQuery(id+"F8.wireOp",EDGE,"E269"),sQuery(id+"F8.wireOp",EDGE,"E270"),sQuery(id+"F8.wireOp",EDGE,"E271"),sQuery(id+"F8.wireOp",EDGE,"E272"),sQuery(id+"F8.wireOp",EDGE,"E273"),sQuery(id+"F8.wireOp",EDGE,"E274"),sQuery(id+"F8.wireOp",EDGE,"E275"),sQuery(id+"F8.wireOp",EDGE,"E276"),sQuery(id+"F8.wireOp",EDGE,"E277"),sQuery(id+"F8.wireOp",EDGE,"E278"),sQuery(id+"F8.wireOp",EDGE,"E279"),sQuery(id+"F8.wireOp",EDGE,"E280"),sQuery(id+"F8.wireOp",EDGE,"E281"),sQuery(id+"F8.wireOp",EDGE,"E282"),sQuery(id+"F8.wireOp",EDGE,"E283"),sQuery(id+"F8.wireOp",EDGE,"E284"),sQuery(id+"F8.wireOp",EDGE,"E285"),sQuery(id+"F8.wireOp",EDGE,"E286"),sQuery(id+"F8.wireOp",EDGE,"E287"),sQuery(id+"F8.wireOp",EDGE,"E288"),sQuery(id+"F8.wireOp",EDGE,"E289"),sQuery(id+"F8.wireOp",EDGE,"E290"),sQuery(id+"F8.wireOp",EDGE,"E291"),sQuery(id+"F8.wireOp",EDGE,"E292"),sQuery(id+"F8.wireOp",EDGE,"E293"),sQuery(id+"F8.wireOp",EDGE,"E294"),sQuery(id+"F8.wireOp",EDGE,"E295"),sQuery(id+"F8.wireOp",EDGE,"E296"),sQuery(id+"F8.wireOp",EDGE,"E297"),sQuery(id+"F8.wireOp",EDGE,"E298"),sQuery(id+"F8.wireOp",EDGE,"E299"),sQuery(id+"F8.wireOp",EDGE,"E300"),sQuery(id+"F8.wireOp",EDGE,"E301"),sQuery(id+"F8.wireOp",EDGE,"E302"),sQuery(id+"F8.wireOp",EDGE,"E303"),sQuery(id+"F8.wireOp",EDGE,"E304"),sQuery(id+"F8.wireOp",EDGE,"E305"),sQuery(id+"F8.wireOp",EDGE,"E306"),sQuery(id+"F8.wireOp",EDGE,"E307")])]});
            var Q2;
            Q2=makeQuery(id+"F9.opExtrude","SWEPT_BODY",BODY,{"disambiguationData":[OSD([sQuery(id+"F8.wireOp",EDGE,"E767"),sQuery(id+"F8.wireOp",EDGE,"E768"),sQuery(id+"F8.wireOp",EDGE,"E769"),sQuery(id+"F8.wireOp",EDGE,"E770"),sQuery(id+"F8.wireOp",EDGE,"E771"),sQuery(id+"F8.wireOp",EDGE,"E772"),sQuery(id+"F8.wireOp",EDGE,"E773"),sQuery(id+"F8.wireOp",EDGE,"E774"),sQuery(id+"F8.wireOp",EDGE,"E775"),sQuery(id+"F8.wireOp",EDGE,"E776"),sQuery(id+"F8.wireOp",EDGE,"E777"),sQuery(id+"F8.wireOp",EDGE,"E778"),sQuery(id+"F8.wireOp",EDGE,"E779"),sQuery(id+"F8.wireOp",EDGE,"E780"),sQuery(id+"F8.wireOp",EDGE,"E781"),sQuery(id+"F8.wireOp",EDGE,"E782"),sQuery(id+"F8.wireOp",EDGE,"E783"),sQuery(id+"F8.wireOp",EDGE,"E784"),sQuery(id+"F8.wireOp",EDGE,"E785"),sQuery(id+"F8.wireOp",EDGE,"E786"),sQuery(id+"F8.wireOp",EDGE,"E787"),sQuery(id+"F8.wireOp",EDGE,"E788"),sQuery(id+"F8.wireOp",EDGE,"E789"),sQuery(id+"F8.wireOp",EDGE,"E790"),sQuery(id+"F8.wireOp",EDGE,"E791"),sQuery(id+"F8.wireOp",EDGE,"E792"),sQuery(id+"F8.wireOp",EDGE,"E793"),sQuery(id+"F8.wireOp",EDGE,"E794"),sQuery(id+"F8.wireOp",EDGE,"E795"),sQuery(id+"F8.wireOp",EDGE,"E796"),sQuery(id+"F8.wireOp",EDGE,"E797"),sQuery(id+"F8.wireOp",EDGE,"E798"),sQuery(id+"F8.wireOp",EDGE,"E799"),sQuery(id+"F8.wireOp",EDGE,"E800"),sQuery(id+"F8.wireOp",EDGE,"E801"),sQuery(id+"F8.wireOp",EDGE,"E802"),sQuery(id+"F8.wireOp",EDGE,"E803"),sQuery(id+"F8.wireOp",EDGE,"E804"),sQuery(id+"F8.wireOp",EDGE,"E805"),sQuery(id+"F8.wireOp",EDGE,"E806")])]});
            var Q3;
            Q3=makeQuery(id+"F9.opExtrude","SWEPT_BODY",BODY,{"disambiguationData":[OSD([sQuery(id+"F8.wireOp",EDGE,"E759"),sQuery(id+"F8.wireOp",EDGE,"E760"),sQuery(id+"F8.wireOp",EDGE,"E761"),sQuery(id+"F8.wireOp",EDGE,"E762"),sQuery(id+"F8.wireOp",EDGE,"E763"),sQuery(id+"F8.wireOp",EDGE,"E764"),sQuery(id+"F8.wireOp",EDGE,"E765"),sQuery(id+"F8.wireOp",EDGE,"E766")])]});
            var Q4;
            Q4=makeQuery(id+"F9.opExtrude","SWEPT_BODY",BODY,{"disambiguationData":[OSD([sQuery(id+"F8.wireOp",EDGE,"E729"),sQuery(id+"F8.wireOp",EDGE,"E730"),sQuery(id+"F8.wireOp",EDGE,"E731"),sQuery(id+"F8.wireOp",EDGE,"E732"),sQuery(id+"F8.wireOp",EDGE,"E733"),sQuery(id+"F8.wireOp",EDGE,"E734"),sQuery(id+"F8.wireOp",EDGE,"E735"),sQuery(id+"F8.wireOp",EDGE,"E736"),sQuery(id+"F8.wireOp",EDGE,"E737"),sQuery(id+"F8.wireOp",EDGE,"E738"),sQuery(id+"F8.wireOp",EDGE,"E739"),sQuery(id+"F8.wireOp",EDGE,"E740"),sQuery(id+"F8.wireOp",EDGE,"E741"),sQuery(id+"F8.wireOp",EDGE,"E742"),sQuery(id+"F8.wireOp",EDGE,"E743"),sQuery(id+"F8.wireOp",EDGE,"E744"),sQuery(id+"F8.wireOp",EDGE,"E745"),sQuery(id+"F8.wireOp",EDGE,"E746"),sQuery(id+"F8.wireOp",EDGE,"E747"),sQuery(id+"F8.wireOp",EDGE,"E748"),sQuery(id+"F8.wireOp",EDGE,"E749"),sQuery(id+"F8.wireOp",EDGE,"E750"),sQuery(id+"F8.wireOp",EDGE,"E751"),sQuery(id+"F8.wireOp",EDGE,"E752"),sQuery(id+"F8.wireOp",EDGE,"E753"),sQuery(id+"F8.wireOp",EDGE,"E754"),sQuery(id+"F8.wireOp",EDGE,"E755"),sQuery(id+"F8.wireOp",EDGE,"E756"),sQuery(id+"F8.wireOp",EDGE,"E757"),sQuery(id+"F8.wireOp",EDGE,"E758")])]});
            var Q5;
            Q5=makeQuery(id+"F9.opExtrude","SWEPT_BODY",BODY,{"disambiguationData":[OSD([sQuery(id+"F8.wireOp",EDGE,"E689"),sQuery(id+"F8.wireOp",EDGE,"E690"),sQuery(id+"F8.wireOp",EDGE,"E691"),sQuery(id+"F8.wireOp",EDGE,"E692"),sQuery(id+"F8.wireOp",EDGE,"E693"),sQuery(id+"F8.wireOp",EDGE,"E694"),sQuery(id+"F8.wireOp",EDGE,"E695"),sQuery(id+"F8.wireOp",EDGE,"E698"),sQuery(id+"F8.wireOp",EDGE,"E699"),sQuery(id+"F8.wireOp",EDGE,"E700"),sQuery(id+"F8.wireOp",EDGE,"E701"),sQuery(id+"F8.wireOp",EDGE,"E702"),sQuery(id+"F8.wireOp",EDGE,"E703"),sQuery(id+"F8.wireOp",EDGE,"E704"),sQuery(id+"F8.wireOp",EDGE,"E705"),sQuery(id+"F8.wireOp",EDGE,"E706"),sQuery(id+"F8.wireOp",EDGE,"E707"),sQuery(id+"F8.wireOp",EDGE,"E708"),sQuery(id+"F8.wireOp",EDGE,"E711"),sQuery(id+"F8.wireOp",EDGE,"E712"),sQuery(id+"F8.wireOp",EDGE,"E713"),sQuery(id+"F8.wireOp",EDGE,"E714")])]});
            var Q6;
            Q6=makeQuery(id+"F9.opExtrude","SWEPT_BODY",BODY,{"disambiguationData":[OSD([sQuery(id+"F8.wireOp",EDGE,"E709"),sQuery(id+"F8.wireOp",EDGE,"E710"),sQuery(id+"F8.wireOp",EDGE,"E715"),sQuery(id+"F8.wireOp",EDGE,"E716"),sQuery(id+"F8.wireOp",EDGE,"E717"),sQuery(id+"F8.wireOp",EDGE,"E718"),sQuery(id+"F8.wireOp",EDGE,"E719"),sQuery(id+"F8.wireOp",EDGE,"E720"),sQuery(id+"F8.wireOp",EDGE,"E722"),sQuery(id+"F8.wireOp",EDGE,"E723"),sQuery(id+"F8.wireOp",EDGE,"E724"),sQuery(id+"F8.wireOp",EDGE,"E725"),sQuery(id+"F8.wireOp",EDGE,"E726"),sQuery(id+"F8.wireOp",EDGE,"E727"),sQuery(id+"F8.wireOp",EDGE,"E728")])]});
            var Q7;
            Q7=makeQuery(id+"F9.opExtrude","SWEPT_BODY",BODY,{"disambiguationData":[OSD([sQuery(id+"F8.wireOp",EDGE,"E678"),sQuery(id+"F8.wireOp",EDGE,"E679"),sQuery(id+"F8.wireOp",EDGE,"E682"),sQuery(id+"F8.wireOp",EDGE,"E683"),sQuery(id+"F8.wireOp",EDGE,"E684"),sQuery(id+"F8.wireOp",EDGE,"E685"),sQuery(id+"F8.wireOp",EDGE,"E686"),sQuery(id+"F8.wireOp",EDGE,"E687"),sQuery(id+"F8.wireOp",EDGE,"E688"),sQuery(id+"F8.wireOp",EDGE,"E696"),sQuery(id+"F8.wireOp",EDGE,"E697")])]});
            var Q8;
            Q8=makeQuery(id+"F9.opExtrude","SWEPT_BODY",BODY,{"disambiguationData":[OSD([sQuery(id+"F8.wireOp",EDGE,"E547"),sQuery(id+"F8.wireOp",EDGE,"E548"),sQuery(id+"F8.wireOp",EDGE,"E549"),sQuery(id+"F8.wireOp",EDGE,"E550"),sQuery(id+"F8.wireOp",EDGE,"E551"),sQuery(id+"F8.wireOp",EDGE,"E552"),sQuery(id+"F8.wireOp",EDGE,"E553"),sQuery(id+"F8.wireOp",EDGE,"E554"),sQuery(id+"F8.wireOp",EDGE,"E555"),sQuery(id+"F8.wireOp",EDGE,"E556"),sQuery(id+"F8.wireOp",EDGE,"E557"),sQuery(id+"F8.wireOp",EDGE,"E558"),sQuery(id+"F8.wireOp",EDGE,"E559"),sQuery(id+"F8.wireOp",EDGE,"E560"),sQuery(id+"F8.wireOp",EDGE,"E561"),sQuery(id+"F8.wireOp",EDGE,"E562"),sQuery(id+"F8.wireOp",EDGE,"E563"),sQuery(id+"F8.wireOp",EDGE,"E564"),sQuery(id+"F8.wireOp",EDGE,"E565"),sQuery(id+"F8.wireOp",EDGE,"E566"),sQuery(id+"F8.wireOp",EDGE,"E567"),sQuery(id+"F8.wireOp",EDGE,"E568"),sQuery(id+"F8.wireOp",EDGE,"E569"),sQuery(id+"F8.wireOp",EDGE,"E570"),sQuery(id+"F8.wireOp",EDGE,"E571"),sQuery(id+"F8.wireOp",EDGE,"E572"),sQuery(id+"F8.wireOp",EDGE,"E573"),sQuery(id+"F8.wireOp",EDGE,"E574"),sQuery(id+"F8.wireOp",EDGE,"E575"),sQuery(id+"F8.wireOp",EDGE,"E576"),sQuery(id+"F8.wireOp",EDGE,"E577"),sQuery(id+"F8.wireOp",EDGE,"E578"),sQuery(id+"F8.wireOp",EDGE,"E579"),sQuery(id+"F8.wireOp",EDGE,"E580"),sQuery(id+"F8.wireOp",EDGE,"E581"),sQuery(id+"F8.wireOp",EDGE,"E582"),sQuery(id+"F8.wireOp",EDGE,"E583"),sQuery(id+"F8.wireOp",EDGE,"E584"),sQuery(id+"F8.wireOp",EDGE,"E585"),sQuery(id+"F8.wireOp",EDGE,"E586"),sQuery(id+"F8.wireOp",EDGE,"E587"),sQuery(id+"F8.wireOp",EDGE,"E588"),sQuery(id+"F8.wireOp",EDGE,"E589"),sQuery(id+"F8.wireOp",EDGE,"E590"),sQuery(id+"F8.wireOp",EDGE,"E591"),sQuery(id+"F8.wireOp",EDGE,"E592"),sQuery(id+"F8.wireOp",EDGE,"E593"),sQuery(id+"F8.wireOp",EDGE,"E594"),sQuery(id+"F8.wireOp",EDGE,"E595"),sQuery(id+"F8.wireOp",EDGE,"E596"),sQuery(id+"F8.wireOp",EDGE,"E597"),sQuery(id+"F8.wireOp",EDGE,"E598"),sQuery(id+"F8.wireOp",EDGE,"E599"),sQuery(id+"F8.wireOp",EDGE,"E600"),sQuery(id+"F8.wireOp",EDGE,"E601"),sQuery(id+"F8.wireOp",EDGE,"E602"),sQuery(id+"F8.wireOp",EDGE,"E603"),sQuery(id+"F8.wireOp",EDGE,"E604"),sQuery(id+"F8.wireOp",EDGE,"E605"),sQuery(id+"F8.wireOp",EDGE,"E606")])]});
            var Q9;
            Q9=makeQuery(id+"F9.opExtrude","SWEPT_BODY",BODY,{"disambiguationData":[OSD([sQuery(id+"F8.wireOp",EDGE,"E534"),sQuery(id+"F8.wireOp",EDGE,"E535"),sQuery(id+"F8.wireOp",EDGE,"E536"),sQuery(id+"F8.wireOp",EDGE,"E537"),sQuery(id+"F8.wireOp",EDGE,"E538"),sQuery(id+"F8.wireOp",EDGE,"E539"),sQuery(id+"F8.wireOp",EDGE,"E540"),sQuery(id+"F8.wireOp",EDGE,"E541"),sQuery(id+"F8.wireOp",EDGE,"E542"),sQuery(id+"F8.wireOp",EDGE,"E543"),sQuery(id+"F8.wireOp",EDGE,"E544"),sQuery(id+"F8.wireOp",EDGE,"E545")])]});
            var Q10;
            Q10=makeQuery(id+"F9.opExtrude","SWEPT_BODY",BODY,{"disambiguationData":[OSD([sQuery(id+"F8.wireOp",EDGE,"E514"),sQuery(id+"F8.wireOp",EDGE,"E515"),sQuery(id+"F8.wireOp",EDGE,"E516"),sQuery(id+"F8.wireOp",EDGE,"E517"),sQuery(id+"F8.wireOp",EDGE,"E518"),sQuery(id+"F8.wireOp",EDGE,"E519"),sQuery(id+"F8.wireOp",EDGE,"E520"),sQuery(id+"F8.wireOp",EDGE,"E521"),sQuery(id+"F8.wireOp",EDGE,"E522"),sQuery(id+"F8.wireOp",EDGE,"E523"),sQuery(id+"F8.wireOp",EDGE,"E524"),sQuery(id+"F8.wireOp",EDGE,"E525"),sQuery(id+"F8.wireOp",EDGE,"E526"),sQuery(id+"F8.wireOp",EDGE,"E527"),sQuery(id+"F8.wireOp",EDGE,"E528"),sQuery(id+"F8.wireOp",EDGE,"E529"),sQuery(id+"F8.wireOp",EDGE,"E530"),sQuery(id+"F8.wireOp",EDGE,"E531"),sQuery(id+"F8.wireOp",EDGE,"E532"),sQuery(id+"F8.wireOp",EDGE,"E533")])]});
            var Q11;
            Q11=makeQuery(id+"F9.opExtrude","SWEPT_BODY",BODY,{"disambiguationData":[OSD([sQuery(id+"F8.wireOp",EDGE,"E508"),sQuery(id+"F8.wireOp",EDGE,"E509"),sQuery(id+"F8.wireOp",EDGE,"E510")])]});
            var Q12;
            Q12=makeQuery(id+"F9.opExtrude","SWEPT_BODY",BODY,{"disambiguationData":[OSD([sQuery(id+"F8.wireOp",EDGE,"E504"),sQuery(id+"F8.wireOp",EDGE,"E505"),sQuery(id+"F8.wireOp",EDGE,"E506"),sQuery(id+"F8.wireOp",EDGE,"E507")])]});
            var Q13;
            Q13=makeQuery(id+"F9.opExtrude","SWEPT_BODY",BODY,{"disambiguationData":[OSD([sQuery(id+"F8.wireOp",EDGE,"E501"),sQuery(id+"F8.wireOp",EDGE,"E502"),sQuery(id+"F8.wireOp",EDGE,"E503")])]});
            var Q14;
            Q14=makeQuery(id+"F9.opExtrude","SWEPT_BODY",BODY,{"disambiguationData":[OSD([sQuery(id+"F8.wireOp",EDGE,"E511"),sQuery(id+"F8.wireOp",EDGE,"E512"),sQuery(id+"F8.wireOp",EDGE,"E513")])]});
            var Q15;
            Q15=makeQuery(id+"F9.opExtrude","SWEPT_BODY",BODY,{"disambiguationData":[OSD([sQuery(id+"F8.wireOp",EDGE,"E493"),sQuery(id+"F8.wireOp",EDGE,"E494"),sQuery(id+"F8.wireOp",EDGE,"E495"),sQuery(id+"F8.wireOp",EDGE,"E496")])]});
            var Q16;
            Q16=makeQuery(id+"F9.opExtrude","SWEPT_BODY",BODY,{"disambiguationData":[OSD([sQuery(id+"F8.wireOp",EDGE,"E490"),sQuery(id+"F8.wireOp",EDGE,"E491"),sQuery(id+"F8.wireOp",EDGE,"E492")])]});
            var Q17;
            Q17=makeQuery(id+"F9.opExtrude","SWEPT_BODY",BODY,{"disambiguationData":[OSD([sQuery(id+"F8.wireOp",EDGE,"E487"),sQuery(id+"F8.wireOp",EDGE,"E488"),sQuery(id+"F8.wireOp",EDGE,"E489")])]});
            var Q18;
            Q18=makeQuery(id+"F9.opExtrude","SWEPT_BODY",BODY,{"disambiguationData":[OSD([sQuery(id+"F8.wireOp",EDGE,"E497"),sQuery(id+"F8.wireOp",EDGE,"E498"),sQuery(id+"F8.wireOp",EDGE,"E499"),sQuery(id+"F8.wireOp",EDGE,"E500")])]});
            var Q19;
            Q19=makeQuery(id+"F9.opExtrude","SWEPT_BODY",BODY,{"disambiguationData":[OSD([sQuery(id+"F8.wireOp",EDGE,"E484"),sQuery(id+"F8.wireOp",EDGE,"E485"),sQuery(id+"F8.wireOp",EDGE,"E486")])]});
            var Q20;
            Q20=makeQuery(id+"F9.opExtrude","SWEPT_BODY",BODY,{"disambiguationData":[OSD([sQuery(id+"F8.wireOp",EDGE,"E481"),sQuery(id+"F8.wireOp",EDGE,"E482"),sQuery(id+"F8.wireOp",EDGE,"E483")])]});
            var Q21;
            Q21=makeQuery(id+"F9.opExtrude","SWEPT_BODY",BODY,{"disambiguationData":[OSD([sQuery(id+"F8.wireOp",EDGE,"E478"),sQuery(id+"F8.wireOp",EDGE,"E479"),sQuery(id+"F8.wireOp",EDGE,"E480")])]});
            var Q22;
            Q22=makeQuery(id+"F9.opExtrude","SWEPT_BODY",BODY,{"disambiguationData":[OSD([sQuery(id+"F8.wireOp",EDGE,"E475"),sQuery(id+"F8.wireOp",EDGE,"E476"),sQuery(id+"F8.wireOp",EDGE,"E477")])]});
            var Q23;
            Q23=makeQuery(id+"F9.opExtrude","SWEPT_BODY",BODY,{"disambiguationData":[OSD([sQuery(id+"F8.wireOp",EDGE,"E471"),sQuery(id+"F8.wireOp",EDGE,"E472"),sQuery(id+"F8.wireOp",EDGE,"E473"),sQuery(id+"F8.wireOp",EDGE,"E474")])]});
            var Q24;
            Q24=makeQuery(id+"F9.opExtrude","SWEPT_BODY",BODY,{"disambiguationData":[OSD([sQuery(id+"F8.wireOp",EDGE,"E467"),sQuery(id+"F8.wireOp",EDGE,"E468"),sQuery(id+"F8.wireOp",EDGE,"E469"),sQuery(id+"F8.wireOp",EDGE,"E470")])]});
            var Q25;
            Q25=makeQuery(id+"F9.opExtrude","SWEPT_BODY",BODY,{"disambiguationData":[OSD([sQuery(id+"F8.wireOp",EDGE,"E464"),sQuery(id+"F8.wireOp",EDGE,"E465"),sQuery(id+"F8.wireOp",EDGE,"E466")])]});
            var Q26;
            Q26=makeQuery(id+"F9.opExtrude","SWEPT_BODY",BODY,{"disambiguationData":[OSD([sQuery(id+"F8.wireOp",EDGE,"E461"),sQuery(id+"F8.wireOp",EDGE,"E462"),sQuery(id+"F8.wireOp",EDGE,"E463")])]});
            var Q27;
            Q27=makeQuery(id+"F9.opExtrude","SWEPT_BODY",BODY,{"disambiguationData":[OSD([sQuery(id+"F8.wireOp",EDGE,"E404"),sQuery(id+"F8.wireOp",EDGE,"E405"),sQuery(id+"F8.wireOp",EDGE,"E406"),sQuery(id+"F8.wireOp",EDGE,"E407"),sQuery(id+"F8.wireOp",EDGE,"E408"),sQuery(id+"F8.wireOp",EDGE,"E409"),sQuery(id+"F8.wireOp",EDGE,"E410"),sQuery(id+"F8.wireOp",EDGE,"E411"),sQuery(id+"F8.wireOp",EDGE,"E412"),sQuery(id+"F8.wireOp",EDGE,"E413"),sQuery(id+"F8.wireOp",EDGE,"E414"),sQuery(id+"F8.wireOp",EDGE,"E415"),sQuery(id+"F8.wireOp",EDGE,"E416"),sQuery(id+"F8.wireOp",EDGE,"E417"),sQuery(id+"F8.wireOp",EDGE,"E418"),sQuery(id+"F8.wireOp",EDGE,"E419"),sQuery(id+"F8.wireOp",EDGE,"E420"),sQuery(id+"F8.wireOp",EDGE,"E421"),sQuery(id+"F8.wireOp",EDGE,"E422"),sQuery(id+"F8.wireOp",EDGE,"E423")])]});
            var Q28;
            Q28=makeQuery(id+"F9.opExtrude","SWEPT_BODY",BODY,{"disambiguationData":[OSD([sQuery(id+"F8.wireOp",EDGE,"E327"),sQuery(id+"F8.wireOp",EDGE,"E328"),sQuery(id+"F8.wireOp",EDGE,"E329"),sQuery(id+"F8.wireOp",EDGE,"E330"),sQuery(id+"F8.wireOp",EDGE,"E331"),sQuery(id+"F8.wireOp",EDGE,"E332"),sQuery(id+"F8.wireOp",EDGE,"E333"),sQuery(id+"F8.wireOp",EDGE,"E334"),sQuery(id+"F8.wireOp",EDGE,"E335"),sQuery(id+"F8.wireOp",EDGE,"E336"),sQuery(id+"F8.wireOp",EDGE,"E337"),sQuery(id+"F8.wireOp",EDGE,"E338"),sQuery(id+"F8.wireOp",EDGE,"E339"),sQuery(id+"F8.wireOp",EDGE,"E340"),sQuery(id+"F8.wireOp",EDGE,"E341"),sQuery(id+"F8.wireOp",EDGE,"E342"),sQuery(id+"F8.wireOp",EDGE,"E343"),sQuery(id+"F8.wireOp",EDGE,"E344"),sQuery(id+"F8.wireOp",EDGE,"E345"),sQuery(id+"F8.wireOp",EDGE,"E346"),sQuery(id+"F8.wireOp",EDGE,"E347"),sQuery(id+"F8.wireOp",EDGE,"E348"),sQuery(id+"F8.wireOp",EDGE,"E349"),sQuery(id+"F8.wireOp",EDGE,"E350"),sQuery(id+"F8.wireOp",EDGE,"E351"),sQuery(id+"F8.wireOp",EDGE,"E352"),sQuery(id+"F8.wireOp",EDGE,"E353"),sQuery(id+"F8.wireOp",EDGE,"E354"),sQuery(id+"F8.wireOp",EDGE,"E355")])]});
            var Q29;
            Q29=makeQuery(id+"F9.opExtrude","SWEPT_BODY",BODY,{"disambiguationData":[OSD([sQuery(id+"F8.wireOp",EDGE,"E308"),sQuery(id+"F8.wireOp",EDGE,"E309"),sQuery(id+"F8.wireOp",EDGE,"E310"),sQuery(id+"F8.wireOp",EDGE,"E311"),sQuery(id+"F8.wireOp",EDGE,"E312"),sQuery(id+"F8.wireOp",EDGE,"E313"),sQuery(id+"F8.wireOp",EDGE,"E314"),sQuery(id+"F8.wireOp",EDGE,"E315"),sQuery(id+"F8.wireOp",EDGE,"E317"),sQuery(id+"F8.wireOp",EDGE,"E318"),sQuery(id+"F8.wireOp",EDGE,"E319"),sQuery(id+"F8.wireOp",EDGE,"E320"),sQuery(id+"F8.wireOp",EDGE,"E321"),sQuery(id+"F8.wireOp",EDGE,"E323"),sQuery(id+"F8.wireOp",EDGE,"E324"),sQuery(id+"F8.wireOp",EDGE,"E325")])]});
            var Q30;
            Q30=makeQuery(id+"F9.opExtrude","SWEPT_BODY",BODY,{"disambiguationData":[OSD([sQuery(id+"F8.wireOp",EDGE,"E435"),sQuery(id+"F8.wireOp",EDGE,"E436"),sQuery(id+"F8.wireOp",EDGE,"E437"),sQuery(id+"F8.wireOp",EDGE,"E438"),sQuery(id+"F8.wireOp",EDGE,"E439"),sQuery(id+"F8.wireOp",EDGE,"E440"),sQuery(id+"F8.wireOp",EDGE,"E441"),sQuery(id+"F8.wireOp",EDGE,"E442"),sQuery(id+"F8.wireOp",EDGE,"E443"),sQuery(id+"F8.wireOp",EDGE,"E444"),sQuery(id+"F8.wireOp",EDGE,"E445"),sQuery(id+"F8.wireOp",EDGE,"E446"),sQuery(id+"F8.wireOp",EDGE,"E447"),sQuery(id+"F8.wireOp",EDGE,"E448"),sQuery(id+"F8.wireOp",EDGE,"E449"),sQuery(id+"F8.wireOp",EDGE,"E450"),sQuery(id+"F8.wireOp",EDGE,"E451"),sQuery(id+"F8.wireOp",EDGE,"E452"),sQuery(id+"F8.wireOp",EDGE,"E453"),sQuery(id+"F8.wireOp",EDGE,"E454"),sQuery(id+"F8.wireOp",EDGE,"E455"),sQuery(id+"F8.wireOp",EDGE,"E456"),sQuery(id+"F8.wireOp",EDGE,"E457"),sQuery(id+"F8.wireOp",EDGE,"E458"),sQuery(id+"F8.wireOp",EDGE,"E459")])]});
            var Q31;
            {var subQ0=sQuery(id+"F0.wireOp",EDGE,"E53");var subQ1=sQuery(id+"F0.wireOp",EDGE,"E50");var subQ2=sQuery(id+"F0.wireOp",EDGE,"E0.top");Q31=makeQuery(id+"F2.opFillet","BLEND_EDGE",EDGE,{"blendedFrom":[makeQuery(id+"F1.opExtrude","CAP_EDGE",EDGE,{"disambiguationData":[OSD([subQ2,subQ1,subQ0])],"isStart":false}),makeQuery(id+"F1.opExtrude","CAP_FACE",FACE,{"disambiguationData":[OSD([sQuery(id+"F0.wireOp",EDGE,"E0.bottom"),subQ2,sQuery(id+"F0.wireOp",EDGE,"E32.bottom"),sQuery(id+"F0.wireOp",EDGE,"E32.top"),sQuery(id+"F0.wireOp",EDGE,"E32.left"),sQuery(id+"F0.wireOp",EDGE,"E32.right"),sQuery(id+"F0.wireOp",EDGE,"E34.bottom"),sQuery(id+"F0.wireOp",EDGE,"E34.top"),sQuery(id+"F0.wireOp",EDGE,"E34.left"),sQuery(id+"F0.wireOp",EDGE,"E34.right"),sQuery(id+"F0.wireOp",EDGE,"E37"),sQuery(id+"F0.wireOp",EDGE,"E39.MirrorC"),sQuery(id+"F0.wireOp",EDGE,"E42"),sQuery(id+"F0.wireOp",EDGE,"E43.MirrorC"),sQuery(id+"F0.wireOp",EDGE,"E44"),sQuery(id+"F0.wireOp",EDGE,"E45.MirrorC"),sQuery(id+"F0.wireOp",EDGE,"E47.bottom"),sQuery(id+"F0.wireOp",EDGE,"E47.top"),sQuery(id+"F0.wireOp",EDGE,"E47.left"),sQuery(id+"F0.wireOp",EDGE,"E47.right"),sQuery(id+"F0.wireOp",EDGE,"E48"),sQuery(id+"F0.wireOp",EDGE,"E49"),subQ1,sQuery(id+"F0.wireOp",EDGE,"E51"),sQuery(id+"F0.wireOp",EDGE,"E52"),subQ0,sQuery(id+"F0.wireOp",EDGE,"E59"),sQuery(id+"F0.wireOp",EDGE,"E61"),sQuery(id+"F0.wireOp",EDGE,"E63"),sQuery(id+"F0.wireOp",EDGE,"E65"),sQuery(id+"F0.wireOp",EDGE,"E68.bottom"),sQuery(id+"F0.wireOp",EDGE,"E68.top"),sQuery(id+"F0.wireOp",EDGE,"E68.left"),sQuery(id+"F0.wireOp",EDGE,"E68.right")])],"isStart":false})],"blendedInto":[makeQuery(id+"F1.opExtrude","CAP_FACE",FACE,{"disambiguationData":[OSD([sQuery(id+"F0.wireOp",EDGE,"E0.bottom"),subQ2,sQuery(id+"F0.wireOp",EDGE,"E32.bottom"),sQuery(id+"F0.wireOp",EDGE,"E32.top"),sQuery(id+"F0.wireOp",EDGE,"E32.left"),sQuery(id+"F0.wireOp",EDGE,"E32.right"),sQuery(id+"F0.wireOp",EDGE,"E34.bottom"),sQuery(id+"F0.wireOp",EDGE,"E34.top"),sQuery(id+"F0.wireOp",EDGE,"E34.left"),sQuery(id+"F0.wireOp",EDGE,"E34.right"),sQuery(id+"F0.wireOp",EDGE,"E37"),sQuery(id+"F0.wireOp",EDGE,"E39.MirrorC"),sQuery(id+"F0.wireOp",EDGE,"E42"),sQuery(id+"F0.wireOp",EDGE,"E43.MirrorC"),sQuery(id+"F0.wireOp",EDGE,"E44"),sQuery(id+"F0.wireOp",EDGE,"E45.MirrorC"),sQuery(id+"F0.wireOp",EDGE,"E47.bottom"),sQuery(id+"F0.wireOp",EDGE,"E47.top"),sQuery(id+"F0.wireOp",EDGE,"E47.left"),sQuery(id+"F0.wireOp",EDGE,"E47.right"),sQuery(id+"F0.wireOp",EDGE,"E48"),sQuery(id+"F0.wireOp",EDGE,"E49"),subQ1,sQuery(id+"F0.wireOp",EDGE,"E51"),sQuery(id+"F0.wireOp",EDGE,"E52"),subQ0,sQuery(id+"F0.wireOp",EDGE,"E59"),sQuery(id+"F0.wireOp",EDGE,"E61"),sQuery(id+"F0.wireOp",EDGE,"E63"),sQuery(id+"F0.wireOp",EDGE,"E65"),sQuery(id+"F0.wireOp",EDGE,"E68.bottom"),sQuery(id+"F0.wireOp",EDGE,"E68.top"),sQuery(id+"F0.wireOp",EDGE,"E68.left"),sQuery(id+"F0.wireOp",EDGE,"E68.right")])],"isStart":false})]});}
            transform(context, id + "F10", {"entities" : qUnion([Q0, Q1, Q2, Q3, Q4, Q5, Q6, Q7, Q8, Q9, Q10, Q11, Q12, Q13, Q14, Q15, Q16, Q17, Q18, Q19, Q20, Q21, Q22, Q23, Q24, Q25, Q26, Q27, Q28, Q29, Q30]), "transformType" : TransformType.TRANSLATION_DISTANCE, "transformDirection" : qUnion([Q31]), "distance" : 88 * mm, "oppositeDirection" : true, "makeCopy" : false});
        }
    });
